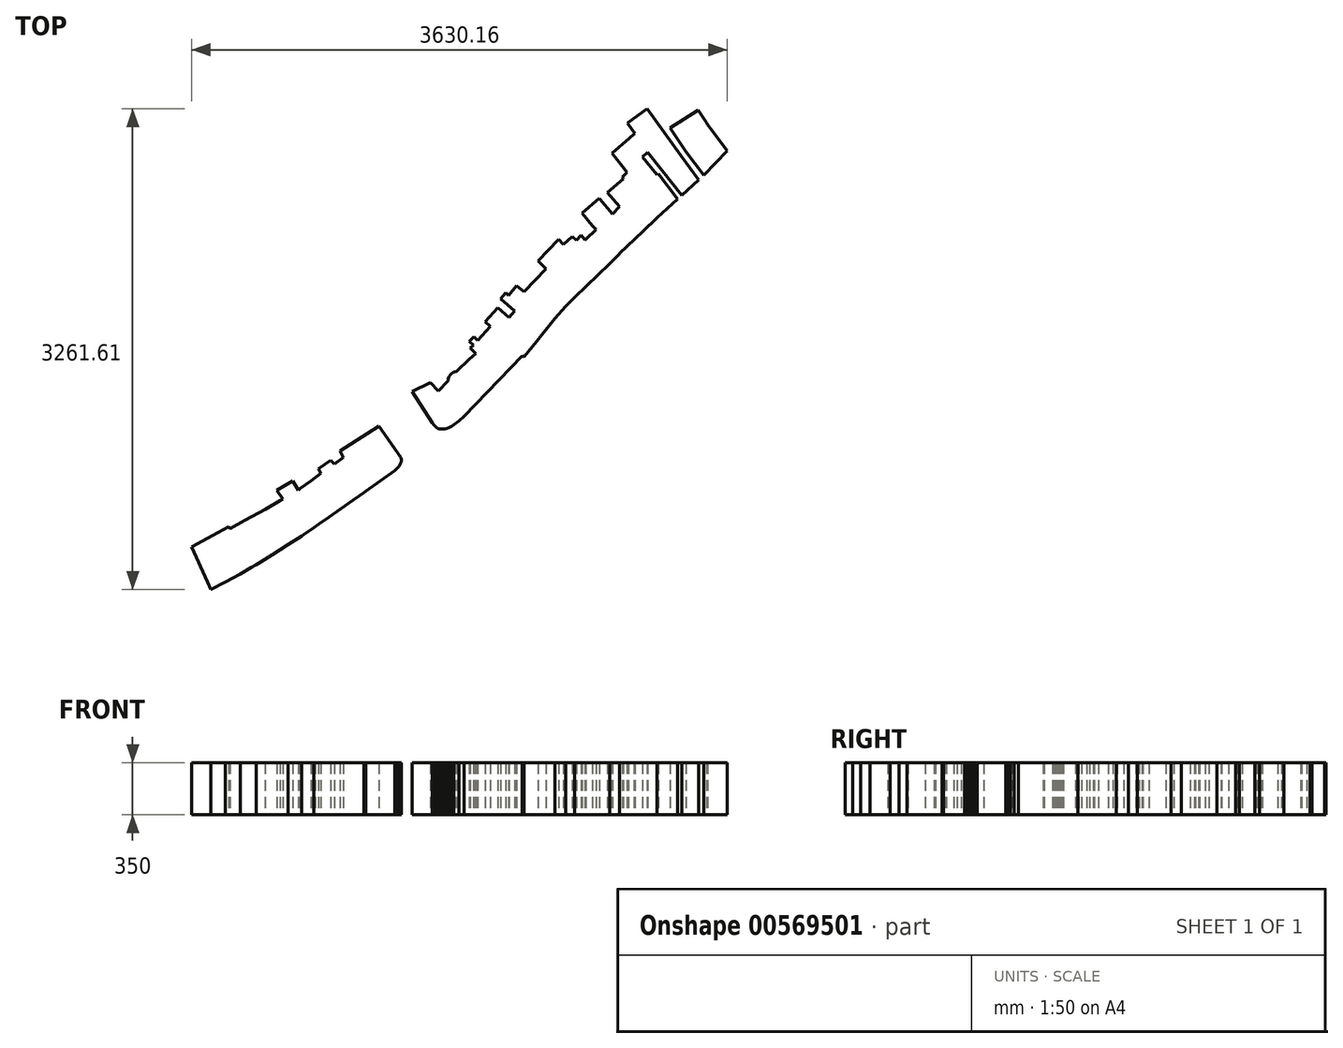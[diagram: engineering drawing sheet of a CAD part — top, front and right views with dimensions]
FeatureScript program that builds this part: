
annotation { "Feature Type Name" : "Feature", "Feature Type Description" : "" }
export const myFeature = defineFeature(function(context is Context, id is Id, definition is map)
    precondition{}
    {
        {
            var Q0;
            Q0=qCreatedBy(makeId("Top.planeOp"),FACE);
            var sketch = newSketch(context, id + "F0", { "sketchPlane" : qUnion([Q0])});
            skLineSegment(sketch, "E0", {"start": v(864.86, -2325.47) * mm, "end": v(899.9, -2380.58) * mm});
            skLineSegment(sketch, "E1", {"start": v(643.37, -1977.49) * mm, "end": v(719.57, -2092.3) * mm});
            skLineSegment(sketch, "E2", {"start": v(461.5, -1695.8) * mm, "end": v(495.8, -1752.95) * mm});
            skLineSegment(sketch, "E3", {"start": v(221.48, -1319.12) * mm, "end": v(179.57, -1255.11) * mm});
            skLineSegment(sketch, "E4", {"start": v(-61.73, -1340.7) * mm, "end": v(179.57, -1255.11) * mm});
            skLineSegment(sketch, "E5", {"start": v(784.34, 860.96) * mm, "end": v(794, 865.79) * mm});
            skLineSegment(sketch, "E6", {"start": v(-1984.51, 2355.5) * mm, "end": v(-1854.97, 2432.97) * mm});
            skLineSegment(sketch, "E7", {"start": v(-1903.23, 2229.77) * mm, "end": v(-1774.96, 2311.05) * mm});
            skLineSegment(sketch, "E8", {"start": v(265.42, -2033.62) * mm, "end": v(295.14, -2079.34) * mm});
            skLineSegment(sketch, "E9", {"start": v(295.14, -2079.34) * mm, "end": v(362.45, -2098.4) * mm});
            skLineSegment(sketch, "E10", {"start": v(362.45, -2098.4) * mm, "end": v(458.97, -2253.33) * mm});
            skLineSegment(sketch, "E11", {"start": v(458.97, -2253.33) * mm, "end": v(415.28, -2384.9) * mm});
            skLineSegment(sketch, "E12", {"start": v(1428.23, 985.42) * mm, "end": v(1558.79, 814.23) * mm});
            skLineSegment(sketch, "E13", {"start": v(1709.92, -1196.7) * mm, "end": v(1542.28, -1030.32) * mm});
            skLineSegment(sketch, "E14", {"start": v(1542.28, -1030.32) * mm, "end": v(1541.77, -1029.81) * mm});
            skLineSegment(sketch, "E15", {"start": v(2081.26, -1189.83) * mm, "end": v(2109.97, -1211.93) * mm});
            skLineSegment(sketch, "E16", {"start": v(2109.97, -1211.93) * mm, "end": v(2127.75, -1191.36) * mm});
            skLineSegment(sketch, "E17", {"start": v(913.37, -2395.82) * mm, "end": v(902.2, -2379.06) * mm});
            skLineSegment(sketch, "E18", {"start": v(902.2, -2379.06) * mm, "end": v(899.9, -2380.58) * mm});
            skLineSegment(sketch, "E19", {"start": v(899.9, -2380.58) * mm, "end": v(852.67, -2410.81) * mm});
            skLineSegment(sketch, "E20", {"start": v(852.67, -2410.81) * mm, "end": v(847.59, -2442.56) * mm});
            skLineSegment(sketch, "E21", {"start": v(847.59, -2442.56) * mm, "end": v(867.9, -2470.5) * mm});
            skLineSegment(sketch, "E22", {"start": v(867.9, -2470.5) * mm, "end": v(890.77, -2476.85) * mm});
            skLineSegment(sketch, "E23", {"start": v(890.77, -2476.85) * mm, "end": v(903.47, -2469.23) * mm});
            skLineSegment(sketch, "E24", {"start": v(-1735.6, -1544.67) * mm, "end": v(-1556.52, -1448.15) * mm});
            skLineSegment(sketch, "E25", {"start": v(-557.03, -1168.75) * mm, "end": v(-360.18, -1026.51) * mm});
            skLineSegment(sketch, "E26", {"start": v(2155.69, 896.27) * mm, "end": v(2129.02, 873.4) * mm});
            skLineSegment(sketch, "E27", {"start": v(2129.02, 873.4) * mm, "end": v(2121.4, 865.79) * mm});
            skLineSegment(sketch, "E28", {"start": v(2121.4, 865.79) * mm, "end": v(2116.32, 859.44) * mm});
            skLineSegment(sketch, "E29", {"start": v(2116.32, 859.44) * mm, "end": v(2019.8, 783.24) * mm});
            skLineSegment(sketch, "E30", {"start": v(2019.8, 783.24) * mm, "end": v(2004.56, 769.27) * mm});
            skLineSegment(sketch, "E31", {"start": v(2004.56, 769.27) * mm, "end": v(2000.75, 766.73) * mm});
            skLineSegment(sketch, "E32", {"start": v(2000.75, 766.73) * mm, "end": v(1982.97, 752.76) * mm});
            skLineSegment(sketch, "E33", {"start": v(1982.97, 752.76) * mm, "end": v(1976.62, 747.68) * mm});
            skLineSegment(sketch, "E34", {"start": v(1976.62, 747.68) * mm, "end": v(1972.8, 743.87) * mm});
            skLineSegment(sketch, "E35", {"start": v(1972.8, 743.87) * mm, "end": v(1969, 738.79) * mm});
            skLineSegment(sketch, "E36", {"start": v(1969, 738.79) * mm, "end": v(1966.46, 736.25) * mm});
            skLineSegment(sketch, "E37", {"start": v(1966.46, 736.25) * mm, "end": v(1963.92, 731.17) * mm});
            skLineSegment(sketch, "E38", {"start": v(1963.92, 731.17) * mm, "end": v(1960.1, 727.36) * mm});
            skLineSegment(sketch, "E39", {"start": v(1960.1, 727.36) * mm, "end": v(1939.79, 699.42) * mm});
            skLineSegment(sketch, "E40", {"start": v(1939.79, 699.42) * mm, "end": v(1935.98, 694.34) * mm});
            skLineSegment(sketch, "E41", {"start": v(1935.98, 694.34) * mm, "end": v(1849.62, 571.15) * mm});
            skLineSegment(sketch, "E42", {"start": v(1849.62, 571.15) * mm, "end": v(1843.27, 560.99) * mm});
            skLineSegment(sketch, "E43", {"start": v(1843.27, 560.99) * mm, "end": v(1830.57, 543.2) * mm});
            skLineSegment(sketch, "E44", {"start": v(1830.57, 543.2) * mm, "end": v(1822.95, 534.32) * mm});
            skLineSegment(sketch, "E45", {"start": v(1822.95, 534.32) * mm, "end": v(1810.25, 519.08) * mm});
            skLineSegment(sketch, "E46", {"start": v(1810.25, 519.08) * mm, "end": v(1773.42, 482.25) * mm});
            skLineSegment(sketch, "E47", {"start": v(1773.42, 482.25) * mm, "end": v(1755.64, 465.74) * mm});
            skLineSegment(sketch, "E48", {"start": v(1755.64, 465.74) * mm, "end": v(1740.4, 446.69) * mm});
            skLineSegment(sketch, "E49", {"start": v(1740.4, 446.69) * mm, "end": v(1739.13, 444.15) * mm});
            skLineSegment(sketch, "E50", {"start": v(1739.13, 444.15) * mm, "end": v(1562.6, 268.89) * mm});
            skLineSegment(sketch, "E51", {"start": v(1562.6, 268.89) * mm, "end": v(1539.74, 248.57) * mm});
            skLineSegment(sketch, "E52", {"start": v(1539.74, 248.57) * mm, "end": v(1533.39, 242.22) * mm});
            skLineSegment(sketch, "E53", {"start": v(1533.39, 242.22) * mm, "end": v(1511.8, 219.36) * mm});
            skLineSegment(sketch, "E54", {"start": v(1511.8, 219.36) * mm, "end": v(1501.64, 210.47) * mm});
            skLineSegment(sketch, "E55", {"start": v(1501.64, 210.47) * mm, "end": v(1492.75, 202.85) * mm});
            skLineSegment(sketch, "E56", {"start": v(1492.75, 202.85) * mm, "end": v(1485.13, 195.23) * mm});
            skLineSegment(sketch, "E57", {"start": v(1485.13, 195.23) * mm, "end": v(1474.97, 188.88) * mm});
            skLineSegment(sketch, "E58", {"start": v(1474.97, 188.88) * mm, "end": v(1464.8, 181.26) * mm});
            skLineSegment(sketch, "E59", {"start": v(1464.8, 181.26) * mm, "end": v(1457.19, 174.9) * mm});
            skLineSegment(sketch, "E60", {"start": v(1457.19, 174.9) * mm, "end": v(1421.63, 149.5) * mm});
            skLineSegment(sketch, "E61", {"start": v(1421.63, 149.5) * mm, "end": v(1416.55, 145.7) * mm});
            skLineSegment(sketch, "E62", {"start": v(1416.55, 145.7) * mm, "end": v(1191.76, -19.4) * mm});
            skLineSegment(sketch, "E63", {"start": v(1191.76, -19.4) * mm, "end": v(1186.68, -24.48) * mm});
            skLineSegment(sketch, "E64", {"start": v(1186.68, -24.48) * mm, "end": v(1176.52, -32.1) * mm});
            skLineSegment(sketch, "E65", {"start": v(1176.52, -32.1) * mm, "end": v(1171.44, -37.18) * mm});
            skLineSegment(sketch, "E66", {"start": v(1171.44, -37.18) * mm, "end": v(1167.63, -42.26) * mm});
            skLineSegment(sketch, "E67", {"start": v(1167.63, -42.26) * mm, "end": v(1162.55, -46.07) * mm});
            skLineSegment(sketch, "E68", {"start": v(1162.55, -46.07) * mm, "end": v(1153.66, -54.96) * mm});
            skLineSegment(sketch, "E69", {"start": v(1153.66, -54.96) * mm, "end": v(1151.12, -58.77) * mm});
            skLineSegment(sketch, "E70", {"start": v(1151.12, -58.77) * mm, "end": v(1143.5, -68.93) * mm});
            skLineSegment(sketch, "E71", {"start": v(1143.5, -68.93) * mm, "end": v(1139.69, -75.28) * mm});
            skLineSegment(sketch, "E72", {"start": v(1139.69, -75.28) * mm, "end": v(1135.88, -80.36) * mm});
            skLineSegment(sketch, "E73", {"start": v(1135.88, -80.36) * mm, "end": v(1132.07, -86.71) * mm});
            skLineSegment(sketch, "E74", {"start": v(1132.07, -86.71) * mm, "end": v(1129.53, -93.06) * mm});
            skLineSegment(sketch, "E75", {"start": v(1129.53, -93.06) * mm, "end": v(1125.72, -98.14) * mm});
            skLineSegment(sketch, "E76", {"start": v(1125.72, -98.14) * mm, "end": v(1123.18, -104.5) * mm});
            skLineSegment(sketch, "E77", {"start": v(1123.18, -104.5) * mm, "end": v(1120.64, -109.57) * mm});
            skLineSegment(sketch, "E78", {"start": v(1120.64, -109.57) * mm, "end": v(1119.37, -115.92) * mm});
            skLineSegment(sketch, "E79", {"start": v(1119.37, -115.92) * mm, "end": v(1116.83, -122.27) * mm});
            skLineSegment(sketch, "E80", {"start": v(1116.83, -122.27) * mm, "end": v(1115.56, -128.62) * mm});
            skLineSegment(sketch, "E81", {"start": v(1115.56, -128.62) * mm, "end": v(1113.02, -136.24) * mm});
            skLineSegment(sketch, "E82", {"start": v(1113.02, -136.24) * mm, "end": v(1111.75, -143.86) * mm});
            skLineSegment(sketch, "E83", {"start": v(1111.75, -143.86) * mm, "end": v(1107.94, -162.91) * mm});
            skLineSegment(sketch, "E84", {"start": v(1107.94, -162.91) * mm, "end": v(1107.94, -169.26) * mm});
            skLineSegment(sketch, "E85", {"start": v(1107.94, -169.26) * mm, "end": v(1106.67, -176.88) * mm});
            skLineSegment(sketch, "E86", {"start": v(2909.56, 1433.48) * mm, "end": v(2931.66, 1416.97) * mm});
            skLineSegment(sketch, "E87", {"start": v(-64.27, -1284.57) * mm, "end": v(307.84, -1049.37) * mm});
            skLineSegment(sketch, "E88", {"start": v(475.48, -1305.91) * mm, "end": v(394.2, -1357.98) * mm});
            skLineSegment(sketch, "E89", {"start": v(394.2, -1357.98) * mm, "end": v(565.65, -1627.22) * mm});
            skLineSegment(sketch, "E90", {"start": v(565.65, -1627.22) * mm, "end": v(545.33, -1639.92) * mm});
            skLineSegment(sketch, "E91", {"start": v(545.33, -1639.92) * mm, "end": v(359.9, -1347.82) * mm});
            skLineSegment(sketch, "E92", {"start": v(359.9, -1347.82) * mm, "end": v(461.76, -1284.32) * mm});
            skLineSegment(sketch, "E93", {"start": v(461.76, -1284.32) * mm, "end": v(481.83, -1271.62) * mm});
            skLineSegment(sketch, "E94", {"start": v(481.83, -1271.62) * mm, "end": v(460.24, -1237.33) * mm});
            skLineSegment(sketch, "E95", {"start": v(460.24, -1237.33) * mm, "end": v(483.1, -1223.36) * mm});
            skLineSegment(sketch, "E96", {"start": v(483.1, -1223.36) * mm, "end": v(517.39, -1279.24) * mm});
            skLineSegment(sketch, "E97", {"start": v(517.39, -1279.24) * mm, "end": v(475.48, -1305.91) * mm});
            skLineSegment(sketch, "E98", {"start": v(2099.3, -1166.72) * mm, "end": v(2115.55, -1146.14) * mm});
            skLineSegment(sketch, "E99", {"start": v(3049.77, 1229) * mm, "end": v(3137.4, 1157.89) * mm});
            skLineSegment(sketch, "E100", {"start": v(763.77, -2254.6) * mm, "end": v(805.68, -2227.42) * mm});
            skLineSegment(sketch, "E101", {"start": v(1184.9, 1034.45) * mm, "end": v(1113.02, 1124.87) * mm});
            skLineSegment(sketch, "E102", {"start": v(1113.02, 1124.87) * mm, "end": v(1232.14, 1228) * mm});
            skLineSegment(sketch, "E103", {"start": v(-977.15, -1461.36) * mm, "end": v(-908.82, -1415.13) * mm});
            skLineSegment(sketch, "E104", {"start": v(-908.82, -1415.13) * mm, "end": v(-873.26, -1389.73) * mm});
            skLineSegment(sketch, "E105", {"start": v(3137.4, 1157.89) * mm, "end": v(3129.78, 1154.08) * mm});
            skLineSegment(sketch, "E106", {"start": v(3129.78, 1154.08) * mm, "end": v(3123.43, 1149) * mm});
            skLineSegment(sketch, "E107", {"start": v(3123.43, 1149) * mm, "end": v(3114.54, 1140.1) * mm});
            skLineSegment(sketch, "E108", {"start": v(3114.54, 1140.1) * mm, "end": v(3106.92, 1129.95) * mm});
            skLineSegment(sketch, "E109", {"start": v(3106.92, 1129.95) * mm, "end": v(3104.38, 1122.33) * mm});
            skLineSegment(sketch, "E110", {"start": v(3104.38, 1122.33) * mm, "end": v(3103.1, 1115.98) * mm});
            skLineSegment(sketch, "E111", {"start": v(3103.1, 1115.98) * mm, "end": v(3101.84, 1108.36) * mm});
            skLineSegment(sketch, "E112", {"start": v(3101.84, 1108.36) * mm, "end": v(3101.84, 1099.47) * mm});
            skLineSegment(sketch, "E113", {"start": v(3101.84, 1099.47) * mm, "end": v(3104.38, 1091.85) * mm});
            skLineSegment(sketch, "E114", {"start": v(3104.38, 1091.85) * mm, "end": v(3106.92, 1082.96) * mm});
            skLineSegment(sketch, "E115", {"start": v(3106.92, 1082.96) * mm, "end": v(3110.73, 1075.34) * mm});
            skLineSegment(sketch, "E116", {"start": v(3110.73, 1075.34) * mm, "end": v(3117.08, 1068.99) * mm});
            skLineSegment(sketch, "E117", {"start": v(3117.08, 1068.99) * mm, "end": v(3122.16, 1062.64) * mm});
            skLineSegment(sketch, "E118", {"start": v(682.49, -1184) * mm, "end": v(1147.56, -732.89) * mm});
            skLineSegment(sketch, "E119", {"start": v(-767.85, -1738.98) * mm, "end": v(-718.32, -1695.8) * mm});
            skLineSegment(sketch, "E120", {"start": v(371.34, -1625.95) * mm, "end": v(405.37, -1603.1) * mm});
            skLineSegment(sketch, "E121", {"start": v(2115.55, -1146.14) * mm, "end": v(2065.52, -1109.06) * mm});
            skLineSegment(sketch, "E122", {"start": v(1290.82, -881.73) * mm, "end": v(1343.9, -826.87) * mm});
            skLineSegment(sketch, "E123", {"start": v(-718.32, -1695.8) * mm, "end": v(-84.6, -1298.3) * mm});
            skLineSegment(sketch, "E124", {"start": v(-1081.54, -1530.2) * mm, "end": v(-991.37, -1471.01) * mm});
            skLineSegment(sketch, "E125", {"start": v(-991.37, -1471.01) * mm, "end": v(-977.15, -1461.36) * mm});
            skLineSegment(sketch, "E126", {"start": v(-331.74, -1834.48) * mm, "end": v(-346.21, -1827.88) * mm});
            skLineSegment(sketch, "E127", {"start": v(-346.21, -1827.88) * mm, "end": v(-299.22, -1702.15) * mm});
            skLineSegment(sketch, "E128", {"start": v(-299.22, -1702.15) * mm, "end": v(-201.43, -1641.2) * mm});
            skLineSegment(sketch, "E129", {"start": v(-201.43, -1641.2) * mm, "end": v(-174.76, -1647.54) * mm});
            skLineSegment(sketch, "E130", {"start": v(417.06, 11.08) * mm, "end": v(452.62, 54.26) * mm});
            skLineSegment(sketch, "E131", {"start": v(-731.02, -895.7) * mm, "end": v(-546.87, -777.6) * mm});
            skLineSegment(sketch, "E132", {"start": v(791.7, -2295.24) * mm, "end": v(779, -2304.13) * mm});
            skLineSegment(sketch, "E133", {"start": v(779, -2304.13) * mm, "end": v(777.74, -2327) * mm});
            skLineSegment(sketch, "E134", {"start": v(777.74, -2327) * mm, "end": v(791.7, -2349.85) * mm});
            skLineSegment(sketch, "E135", {"start": v(791.7, -2349.85) * mm, "end": v(814.57, -2354.93) * mm});
            skLineSegment(sketch, "E136", {"start": v(814.57, -2354.93) * mm, "end": v(864.86, -2325.47) * mm});
            skLineSegment(sketch, "E137", {"start": v(864.86, -2325.47) * mm, "end": v(866.64, -2324.45) * mm});
            skLineSegment(sketch, "E138", {"start": v(866.64, -2324.45) * mm, "end": v(831.84, -2268.82) * mm});
            skLineSegment(sketch, "E139", {"start": v(-1523.5, -1341.47) * mm, "end": v(-1485.4, -1410.05) * mm});
            skLineSegment(sketch, "E140", {"start": v(1586.98, 839.88) * mm, "end": v(1700.52, 943.51) * mm});
            skLineSegment(sketch, "E141", {"start": v(2909.56, 1433.48) * mm, "end": v(2940.8, 1482.25) * mm});
            skLineSegment(sketch, "E142", {"start": v(1765.8, -965.04) * mm, "end": v(1872.48, -1079.85) * mm});
            skLineSegment(sketch, "E143", {"start": v(1872.48, -1079.85) * mm, "end": v(1901.69, -1053.18) * mm});
            skLineSegment(sketch, "E144", {"start": v(2727.7, -636.87) * mm, "end": v(2654.8, -584.55) * mm});
            skLineSegment(sketch, "E145", {"start": v(2654.8, -584.55) * mm, "end": v(2171.18, -1141.32) * mm});
            skLineSegment(sketch, "E146", {"start": v(-1606.05, -1835.5) * mm, "end": v(-1508.26, -1784.7) * mm});
            skLineSegment(sketch, "E147", {"start": v(-1508.26, -1784.7) * mm, "end": v(-1407.93, -1728.82) * mm});
            skLineSegment(sketch, "E148", {"start": v(-1407.93, -1728.82) * mm, "end": v(-1333, -1685.39) * mm});
            skLineSegment(sketch, "E149", {"start": v(931.4, 536.86) * mm, "end": v(1098.28, 375.06) * mm});
            skLineSegment(sketch, "E150", {"start": v(-1451.11, -1227.17) * mm, "end": v(-1124.72, -1022.7) * mm});
            skLineSegment(sketch, "E151", {"start": v(2833.87, -1911.7) * mm, "end": v(2797.04, -1879.95) * mm});
            skLineSegment(sketch, "E152", {"start": v(-746.26, -1784.7) * mm, "end": v(-685.56, -1748.12) * mm});
            skLineSegment(sketch, "E153", {"start": v(1166.36, 764.19) * mm, "end": v(1118.1, 713.39) * mm});
            skLineSegment(sketch, "E154", {"start": v(1118.1, 713.39) * mm, "end": v(1031.99, 813.97) * mm});
            skLineSegment(sketch, "E155", {"start": v(638.54, -107.03) * mm, "end": v(726.94, 3.46) * mm});
            skLineSegment(sketch, "E156", {"start": v(-2161.55, -2500.73) * mm, "end": v(-2149.61, -2631.8) * mm});
            skLineSegment(sketch, "E157", {"start": v(-696.73, -1959.96) * mm, "end": v(-723.4, -1977.23) * mm});
            skLineSegment(sketch, "E158", {"start": v(-1475.24, -1420.21) * mm, "end": v(-1376.18, -1365.6) * mm});
            skLineSegment(sketch, "E159", {"start": v(2217.92, -1609.44) * mm, "end": v(1970.27, -1397.35) * mm});
            skLineSegment(sketch, "E160", {"start": v(1970.27, -1397.35) * mm, "end": v(1965.19, -1394.81) * mm});
            skLineSegment(sketch, "E161", {"start": v(1965.19, -1394.81) * mm, "end": v(1962.65, -1392.27) * mm});
            skLineSegment(sketch, "E162", {"start": v(1962.65, -1392.27) * mm, "end": v(1957.57, -1391) * mm});
            skLineSegment(sketch, "E163", {"start": v(1957.57, -1391) * mm, "end": v(1955.03, -1389.73) * mm});
            skLineSegment(sketch, "E164", {"start": v(1955.03, -1389.73) * mm, "end": v(1951.22, -1387.2) * mm});
            skLineSegment(sketch, "E165", {"start": v(1951.22, -1387.2) * mm, "end": v(1941.06, -1384.65) * mm});
            skLineSegment(sketch, "E166", {"start": v(1941.06, -1384.65) * mm, "end": v(1937.25, -1383.38) * mm});
            skLineSegment(sketch, "E167", {"start": v(1937.25, -1383.38) * mm, "end": v(1933.44, -1383.38) * mm});
            skLineSegment(sketch, "E168", {"start": v(1933.44, -1383.38) * mm, "end": v(1930.9, -1384.65) * mm});
            skLineSegment(sketch, "E169", {"start": v(1930.9, -1384.65) * mm, "end": v(1927.09, -1384.65) * mm});
            skLineSegment(sketch, "E170", {"start": v(1927.09, -1384.65) * mm, "end": v(1906.77, -1389.73) * mm});
            skLineSegment(sketch, "E171", {"start": v(-1551.44, -1289.4) * mm, "end": v(-1451.11, -1227.17) * mm});
            skLineSegment(sketch, "E172", {"start": v(-1012.96, -1159.86) * mm, "end": v(-999, -1149.7) * mm});
            skLineSegment(sketch, "E173", {"start": v(-999, -1149.7) * mm, "end": v(-927.87, -1096.36) * mm});
            skLineSegment(sketch, "E174", {"start": v(-927.87, -1096.36) * mm, "end": v(-899.93, -1074.77) * mm});
            skLineSegment(sketch, "E175", {"start": v(-899.93, -1074.77) * mm, "end": v(-859.3, -1045.56) * mm});
            skLineSegment(sketch, "E176", {"start": v(-859.3, -1045.56) * mm, "end": v(-875.8, -1015.08) * mm});
            skLineSegment(sketch, "E177", {"start": v(-875.8, -1015.08) * mm, "end": v(-794.52, -956.66) * mm});
            skLineSegment(sketch, "E178", {"start": v(1454.9, 719.49) * mm, "end": v(1283.2, 912.78) * mm});
            skLineSegment(sketch, "E179", {"start": v(1283.2, 912.78) * mm, "end": v(1217.16, 994.06) * mm});
            skLineSegment(sketch, "E180", {"start": v(2739.89, -645.51) * mm, "end": v(2727.7, -636.87) * mm});
            skLineSegment(sketch, "E181", {"start": v(1773.16, -2046.57) * mm, "end": v(1819.64, -2015.59) * mm});
            skLineSegment(sketch, "E182", {"start": v(-1622.56, -1333.85) * mm, "end": v(-1594.62, -1379.57) * mm});
            skLineSegment(sketch, "E183", {"start": v(1630.92, -759.81) * mm, "end": v(1453.88, -572.36) * mm});
            skLineSegment(sketch, "E184", {"start": v(-2130.82, -2494.88) * mm, "end": v(-2152.66, -2403.2) * mm});
            skLineSegment(sketch, "E185", {"start": v(2230.62, -1228.19) * mm, "end": v(2739.89, -645.51) * mm});
            skLineSegment(sketch, "E186", {"start": v(-242.07, -491.84) * mm, "end": v(-118.88, -429.61) * mm});
            skLineSegment(sketch, "E187", {"start": v(-118.88, -429.61) * mm, "end": v(-63, -486.76) * mm});
            skLineSegment(sketch, "E188", {"start": v(-63, -486.76) * mm, "end": v(1.77, -419.45) * mm});
            skLineSegment(sketch, "E189", {"start": v(1.77, -419.45) * mm, "end": v(1.77, -414.37) * mm});
            skLineSegment(sketch, "E190", {"start": v(1.77, -414.37) * mm, "end": v(3.04, -405.48) * mm});
            skLineSegment(sketch, "E191", {"start": v(3.04, -405.48) * mm, "end": v(5.58, -396.6) * mm});
            skLineSegment(sketch, "E192", {"start": v(5.58, -396.6) * mm, "end": v(8.12, -388.97) * mm});
            skLineSegment(sketch, "E193", {"start": v(8.12, -388.97) * mm, "end": v(18.28, -376.27) * mm});
            skLineSegment(sketch, "E194", {"start": v(18.28, -376.27) * mm, "end": v(20.82, -375) * mm});
            skLineSegment(sketch, "E195", {"start": v(20.82, -375) * mm, "end": v(25.9, -369.92) * mm});
            skLineSegment(sketch, "E196", {"start": v(25.9, -369.92) * mm, "end": v(37.33, -361.03) * mm});
            skLineSegment(sketch, "E197", {"start": v(37.33, -361.03) * mm, "end": v(42.4, -358.5) * mm});
            skLineSegment(sketch, "E198", {"start": v(42.4, -358.5) * mm, "end": v(46.22, -357.22) * mm});
            skLineSegment(sketch, "E199", {"start": v(46.22, -357.22) * mm, "end": v(61.46, -354.68) * mm});
            skLineSegment(sketch, "E200", {"start": v(61.46, -354.68) * mm, "end": v(146.55, -272.13) * mm});
            skLineSegment(sketch, "E201", {"start": v(146.55, -272.13) * mm, "end": v(189.73, -232.76) * mm});
            skLineSegment(sketch, "E202", {"start": v(189.73, -232.76) * mm, "end": v(152.9, -197.2) * mm});
            skLineSegment(sketch, "E203", {"start": v(152.9, -197.2) * mm, "end": v(173.22, -176.88) * mm});
            skLineSegment(sketch, "E204", {"start": v(173.22, -176.88) * mm, "end": v(146.55, -152.75) * mm});
            skLineSegment(sketch, "E205", {"start": v(1699.5, 1416.72) * mm, "end": v(1755.13, 1331.88) * mm});
            skLineSegment(sketch, "E206", {"start": v(178.04, -2013.8) * mm, "end": v(415.28, -2384.9) * mm});
            skLineSegment(sketch, "E207", {"start": v(1269.23, 1259.49) * mm, "end": v(1356.86, 1129.95) * mm});
            skLineSegment(sketch, "E208", {"start": v(-1523.5, -1341.47) * mm, "end": v(-1551.44, -1289.4) * mm});
            skLineSegment(sketch, "E209", {"start": v(1509.26, -1060.04) * mm, "end": v(1481.32, -1086.2) * mm});
            skLineSegment(sketch, "E210", {"start": v(1481.32, -1086.2) * mm, "end": v(1431.79, -1035.4) * mm});
            skLineSegment(sketch, "E211", {"start": v(1431.79, -1035.4) * mm, "end": v(1459.47, -1008.48) * mm});
            skLineSegment(sketch, "E212", {"start": v(-1622.56, -1333.85) * mm, "end": v(-1551.44, -1289.4) * mm});
            skLineSegment(sketch, "E213", {"start": v(3030.72, 1244.25) * mm, "end": v(3049.77, 1229) * mm});
            skLineSegment(sketch, "E214", {"start": v(1614.67, 1135.03) * mm, "end": v(1581.65, 1108.61) * mm});
            skLineSegment(sketch, "E215", {"start": v(452.62, 54.26) * mm, "end": v(357.37, 138.08) * mm});
            skLineSegment(sketch, "E216", {"start": v(357.37, 138.08) * mm, "end": v(392.93, 177.45) * mm});
            skLineSegment(sketch, "E217", {"start": v(392.93, 177.45) * mm, "end": v(411.98, 159.67) * mm});
            skLineSegment(sketch, "E218", {"start": v(411.98, 159.67) * mm, "end": v(467.86, 225.7) * mm});
            skLineSegment(sketch, "E219", {"start": v(467.86, 225.7) * mm, "end": v(515.86, 184.56) * mm});
            skLineSegment(sketch, "E220", {"start": v(-546.87, -777.6) * mm, "end": v(-360.18, -1026.51) * mm});
            skLineSegment(sketch, "E221", {"start": v(944.87, -2443.07) * mm, "end": v(986.02, -2417.16) * mm});
            skLineSegment(sketch, "E222", {"start": v(986.02, -2417.16) * mm, "end": v(1012.69, -2459.07) * mm});
            skLineSegment(sketch, "E223", {"start": v(1012.69, -2459.07) * mm, "end": v(967.98, -2486.76) * mm});
            skLineSegment(sketch, "E224", {"start": v(903.47, -2469.23) * mm, "end": v(944.87, -2443.07) * mm});
            skLineSegment(sketch, "E225", {"start": v(-1735.6, -1544.67) * mm, "end": v(-1780.04, -1432.91) * mm});
            skLineSegment(sketch, "E226", {"start": v(-1780.04, -1432.91) * mm, "end": v(-1622.56, -1333.85) * mm});
            skLineSegment(sketch, "E227", {"start": v(615.68, -1934.05) * mm, "end": v(659.63, -1907.9) * mm});
            skLineSegment(sketch, "E228", {"start": v(659.63, -1907.9) * mm, "end": v(686.3, -1951.07) * mm});
            skLineSegment(sketch, "E229", {"start": v(686.3, -1951.07) * mm, "end": v(601.2, -2003.14) * mm});
            skLineSegment(sketch, "E230", {"start": v(601.2, -2003.14) * mm, "end": v(574.54, -1958.7) * mm});
            skLineSegment(sketch, "E231", {"start": v(1980.43, -1467.2) * mm, "end": v(1906.77, -1389.73) * mm});
            skLineSegment(sketch, "E232", {"start": v(-1124.72, -1022.7) * mm, "end": v(-786.9, -810.61) * mm});
            skLineSegment(sketch, "E233", {"start": v(-786.9, -810.61) * mm, "end": v(-731.02, -895.7) * mm});
            skLineSegment(sketch, "E234", {"start": v(301.74, -1450.94) * mm, "end": v(239.26, -1378.3) * mm});
            skLineSegment(sketch, "E235", {"start": v(239.26, -1378.3) * mm, "end": v(211.32, -1399.9) * mm});
            skLineSegment(sketch, "E236", {"start": v(211.32, -1399.9) * mm, "end": v(198.62, -1429.1) * mm});
            skLineSegment(sketch, "E237", {"start": v(198.62, -1429.1) * mm, "end": v(226.56, -1473.55) * mm});
            skLineSegment(sketch, "E238", {"start": v(226.56, -1473.55) * mm, "end": v(255.77, -1481.17) * mm});
            skLineSegment(sketch, "E239", {"start": v(255.77, -1481.17) * mm, "end": v(271, -1471.01) * mm});
            skLineSegment(sketch, "E240", {"start": v(726.94, 3.46) * mm, "end": v(799.33, 86) * mm});
            skLineSegment(sketch, "E241", {"start": v(799.33, 86) * mm, "end": v(859.02, 146.97) * mm});
            skLineSegment(sketch, "E242", {"start": v(750.3, -2140.8) * mm, "end": v(707.89, -2168.24) * mm});
            skLineSegment(sketch, "E243", {"start": v(3049.77, 1229) * mm, "end": v(3071.36, 1241.7) * mm});
            skLineSegment(sketch, "E244", {"start": v(3071.36, 1241.7) * mm, "end": v(3171.69, 1166.78) * mm});
            skLineSegment(sketch, "E245", {"start": v(3171.69, 1166.78) * mm, "end": v(3148.83, 1162.97) * mm});
            skLineSegment(sketch, "E246", {"start": v(3148.83, 1162.97) * mm, "end": v(3145.02, 1161.7) * mm});
            skLineSegment(sketch, "E247", {"start": v(3145.02, 1161.7) * mm, "end": v(3137.4, 1157.89) * mm});
            skLineSegment(sketch, "E248", {"start": v(1541.77, -1029.81) * mm, "end": v(1513.07, -1001.11) * mm});
            skLineSegment(sketch, "E249", {"start": v(-1594.62, -1379.57) * mm, "end": v(-1556.52, -1448.15) * mm});
            skLineSegment(sketch, "E250", {"start": v(-794.52, -956.66) * mm, "end": v(-767.85, -983.33) * mm});
            skLineSegment(sketch, "E251", {"start": v(-767.85, -983.33) * mm, "end": v(-708.16, -937.61) * mm});
            skLineSegment(sketch, "E252", {"start": v(2049, -1128.11) * mm, "end": v(2065.52, -1109.06) * mm});
            skLineSegment(sketch, "E253", {"start": v(2171.18, -1141.32) * mm, "end": v(2235.7, -1189.07) * mm});
            skLineSegment(sketch, "E254", {"start": v(-762.01, -1761.59) * mm, "end": v(-700.3, -1869.03) * mm});
            skLineSegment(sketch, "E255", {"start": v(-700.3, -1869.03) * mm, "end": v(-662.44, -1934.81) * mm});
            skLineSegment(sketch, "E256", {"start": v(296.4, -1510.38) * mm, "end": v(283.7, -1521.81) * mm});
            skLineSegment(sketch, "E257", {"start": v(283.7, -1521.81) * mm, "end": v(272.28, -1548.48) * mm});
            skLineSegment(sketch, "E258", {"start": v(272.28, -1548.48) * mm, "end": v(328.16, -1632.3) * mm});
            skLineSegment(sketch, "E259", {"start": v(328.16, -1632.3) * mm, "end": v(353.56, -1638.65) * mm});
            skLineSegment(sketch, "E260", {"start": v(353.56, -1638.65) * mm, "end": v(371.34, -1625.95) * mm});
            skLineSegment(sketch, "E261", {"start": v(-708.16, -937.61) * mm, "end": v(-557.03, -1168.75) * mm});
            skLineSegment(sketch, "E262", {"start": v(178.04, -2013.8) * mm, "end": v(231.64, -1981.55) * mm});
            skLineSegment(sketch, "E263", {"start": v(231.64, -1981.55) * mm, "end": v(265.42, -2033.62) * mm});
            skLineSegment(sketch, "E264", {"start": v(2863.58, 1786.03) * mm, "end": v(2771.64, 1654.46) * mm});
            skLineSegment(sketch, "E265", {"start": v(2771.64, 1654.46) * mm, "end": v(2813.8, 1624.49) * mm});
            skLineSegment(sketch, "E266", {"start": v(515.86, 184.56) * mm, "end": v(726.94, 3.46) * mm});
            skLineSegment(sketch, "E267", {"start": v(707.89, -2168.24) * mm, "end": v(696.46, -2175.86) * mm});
            skLineSegment(sketch, "E268", {"start": v(696.46, -2175.86) * mm, "end": v(693.92, -2197.45) * mm});
            skLineSegment(sketch, "E269", {"start": v(693.92, -2197.45) * mm, "end": v(726.94, -2254.6) * mm});
            skLineSegment(sketch, "E270", {"start": v(726.94, -2254.6) * mm, "end": v(751.07, -2262.22) * mm});
            skLineSegment(sketch, "E271", {"start": v(751.07, -2262.22) * mm, "end": v(763.77, -2254.6) * mm});
            skLineSegment(sketch, "E272", {"start": v(-4.58, -884.27) * mm, "end": v(18.28, -871.57) * mm});
            skLineSegment(sketch, "E273", {"start": v(18.28, -871.57) * mm, "end": v(58.92, -844.9) * mm});
            skLineSegment(sketch, "E274", {"start": v(58.92, -844.9) * mm, "end": v(102.1, -810.61) * mm});
            skLineSegment(sketch, "E275", {"start": v(102.1, -810.61) * mm, "end": v(145.28, -775.05) * mm});
            skLineSegment(sketch, "E276", {"start": v(145.28, -775.05) * mm, "end": v(170.68, -750.92) * mm});
            skLineSegment(sketch, "E277", {"start": v(170.68, -750.92) * mm, "end": v(196.08, -725.52) * mm});
            skLineSegment(sketch, "E278", {"start": v(196.08, -725.52) * mm, "end": v(220.2, -700.12) * mm});
            skLineSegment(sketch, "E279", {"start": v(220.2, -700.12) * mm, "end": v(243.07, -672.18) * mm});
            skLineSegment(sketch, "E280", {"start": v(243.07, -672.18) * mm, "end": v(323.08, -578.2) * mm});
            skLineSegment(sketch, "E281", {"start": v(410.45, -1111.85) * mm, "end": v(380.23, -1065.88) * mm});
            skLineSegment(sketch, "E282", {"start": v(380.23, -1065.88) * mm, "end": v(354.83, -1081.12) * mm});
            skLineSegment(sketch, "E283", {"start": v(354.83, -1081.12) * mm, "end": v(325.62, -1036.42) * mm});
            skLineSegment(sketch, "E284", {"start": v(-1594.62, -1379.57) * mm, "end": v(-1523.5, -1341.47) * mm});
            skLineSegment(sketch, "E285", {"start": v(-1451.11, -1227.17) * mm, "end": v(-1419.36, -1285.6) * mm});
            skLineSegment(sketch, "E286", {"start": v(-1419.36, -1285.6) * mm, "end": v(-1376.18, -1365.6) * mm});
            skLineSegment(sketch, "E287", {"start": v(-2370.6, -820.77) * mm, "end": v(-2375.67, -833.47) * mm});
            skLineSegment(sketch, "E288", {"start": v(-2375.67, -833.47) * mm, "end": v(-2380.75, -851.25) * mm});
            skLineSegment(sketch, "E289", {"start": v(-2380.75, -851.25) * mm, "end": v(-2385.83, -894.43) * mm});
            skLineSegment(sketch, "E290", {"start": v(-2385.83, -894.43) * mm, "end": v(-2387.1, -903.32) * mm});
            skLineSegment(sketch, "E291", {"start": v(-2387.1, -903.32) * mm, "end": v(-2387.1, -921.1) * mm});
            skLineSegment(sketch, "E292", {"start": v(-2387.1, -921.1) * mm, "end": v(-2383.3, -938.88) * mm});
            skLineSegment(sketch, "E293", {"start": v(-2383.3, -938.88) * mm, "end": v(-2379.48, -950.31) * mm});
            skLineSegment(sketch, "E294", {"start": v(-2379.48, -950.31) * mm, "end": v(-2373.13, -965.55) * mm});
            skLineSegment(sketch, "E295", {"start": v(-2373.13, -965.55) * mm, "end": v(-2042.93, -1683.1) * mm});
            skLineSegment(sketch, "E296", {"start": v(-2042.93, -1683.1) * mm, "end": v(-2041.66, -1732.63) * mm});
            skLineSegment(sketch, "E297", {"start": v(-2041.66, -1732.63) * mm, "end": v(-1934.98, -1973.93) * mm});
            skLineSegment(sketch, "E298", {"start": v(-1934.98, -1973.93) * mm, "end": v(-1931.17, -1982.82) * mm});
            skLineSegment(sketch, "E299", {"start": v(-1931.17, -1982.82) * mm, "end": v(-1921.01, -1998.06) * mm});
            skLineSegment(sketch, "E300", {"start": v(-1921.01, -1998.06) * mm, "end": v(-1908.31, -2010.76) * mm});
            skLineSegment(sketch, "E301", {"start": v(-1908.31, -2010.76) * mm, "end": v(-1901.96, -2015.84) * mm});
            skLineSegment(sketch, "E302", {"start": v(-1901.96, -2015.84) * mm, "end": v(-1896.88, -2019.65) * mm});
            skLineSegment(sketch, "E303", {"start": v(-1896.88, -2019.65) * mm, "end": v(-1890.53, -2023.46) * mm});
            skLineSegment(sketch, "E304", {"start": v(-1890.53, -2023.46) * mm, "end": v(-1879.1, -2027.27) * mm});
            skLineSegment(sketch, "E305", {"start": v(2931.66, 1416.97) * mm, "end": v(2917.69, 1397.92) * mm});
            skLineSegment(sketch, "E306", {"start": v(2917.69, 1397.92) * mm, "end": v(2879.59, 1401.73) * mm});
            skLineSegment(sketch, "E307", {"start": v(2879.59, 1401.73) * mm, "end": v(2877.05, 1359.82) * mm});
            skLineSegment(sketch, "E308", {"start": v(2877.05, 1359.82) * mm, "end": v(2907.53, 1334.42) * mm});
            skLineSegment(sketch, "E309", {"start": v(-2370.6, -820.77) * mm, "end": v(-2321.06, -616.3) * mm});
            skLineSegment(sketch, "E310", {"start": v(1166.36, 444.15) * mm, "end": v(1322.57, 594) * mm});
            skLineSegment(sketch, "E311", {"start": v(2813.8, 1624.49) * mm, "end": v(2790.69, 1592.23) * mm});
            skLineSegment(sketch, "E312", {"start": v(2790.69, 1592.23) * mm, "end": v(2826.25, 1566.07) * mm});
            skLineSegment(sketch, "E313", {"start": v(-546.87, -777.6) * mm, "end": v(-465.6, -725.52) * mm});
            skLineSegment(sketch, "E314", {"start": v(2039.1, -1139.8) * mm, "end": v(2089.14, -1179.67) * mm});
            skLineSegment(sketch, "E315", {"start": v(1513.07, -1001.11) * mm, "end": v(1482.84, -1032.6) * mm});
            skLineSegment(sketch, "E316", {"start": v(448.04, -1673.96) * mm, "end": v(429.76, -1643.48) * mm});
            skLineSegment(sketch, "E317", {"start": v(405.37, -1603.1) * mm, "end": v(448.8, -1573.88) * mm});
            skLineSegment(sketch, "E318", {"start": v(448.8, -1573.88) * mm, "end": v(475.48, -1613.25) * mm});
            skLineSegment(sketch, "E319", {"start": v(475.48, -1613.25) * mm, "end": v(429.76, -1643.48) * mm});
            skLineSegment(sketch, "E320", {"start": v(1166.36, 764.19) * mm, "end": v(1322.57, 594) * mm});
            skLineSegment(sketch, "E321", {"start": v(-1124.72, -1022.7) * mm, "end": v(-1094.24, -1076.04) * mm});
            skLineSegment(sketch, "E322", {"start": v(2477, -1467.2) * mm, "end": v(2413.75, -1548.23) * mm});
            skLineSegment(sketch, "E323", {"start": v(1659.12, -2106.01) * mm, "end": v(1593.08, -1999.33) * mm});
            skLineSegment(sketch, "E324", {"start": v(448.04, -1673.96) * mm, "end": v(493.26, -1645) * mm});
            skLineSegment(sketch, "E325", {"start": v(493.26, -1645) * mm, "end": v(509.77, -1669.13) * mm});
            skLineSegment(sketch, "E326", {"start": v(1024.12, -569.31) * mm, "end": v(1002.53, -584.55) * mm});
            skLineSegment(sketch, "E327", {"start": v(-29.22, -1827.88) * mm, "end": v(-129.04, -1808.83) * mm});
            skLineSegment(sketch, "E328", {"start": v(-129.04, -1808.83) * mm, "end": v(-186.2, -1712.31) * mm});
            skLineSegment(sketch, "E329", {"start": v(-186.2, -1712.31) * mm, "end": v(-174.76, -1647.54) * mm});
            skLineSegment(sketch, "E330", {"start": v(-761.5, -1759.3) * mm, "end": v(-702.07, -1721.45) * mm});
            skLineSegment(sketch, "E331", {"start": v(667.25, 341.28) * mm, "end": v(779, 229.52) * mm});
            skLineSegment(sketch, "E332", {"start": v(779, 229.52) * mm, "end": v(859.02, 146.97) * mm});
            skLineSegment(sketch, "E333", {"start": v(1099.55, -508.35) * mm, "end": v(1024.12, -428.34) * mm});
            skLineSegment(sketch, "E334", {"start": v(1024.12, -428.34) * mm, "end": v(1017.77, -424.53) * mm});
            skLineSegment(sketch, "E335", {"start": v(1017.77, -424.53) * mm, "end": v(1011.42, -419.45) * mm});
            skLineSegment(sketch, "E336", {"start": v(1011.42, -419.45) * mm, "end": v(1005.07, -415.64) * mm});
            skLineSegment(sketch, "E337", {"start": v(1005.07, -415.64) * mm, "end": v(998.72, -410.56) * mm});
            skLineSegment(sketch, "E338", {"start": v(998.72, -410.56) * mm, "end": v(991.1, -406.75) * mm});
            skLineSegment(sketch, "E339", {"start": v(991.1, -406.75) * mm, "end": v(984.75, -402.94) * mm});
            skLineSegment(sketch, "E340", {"start": v(984.75, -402.94) * mm, "end": v(977.13, -399.13) * mm});
            skLineSegment(sketch, "E341", {"start": v(977.13, -399.13) * mm, "end": v(960.62, -391.51) * mm});
            skLineSegment(sketch, "E342", {"start": v(960.62, -391.51) * mm, "end": v(954.27, -388.97) * mm});
            skLineSegment(sketch, "E343", {"start": v(954.27, -388.97) * mm, "end": v(946.65, -385.16) * mm});
            skLineSegment(sketch, "E344", {"start": v(946.65, -385.16) * mm, "end": v(939.03, -382.62) * mm});
            skLineSegment(sketch, "E345", {"start": v(939.03, -382.62) * mm, "end": v(931.4, -381.35) * mm});
            skLineSegment(sketch, "E346", {"start": v(931.4, -381.35) * mm, "end": v(923.79, -378.81) * mm});
            skLineSegment(sketch, "E347", {"start": v(923.79, -378.81) * mm, "end": v(908.55, -376.27) * mm});
            skLineSegment(sketch, "E348", {"start": v(908.55, -376.27) * mm, "end": v(902.2, -375) * mm});
            skLineSegment(sketch, "E349", {"start": v(902.2, -375) * mm, "end": v(892.04, -375) * mm});
            skLineSegment(sketch, "E350", {"start": v(489.45, -1825.34) * mm, "end": v(528.56, -1800.96) * mm});
            skLineSegment(sketch, "E351", {"start": v(2019.8, -1162.4) * mm, "end": v(2030.97, -1149.2) * mm});
            skLineSegment(sketch, "E352", {"start": v(-450.35, -1882.74) * mm, "end": v(-527.82, -1909.16) * mm});
            skLineSegment(sketch, "E353", {"start": v(-527.82, -1909.16) * mm, "end": v(-557.03, -1916.78) * mm});
            skLineSegment(sketch, "E354", {"start": v(-557.03, -1916.78) * mm, "end": v(-564.65, -1920.6) * mm});
            skLineSegment(sketch, "E355", {"start": v(-564.65, -1920.6) * mm, "end": v(-571, -1921.86) * mm});
            skLineSegment(sketch, "E356", {"start": v(-571, -1921.86) * mm, "end": v(-574.81, -1924.4) * mm});
            skLineSegment(sketch, "E357", {"start": v(-574.81, -1924.4) * mm, "end": v(-583.7, -1925.67) * mm});
            skLineSegment(sketch, "E358", {"start": v(-583.7, -1925.67) * mm, "end": v(-588.78, -1926.94) * mm});
            skLineSegment(sketch, "E359", {"start": v(-588.78, -1926.94) * mm, "end": v(-604.02, -1928.21) * mm});
            skLineSegment(sketch, "E360", {"start": v(-604.02, -1928.21) * mm, "end": v(-616.72, -1929.48) * mm});
            skLineSegment(sketch, "E361", {"start": v(-616.72, -1929.48) * mm, "end": v(-628.15, -1930.75) * mm});
            skLineSegment(sketch, "E362", {"start": v(-628.15, -1930.75) * mm, "end": v(-658.63, -1932.02) * mm});
            skLineSegment(sketch, "E363", {"start": v(-658.63, -1932.02) * mm, "end": v(-662.44, -1934.81) * mm});
            skLineSegment(sketch, "E364", {"start": v(1593.08, -1999.33) * mm, "end": v(1567.68, -2015.84) * mm});
            skLineSegment(sketch, "E365", {"start": v(1567.68, -2015.84) * mm, "end": v(1548.63, -1990.44) * mm});
            skLineSegment(sketch, "E366", {"start": v(1548.63, -1990.44) * mm, "end": v(1577.84, -1971.4) * mm});
            skLineSegment(sketch, "E367", {"start": v(928.87, -2511.14) * mm, "end": v(903.47, -2469.23) * mm});
            skLineSegment(sketch, "E368", {"start": v(967.98, -2486.76) * mm, "end": v(928.87, -2511.14) * mm});
            skLineSegment(sketch, "E369", {"start": v(-1333, -1685.39) * mm, "end": v(-1443.5, -1505.3) * mm});
            skLineSegment(sketch, "E370", {"start": v(-1443.5, -1505.3) * mm, "end": v(-1432.06, -1497.68) * mm});
            skLineSegment(sketch, "E371", {"start": v(-1432.06, -1497.68) * mm, "end": v(-1475.24, -1420.21) * mm});
            skLineSegment(sketch, "E372", {"start": v(695.44, -173.58) * mm, "end": v(660.9, -208.63) * mm});
            skLineSegment(sketch, "E373", {"start": v(660.9, -208.63) * mm, "end": v(271, -662.02) * mm});
            skLineSegment(sketch, "E374", {"start": v(271, -662.02) * mm, "end": v(203.7, -738.22) * mm});
            skLineSegment(sketch, "E375", {"start": v(203.7, -738.22) * mm, "end": v(150.36, -795.37) * mm});
            skLineSegment(sketch, "E376", {"start": v(150.36, -795.37) * mm, "end": v(124.96, -816.96) * mm});
            skLineSegment(sketch, "E377", {"start": v(124.96, -816.96) * mm, "end": v(105.9, -832.2) * mm});
            skLineSegment(sketch, "E378", {"start": v(105.9, -832.2) * mm, "end": v(75.43, -852.52) * mm});
            skLineSegment(sketch, "E379", {"start": v(75.43, -852.52) * mm, "end": v(55.1, -865.22) * mm});
            skLineSegment(sketch, "E380", {"start": v(55.1, -865.22) * mm, "end": v(1.77, -899.51) * mm});
            skLineSegment(sketch, "E381", {"start": v(1.77, -899.51) * mm, "end": v(-107.45, -968.1) * mm});
            skLineSegment(sketch, "E382", {"start": v(-107.45, -968.1) * mm, "end": v(-256.04, -1059.53) * mm});
            skLineSegment(sketch, "E383", {"start": v(-256.04, -1059.53) * mm, "end": v(-395.74, -1148.43) * mm});
            skLineSegment(sketch, "E384", {"start": v(-395.74, -1148.43) * mm, "end": v(-534.17, -1238.6) * mm});
            skLineSegment(sketch, "E385", {"start": v(-534.17, -1238.6) * mm, "end": v(-675.14, -1328.77) * mm});
            skLineSegment(sketch, "E386", {"start": v(-675.14, -1328.77) * mm, "end": v(-852.94, -1448.15) * mm});
            skLineSegment(sketch, "E387", {"start": v(-852.94, -1448.15) * mm, "end": v(-1016.77, -1558.64) * mm});
            skLineSegment(sketch, "E388", {"start": v(-1016.77, -1558.64) * mm, "end": v(-1159.01, -1648.81) * mm});
            skLineSegment(sketch, "E389", {"start": v(-1159.01, -1648.81) * mm, "end": v(-1277.12, -1730.1) * mm});
            skLineSegment(sketch, "E390", {"start": v(-1277.12, -1730.1) * mm, "end": v(-1349.51, -1779.62) * mm});
            skLineSegment(sketch, "E391", {"start": v(-1349.51, -1779.62) * mm, "end": v(-1425.71, -1821.53) * mm});
            skLineSegment(sketch, "E392", {"start": v(-1425.71, -1821.53) * mm, "end": v(-1490.48, -1859.63) * mm});
            skLineSegment(sketch, "E393", {"start": v(-1490.48, -1859.63) * mm, "end": v(-1538.74, -1885.03) * mm});
            skLineSegment(sketch, "E394", {"start": v(-1538.74, -1885.03) * mm, "end": v(-1617.48, -1923.13) * mm});
            skLineSegment(sketch, "E395", {"start": v(-1617.48, -1923.13) * mm, "end": v(-1710.2, -1967.58) * mm});
            skLineSegment(sketch, "E396", {"start": v(-1710.2, -1967.58) * mm, "end": v(-1801.63, -2009.5) * mm});
            skLineSegment(sketch, "E397", {"start": v(-1801.63, -2009.5) * mm, "end": v(-1815.6, -2017.11) * mm});
            skLineSegment(sketch, "E398", {"start": v(-1815.6, -2017.11) * mm, "end": v(-1825.76, -2020.92) * mm});
            skLineSegment(sketch, "E399", {"start": v(-1825.76, -2020.92) * mm, "end": v(-1837.2, -2023.46) * mm});
            skLineSegment(sketch, "E400", {"start": v(-1837.2, -2023.46) * mm, "end": v(-1847.35, -2026) * mm});
            skLineSegment(sketch, "E401", {"start": v(-1847.35, -2026) * mm, "end": v(-1867.67, -2028.54) * mm});
            skLineSegment(sketch, "E402", {"start": v(-1867.67, -2028.54) * mm, "end": v(-1879.1, -2027.27) * mm});
            skLineSegment(sketch, "E403", {"start": v(1082.54, 856.9) * mm, "end": v(1191.76, 950.88) * mm});
            skLineSegment(sketch, "E404", {"start": v(1191.76, 950.88) * mm, "end": v(1185.4, 963.58) * mm});
            skLineSegment(sketch, "E405", {"start": v(1185.4, 963.58) * mm, "end": v(1217.16, 994.06) * mm});
            skLineSegment(sketch, "E406", {"start": v(-618, -1277.97) * mm, "end": v(-233.18, -1032.86) * mm});
            skLineSegment(sketch, "E407", {"start": v(1454.9, 719.49) * mm, "end": v(1558.79, 814.23) * mm});
            skLineSegment(sketch, "E408", {"start": v(-1376.18, -1365.6) * mm, "end": v(-1239.02, -1290.67) * mm});
            skLineSegment(sketch, "E409", {"start": v(2153.15, -1162.4) * mm, "end": v(2230.62, -1228.44) * mm});
            skLineSegment(sketch, "E410", {"start": v(1824.47, 1533.8) * mm, "end": v(1756.9, 1493.17) * mm});
            skLineSegment(sketch, "E411", {"start": v(307.84, -1049.37) * mm, "end": v(325.62, -1036.42) * mm});
            skLineSegment(sketch, "E412", {"start": v(-1630.18, -1782.16) * mm, "end": v(-1735.6, -1544.67) * mm});
            skLineSegment(sketch, "E413", {"start": v(271, -1471.01) * mm, "end": v(301.74, -1450.94) * mm});
            skLineSegment(sketch, "E414", {"start": v(-1950.22, -1732.63) * mm, "end": v(-2013.72, -1763.11) * mm});
            skLineSegment(sketch, "E415", {"start": v(-2013.72, -1763.11) * mm, "end": v(-1921.01, -1972.66) * mm});
            skLineSegment(sketch, "E416", {"start": v(-1921.01, -1972.66) * mm, "end": v(-1606.05, -1835.5) * mm});
            skLineSegment(sketch, "E417", {"start": v(859.02, 146.97) * mm, "end": v(1098.28, 375.06) * mm});
            skLineSegment(sketch, "E418", {"start": v(1983.47, 1123.1) * mm, "end": v(1975.35, 1115.98) * mm});
            skLineSegment(sketch, "E419", {"start": v(1975.35, 1115.98) * mm, "end": v(1919.47, 1057.56) * mm});
            skLineSegment(sketch, "E420", {"start": v(1919.47, 1057.56) * mm, "end": v(1287, 420.02) * mm});
            skLineSegment(sketch, "E421", {"start": v(1287, 420.02) * mm, "end": v(1267.96, 406.05) * mm});
            skLineSegment(sketch, "E422", {"start": v(1267.96, 406.05) * mm, "end": v(1207, 345.09) * mm});
            skLineSegment(sketch, "E423", {"start": v(1207, 345.09) * mm, "end": v(895.85, 29.37) * mm});
            skLineSegment(sketch, "E424", {"start": v(331.46, -1487.27) * mm, "end": v(296.4, -1510.38) * mm});
            skLineSegment(sketch, "E425", {"start": v(-2243.6, -1578.96) * mm, "end": v(-2260.1, -1542.13) * mm});
            skLineSegment(sketch, "E426", {"start": v(750.3, -2140.8) * mm, "end": v(805.68, -2227.42) * mm});
            skLineSegment(sketch, "E427", {"start": v(1221.73, -386.68) * mm, "end": v(1314.95, -485.5) * mm});
            skLineSegment(sketch, "E428", {"start": v(1314.95, -485.5) * mm, "end": v(1357.1, -470) * mm});
            skLineSegment(sketch, "E429", {"start": v(1783.58, 1291.5) * mm, "end": v(1817.1, 1323.5) * mm});
            skLineSegment(sketch, "E430", {"start": v(1513.07, -1001.11) * mm, "end": v(1488.94, -979.52) * mm});
            skLineSegment(sketch, "E431", {"start": v(3122.16, 1062.64) * mm, "end": v(3127.24, 1060.1) * mm});
            skLineSegment(sketch, "E432", {"start": v(3127.24, 1060.1) * mm, "end": v(3145.02, 1052.48) * mm});
            skLineSegment(sketch, "E433", {"start": v(3145.02, 1052.48) * mm, "end": v(3161.53, 1052.48) * mm});
            skLineSegment(sketch, "E434", {"start": v(3161.53, 1052.48) * mm, "end": v(3169.15, 1053.75) * mm});
            skLineSegment(sketch, "E435", {"start": v(3169.15, 1053.75) * mm, "end": v(3172.96, 1055.02) * mm});
            skLineSegment(sketch, "E436", {"start": v(3172.96, 1055.02) * mm, "end": v(3179.3, 1057.56) * mm});
            skLineSegment(sketch, "E437", {"start": v(3179.3, 1057.56) * mm, "end": v(3188.73, 1061.93) * mm});
            skLineSegment(sketch, "E438", {"start": v(2940.8, 1482.25) * mm, "end": v(2965.95, 1463.96) * mm});
            skLineSegment(sketch, "E439", {"start": v(2965.95, 1463.96) * mm, "end": v(2931.66, 1416.97) * mm});
            skLineSegment(sketch, "E440", {"start": v(-1339.1, 2414.94) * mm, "end": v(-1307.6, 2565.05) * mm});
            skLineSegment(sketch, "E441", {"start": v(-1307.6, 2565.05) * mm, "end": v(-1305.06, 2572.67) * mm});
            skLineSegment(sketch, "E442", {"start": v(-1305.06, 2572.67) * mm, "end": v(-1302.52, 2576.48) * mm});
            skLineSegment(sketch, "E443", {"start": v(-1302.52, 2576.48) * mm, "end": v(-1301.25, 2581.56) * mm});
            skLineSegment(sketch, "E444", {"start": v(-1301.25, 2581.56) * mm, "end": v(-1298.71, 2582.83) * mm});
            skLineSegment(sketch, "E445", {"start": v(-1298.71, 2582.83) * mm, "end": v(-1297.44, 2586.64) * mm});
            skLineSegment(sketch, "E446", {"start": v(-1297.44, 2586.64) * mm, "end": v(-1294.9, 2591.72) * mm});
            skLineSegment(sketch, "E447", {"start": v(-1294.9, 2591.72) * mm, "end": v(-1292.36, 2595.53) * mm});
            skLineSegment(sketch, "E448", {"start": v(-1292.36, 2595.53) * mm, "end": v(-1289.82, 2596.8) * mm});
            skLineSegment(sketch, "E449", {"start": v(-1289.82, 2596.8) * mm, "end": v(-1287.28, 2601.88) * mm});
            skLineSegment(sketch, "E450", {"start": v(-1287.28, 2601.88) * mm, "end": v(-1283.47, 2605.69) * mm});
            skLineSegment(sketch, "E451", {"start": v(-1283.47, 2605.69) * mm, "end": v(-1280.93, 2606.96) * mm});
            skLineSegment(sketch, "E452", {"start": v(-1280.93, 2606.96) * mm, "end": v(-1277.12, 2612.04) * mm});
            skLineSegment(sketch, "E453", {"start": v(-1277.12, 2612.04) * mm, "end": v(-1274.58, 2613.3) * mm});
            skLineSegment(sketch, "E454", {"start": v(-1274.58, 2613.3) * mm, "end": v(-1268.23, 2619.66) * mm});
            skLineSegment(sketch, "E455", {"start": v(-1268.23, 2619.66) * mm, "end": v(-1264.42, 2622.2) * mm});
            skLineSegment(sketch, "E456", {"start": v(-1264.42, 2622.2) * mm, "end": v(-1256.8, 2626) * mm});
            skLineSegment(sketch, "E457", {"start": v(-1256.8, 2626) * mm, "end": v(-1253, 2627.28) * mm});
            skLineSegment(sketch, "E458", {"start": v(-1253, 2627.28) * mm, "end": v(-1250.45, 2629.82) * mm});
            skLineSegment(sketch, "E459", {"start": v(-1250.45, 2629.82) * mm, "end": v(-1246.64, 2629.82) * mm});
            skLineSegment(sketch, "E460", {"start": v(-1246.64, 2629.82) * mm, "end": v(-1241.56, 2632.36) * mm});
            skLineSegment(sketch, "E461", {"start": v(-1241.56, 2632.36) * mm, "end": v(-1237.75, 2633.63) * mm});
            skLineSegment(sketch, "E462", {"start": v(-1237.75, 2633.63) * mm, "end": v(-1233.94, 2633.63) * mm});
            skLineSegment(sketch, "E463", {"start": v(-1233.94, 2633.63) * mm, "end": v(-1230.13, 2636.17) * mm});
            skLineSegment(sketch, "E464", {"start": v(-1230.13, 2636.17) * mm, "end": v(-1226.32, 2637.44) * mm});
            skLineSegment(sketch, "E465", {"start": v(-1226.32, 2637.44) * mm, "end": v(-1216.16, 2637.44) * mm});
            skLineSegment(sketch, "E466", {"start": v(-1216.16, 2637.44) * mm, "end": v(-1212.35, 2639.98) * mm});
            skLineSegment(sketch, "E467", {"start": v(-1212.35, 2639.98) * mm, "end": v(-1187.2, 2639.98) * mm});
            skLineSegment(sketch, "E468", {"start": v(-1556.52, -1448.15) * mm, "end": v(-1485.4, -1410.05) * mm});
            skLineSegment(sketch, "E469", {"start": v(-1235.72, 2391.82) * mm, "end": v(-1100.6, 2473.6) * mm});
            skLineSegment(sketch, "E470", {"start": v(2076.95, -1152.24) * mm, "end": v(2049, -1128.11) * mm});
            skLineSegment(sketch, "E471", {"start": v(1063.49, -531.21) * mm, "end": v(1120.13, -590.14) * mm});
            skLineSegment(sketch, "E472", {"start": v(2235.7, -1189.07) * mm, "end": v(2230.62, -1228.19) * mm});
            skLineSegment(sketch, "E473", {"start": v(-2152.66, -2403.2) * mm, "end": v(-2112.78, -2398.11) * mm});
            skLineSegment(sketch, "E474", {"start": v(-2112.78, -2398.11) * mm, "end": v(-2034.04, -2390.5) * mm});
            skLineSegment(sketch, "E475", {"start": v(-2034.04, -2390.5) * mm, "end": v(-2008.64, -2403.2) * mm});
            skLineSegment(sketch, "E476", {"start": v(-2008.64, -2403.2) * mm, "end": v(-1967.75, -2573.12) * mm});
            skLineSegment(sketch, "E477", {"start": v(-29.22, -1827.88) * mm, "end": v(-28.97, -1826.86) * mm});
            skLineSegment(sketch, "E478", {"start": v(-28.97, -1826.86) * mm, "end": v(-3.31, -1722.47) * mm});
            skLineSegment(sketch, "E479", {"start": v(-3.31, -1722.47) * mm, "end": v(-57.92, -1631.03) * mm});
            skLineSegment(sketch, "E480", {"start": v(-57.92, -1631.03) * mm, "end": v(-163.33, -1610.71) * mm});
            skLineSegment(sketch, "E481", {"start": v(-163.33, -1610.71) * mm, "end": v(-174.76, -1647.54) * mm});
            skLineSegment(sketch, "E482", {"start": v(-2170.19, -2404.46) * mm, "end": v(-2152.66, -2403.2) * mm});
            skLineSegment(sketch, "E483", {"start": v(-331.74, -1834.48) * mm, "end": v(-333.51, -1843.12) * mm});
            skLineSegment(sketch, "E484", {"start": v(-333.51, -1843.12) * mm, "end": v(-450.35, -1882.74) * mm});
            skLineSegment(sketch, "E485", {"start": v(-29.22, -1827.88) * mm, "end": v(-1.03, -1807.3) * mm});
            skLineSegment(sketch, "E486", {"start": v(-1.03, -1807.3) * mm, "end": v(-0.75, -1806.3) * mm});
            skLineSegment(sketch, "E487", {"start": v(-0.75, -1806.3) * mm, "end": v(9.39, -1768.2) * mm});
            skLineSegment(sketch, "E488", {"start": v(9.39, -1768.2) * mm, "end": v(43.68, -1774.54) * mm});
            skLineSegment(sketch, "E489", {"start": v(43.68, -1774.54) * mm, "end": v(37.33, -1793.6) * mm});
            skLineSegment(sketch, "E490", {"start": v(37.33, -1793.6) * mm, "end": v(178.04, -2013.8) * mm});
            skLineSegment(sketch, "E491", {"start": v(-1270.52, 2399.7) * mm, "end": v(-1235.21, 2546) * mm});
            skLineSegment(sketch, "E492", {"start": v(-1235.21, 2546) * mm, "end": v(-1232.67, 2551.08) * mm});
            skLineSegment(sketch, "E493", {"start": v(-1232.67, 2551.08) * mm, "end": v(-1231.4, 2554.89) * mm});
            skLineSegment(sketch, "E494", {"start": v(-1231.4, 2554.89) * mm, "end": v(-1228.86, 2558.7) * mm});
            skLineSegment(sketch, "E495", {"start": v(-1228.86, 2558.7) * mm, "end": v(-1226.32, 2561.24) * mm});
            skLineSegment(sketch, "E496", {"start": v(-1226.32, 2561.24) * mm, "end": v(-1225.05, 2565.05) * mm});
            skLineSegment(sketch, "E497", {"start": v(-1225.05, 2565.05) * mm, "end": v(-1222.51, 2566.32) * mm});
            skLineSegment(sketch, "E498", {"start": v(-1222.51, 2566.32) * mm, "end": v(-1218.7, 2568.86) * mm});
            skLineSegment(sketch, "E499", {"start": v(-1218.7, 2568.86) * mm, "end": v(-1216.16, 2571.4) * mm});
            skLineSegment(sketch, "E500", {"start": v(-1216.16, 2571.4) * mm, "end": v(-1212.35, 2572.67) * mm});
            skLineSegment(sketch, "E501", {"start": v(-1212.35, 2572.67) * mm, "end": v(-1207.27, 2575.2) * mm});
            skLineSegment(sketch, "E502", {"start": v(-1207.27, 2575.2) * mm, "end": v(-1199.9, 2575.2) * mm});
            skLineSegment(sketch, "E503", {"start": v(-1842.27, 2134.52) * mm, "end": v(-1714, 2217.07) * mm});
            skLineSegment(sketch, "E504", {"start": v(-1316.5, 2409.86) * mm, "end": v(-1286.01, 2552.35) * mm});
            skLineSegment(sketch, "E505", {"start": v(-1286.01, 2552.35) * mm, "end": v(-1284.74, 2556.16) * mm});
            skLineSegment(sketch, "E506", {"start": v(-1284.74, 2556.16) * mm, "end": v(-1282.2, 2558.7) * mm});
            skLineSegment(sketch, "E507", {"start": v(-1282.2, 2558.7) * mm, "end": v(-1282.2, 2562.5) * mm});
            skLineSegment(sketch, "E508", {"start": v(-1282.2, 2562.5) * mm, "end": v(-1279.66, 2566.32) * mm});
            skLineSegment(sketch, "E509", {"start": v(-1279.66, 2566.32) * mm, "end": v(-1277.12, 2571.4) * mm});
            skLineSegment(sketch, "E510", {"start": v(-1277.12, 2571.4) * mm, "end": v(-1273.31, 2576.48) * mm});
            skLineSegment(sketch, "E511", {"start": v(-1273.31, 2576.48) * mm, "end": v(-1270.77, 2581.56) * mm});
            skLineSegment(sketch, "E512", {"start": v(-1270.77, 2581.56) * mm, "end": v(-1268.23, 2582.83) * mm});
            skLineSegment(sketch, "E513", {"start": v(-1268.23, 2582.83) * mm, "end": v(-1266.96, 2586.64) * mm});
            skLineSegment(sketch, "E514", {"start": v(-1266.96, 2586.64) * mm, "end": v(-1263.15, 2589.18) * mm});
            skLineSegment(sketch, "E515", {"start": v(-1263.15, 2589.18) * mm, "end": v(-1256.8, 2595.53) * mm});
            skLineSegment(sketch, "E516", {"start": v(-1256.8, 2595.53) * mm, "end": v(-1253, 2596.8) * mm});
            skLineSegment(sketch, "E517", {"start": v(-1253, 2596.8) * mm, "end": v(-1244.1, 2605.69) * mm});
            skLineSegment(sketch, "E518", {"start": v(-1244.1, 2605.69) * mm, "end": v(-1240.3, 2606.96) * mm});
            skLineSegment(sketch, "E519", {"start": v(-1240.3, 2606.96) * mm, "end": v(-1236.48, 2609.5) * mm});
            skLineSegment(sketch, "E520", {"start": v(-1236.48, 2609.5) * mm, "end": v(-1230.13, 2612.04) * mm});
            skLineSegment(sketch, "E521", {"start": v(-1230.13, 2612.04) * mm, "end": v(-1226.32, 2613.3) * mm});
            skLineSegment(sketch, "E522", {"start": v(-1226.32, 2613.3) * mm, "end": v(-1221.24, 2615.85) * mm});
            skLineSegment(sketch, "E523", {"start": v(-1221.24, 2615.85) * mm, "end": v(-1217.43, 2615.85) * mm});
            skLineSegment(sketch, "E524", {"start": v(-1217.43, 2615.85) * mm, "end": v(-1213.62, 2617.12) * mm});
            skLineSegment(sketch, "E525", {"start": v(-1213.62, 2617.12) * mm, "end": v(-1202.2, 2617.12) * mm});
            skLineSegment(sketch, "E526", {"start": v(-1202.2, 2617.12) * mm, "end": v(-1198.38, 2619.66) * mm});
            skLineSegment(sketch, "E527", {"start": v(-1198.38, 2619.66) * mm, "end": v(-1191.02, 2619.66) * mm});
            skLineSegment(sketch, "E528", {"start": v(2797.04, -1879.95) * mm, "end": v(2658.6, -1763.11) * mm});
            skLineSegment(sketch, "E529", {"start": v(149.09, 2253.9) * mm, "end": v(132.58, 2173.38) * mm});
            skLineSegment(sketch, "E530", {"start": v(-2439.17, -2440.02) * mm, "end": v(-2170.19, -2404.46) * mm});
            skLineSegment(sketch, "E531", {"start": v(1024.12, -569.31) * mm, "end": v(1039.6, -554.32) * mm});
            skLineSegment(sketch, "E532", {"start": v(1039.6, -554.32) * mm, "end": v(1063.49, -531.21) * mm});
            skLineSegment(sketch, "E533", {"start": v(1061.2, -643.22) * mm, "end": v(1147.56, -732.89) * mm});
            skLineSegment(sketch, "E534", {"start": v(-2170.19, -2404.46) * mm, "end": v(-2161.55, -2500.73) * mm});
            skLineSegment(sketch, "E535", {"start": v(-1779.03, -2280.76) * mm, "end": v(-1781.57, -2286.1) * mm});
            skLineSegment(sketch, "E536", {"start": v(504.69, -249.27) * mm, "end": v(518.66, -256.9) * mm});
            skLineSegment(sketch, "E537", {"start": v(518.66, -256.9) * mm, "end": v(602.48, -152.24) * mm});
            skLineSegment(sketch, "E538", {"start": v(823.46, -629) * mm, "end": v(756.15, -561.7) * mm});
            skLineSegment(sketch, "E539", {"start": v(-1773.7, -2450.18) * mm, "end": v(-1777.5, -2424.78) * mm});
            skLineSegment(sketch, "E540", {"start": v(-1777.5, -2424.78) * mm, "end": v(-1778.77, -2410.81) * mm});
            skLineSegment(sketch, "E541", {"start": v(-1778.77, -2410.81) * mm, "end": v(-1778.77, -2399.38) * mm});
            skLineSegment(sketch, "E542", {"start": v(-1778.77, -2399.38) * mm, "end": v(-1776.23, -2380.33) * mm});
            skLineSegment(sketch, "E543", {"start": v(-1776.23, -2380.33) * mm, "end": v(-1766.07, -2365.1) * mm});
            skLineSegment(sketch, "E544", {"start": v(-1766.07, -2365.1) * mm, "end": v(-1753.37, -2352.4) * mm});
            skLineSegment(sketch, "E545", {"start": v(-1753.37, -2352.4) * mm, "end": v(-1739.4, -2342.23) * mm});
            skLineSegment(sketch, "E546", {"start": v(-1739.4, -2342.23) * mm, "end": v(-1731.78, -2335.88) * mm});
            skLineSegment(sketch, "E547", {"start": v(-1731.78, -2335.88) * mm, "end": v(-991.88, -1867.5) * mm});
            skLineSegment(sketch, "E548", {"start": v(-1932.44, -2323.69) * mm, "end": v(-1933.46, -2322.67) * mm});
            skLineSegment(sketch, "E549", {"start": v(-1933.46, -2322.67) * mm, "end": v(-1935.75, -2320.64) * mm});
            skLineSegment(sketch, "E550", {"start": v(-1935.75, -2320.64) * mm, "end": v(-1938.03, -2318.86) * mm});
            skLineSegment(sketch, "E551", {"start": v(-1938.03, -2318.86) * mm, "end": v(-1940.32, -2317.34) * mm});
            skLineSegment(sketch, "E552", {"start": v(-1940.32, -2317.34) * mm, "end": v(-1942.6, -2315.56) * mm});
            skLineSegment(sketch, "E553", {"start": v(-1942.6, -2315.56) * mm, "end": v(-1945.14, -2314.3) * mm});
            skLineSegment(sketch, "E554", {"start": v(-1945.14, -2314.3) * mm, "end": v(-1949.2, -2312) * mm});
            skLineSegment(sketch, "E555", {"start": v(-1949.2, -2312) * mm, "end": v(-1951.75, -2310.99) * mm});
            skLineSegment(sketch, "E556", {"start": v(-1951.75, -2310.99) * mm, "end": v(-1954.29, -2309.72) * mm});
            skLineSegment(sketch, "E557", {"start": v(-1954.29, -2309.72) * mm, "end": v(-1957.08, -2308.96) * mm});
            skLineSegment(sketch, "E558", {"start": v(-1957.08, -2308.96) * mm, "end": v(-1959.88, -2307.94) * mm});
            skLineSegment(sketch, "E559", {"start": v(-1959.88, -2307.94) * mm, "end": v(-1962.67, -2307.18) * mm});
            skLineSegment(sketch, "E560", {"start": v(-1962.67, -2307.18) * mm, "end": v(-1965.46, -2306.67) * mm});
            skLineSegment(sketch, "E561", {"start": v(-1965.46, -2306.67) * mm, "end": v(-1968.26, -2306.16) * mm});
            skLineSegment(sketch, "E562", {"start": v(-1968.26, -2306.16) * mm, "end": v(-1971.05, -2305.65) * mm});
            skLineSegment(sketch, "E563", {"start": v(-1971.05, -2305.65) * mm, "end": v(-1973.85, -2305.4) * mm});
            skLineSegment(sketch, "E564", {"start": v(-1973.85, -2305.4) * mm, "end": v(-1976.9, -2305.4) * mm});
            skLineSegment(sketch, "E565", {"start": v(-1976.9, -2305.4) * mm, "end": v(-1979.69, -2305.15) * mm});
            skLineSegment(sketch, "E566", {"start": v(-1979.69, -2305.15) * mm, "end": v(-1982.48, -2305.4) * mm});
            skLineSegment(sketch, "E567", {"start": v(-1982.48, -2305.4) * mm, "end": v(-1985.53, -2305.4) * mm});
            skLineSegment(sketch, "E568", {"start": v(-1985.53, -2305.4) * mm, "end": v(-1988.32, -2305.9) * mm});
            skLineSegment(sketch, "E569", {"start": v(-1988.32, -2305.9) * mm, "end": v(-1991.12, -2306.16) * mm});
            skLineSegment(sketch, "E570", {"start": v(-1991.12, -2306.16) * mm, "end": v(-1993.91, -2306.92) * mm});
            skLineSegment(sketch, "E571", {"start": v(-1993.91, -2306.92) * mm, "end": v(-1999.5, -2307.69) * mm});
            skLineSegment(sketch, "E572", {"start": v(1869.94, 1561.24) * mm, "end": v(1824.47, 1533.8) * mm});
            skLineSegment(sketch, "E573", {"start": v(-527.82, -1909.16) * mm, "end": v(-553.22, -1838.04) * mm});
            skLineSegment(sketch, "E574", {"start": v(808.22, -613.76) * mm, "end": v(888.23, -533.75) * mm});
            skLineSegment(sketch, "E575", {"start": v(888.23, -533.75) * mm, "end": v(889.5, -531.21) * mm});
            skLineSegment(sketch, "E576", {"start": v(889.5, -531.21) * mm, "end": v(893.3, -528.67) * mm});
            skLineSegment(sketch, "E577", {"start": v(893.3, -528.67) * mm, "end": v(898.39, -523.6) * mm});
            skLineSegment(sketch, "E578", {"start": v(898.39, -523.6) * mm, "end": v(900.93, -522.32) * mm});
            skLineSegment(sketch, "E579", {"start": v(900.93, -522.32) * mm, "end": v(903.47, -519.78) * mm});
            skLineSegment(sketch, "E580", {"start": v(903.47, -519.78) * mm, "end": v(906, -518.51) * mm});
            skLineSegment(sketch, "E581", {"start": v(906, -518.51) * mm, "end": v(908.55, -515.97) * mm});
            skLineSegment(sketch, "E582", {"start": v(908.55, -515.97) * mm, "end": v(913.63, -513.43) * mm});
            skLineSegment(sketch, "E583", {"start": v(913.63, -513.43) * mm, "end": v(917.44, -512.16) * mm});
            skLineSegment(sketch, "E584", {"start": v(917.44, -512.16) * mm, "end": v(919.98, -510.9) * mm});
            skLineSegment(sketch, "E585", {"start": v(919.98, -510.9) * mm, "end": v(939.03, -507.08) * mm});
            skLineSegment(sketch, "E586", {"start": v(939.03, -507.08) * mm, "end": v(960.62, -507.08) * mm});
            skLineSegment(sketch, "E587", {"start": v(960.62, -507.08) * mm, "end": v(963.16, -508.35) * mm});
            skLineSegment(sketch, "E588", {"start": v(963.16, -508.35) * mm, "end": v(966.97, -508.35) * mm});
            skLineSegment(sketch, "E589", {"start": v(966.97, -508.35) * mm, "end": v(974.59, -510.9) * mm});
            skLineSegment(sketch, "E590", {"start": v(974.59, -510.9) * mm, "end": v(979.67, -512.16) * mm});
            skLineSegment(sketch, "E591", {"start": v(979.67, -512.16) * mm, "end": v(987.29, -514.7) * mm});
            skLineSegment(sketch, "E592", {"start": v(987.29, -514.7) * mm, "end": v(989.83, -515.97) * mm});
            skLineSegment(sketch, "E593", {"start": v(989.83, -515.97) * mm, "end": v(993.64, -518.51) * mm});
            skLineSegment(sketch, "E594", {"start": v(993.64, -518.51) * mm, "end": v(997.45, -519.78) * mm});
            skLineSegment(sketch, "E595", {"start": v(997.45, -519.78) * mm, "end": v(1001.26, -522.32) * mm});
            skLineSegment(sketch, "E596", {"start": v(1001.26, -522.32) * mm, "end": v(1003.8, -523.6) * mm});
            skLineSegment(sketch, "E597", {"start": v(1003.8, -523.6) * mm, "end": v(1007.6, -526.13) * mm});
            skLineSegment(sketch, "E598", {"start": v(1007.6, -526.13) * mm, "end": v(1010.15, -528.67) * mm});
            skLineSegment(sketch, "E599", {"start": v(1010.15, -528.67) * mm, "end": v(1039.6, -554.32) * mm});
            skLineSegment(sketch, "E600", {"start": v(773.42, -578.96) * mm, "end": v(847.59, -500.73) * mm});
            skLineSegment(sketch, "E601", {"start": v(847.59, -500.73) * mm, "end": v(853.94, -494.38) * mm});
            skLineSegment(sketch, "E602", {"start": v(853.94, -494.38) * mm, "end": v(861.56, -488.03) * mm});
            skLineSegment(sketch, "E603", {"start": v(861.56, -488.03) * mm, "end": v(869.18, -482.95) * mm});
            skLineSegment(sketch, "E604", {"start": v(869.18, -482.95) * mm, "end": v(876.8, -479.14) * mm});
            skLineSegment(sketch, "E605", {"start": v(876.8, -479.14) * mm, "end": v(884.42, -472.8) * mm});
            skLineSegment(sketch, "E606", {"start": v(884.42, -472.8) * mm, "end": v(890.77, -470.25) * mm});
            skLineSegment(sketch, "E607", {"start": v(890.77, -470.25) * mm, "end": v(894.58, -467.71) * mm});
            skLineSegment(sketch, "E608", {"start": v(894.58, -467.71) * mm, "end": v(906, -463.9) * mm});
            skLineSegment(sketch, "E609", {"start": v(906, -463.9) * mm, "end": v(908.55, -462.63) * mm});
            skLineSegment(sketch, "E610", {"start": v(908.55, -462.63) * mm, "end": v(912.36, -462.63) * mm});
            skLineSegment(sketch, "E611", {"start": v(912.36, -462.63) * mm, "end": v(917.44, -461.36) * mm});
            skLineSegment(sketch, "E612", {"start": v(917.44, -461.36) * mm, "end": v(919.98, -460.1) * mm});
            skLineSegment(sketch, "E613", {"start": v(919.98, -460.1) * mm, "end": v(926.33, -458.82) * mm});
            skLineSegment(sketch, "E614", {"start": v(926.33, -458.82) * mm, "end": v(940.3, -458.82) * mm});
            skLineSegment(sketch, "E615", {"start": v(940.3, -458.82) * mm, "end": v(946.65, -460.1) * mm});
            skLineSegment(sketch, "E616", {"start": v(946.65, -460.1) * mm, "end": v(951.73, -461.36) * mm});
            skLineSegment(sketch, "E617", {"start": v(951.73, -461.36) * mm, "end": v(963.16, -462.63) * mm});
            skLineSegment(sketch, "E618", {"start": v(963.16, -462.63) * mm, "end": v(973.32, -465.17) * mm});
            skLineSegment(sketch, "E619", {"start": v(973.32, -465.17) * mm, "end": v(984.75, -468.98) * mm});
            skLineSegment(sketch, "E620", {"start": v(984.75, -468.98) * mm, "end": v(998.72, -470.25) * mm});
            skLineSegment(sketch, "E621", {"start": v(1765.29, 2284.63) * mm, "end": v(1788.66, 2247.55) * mm});
            skLineSegment(sketch, "E622", {"start": v(3059.93, -2358.74) * mm, "end": v(3155.94, -2445.35) * mm});
            skLineSegment(sketch, "E623", {"start": v(2797.04, -1879.95) * mm, "end": v(2780.53, -1924.4) * mm});
            skLineSegment(sketch, "E624", {"start": v(2780.53, -1924.4) * mm, "end": v(3155.68, -2247.49) * mm});
            skLineSegment(sketch, "E625", {"start": v(3033.26, -2334.61) * mm, "end": v(3059.93, -2358.74) * mm});
            skLineSegment(sketch, "E626", {"start": v(3155.68, -2247.49) * mm, "end": v(3059.93, -2358.74) * mm});
            skLineSegment(sketch, "E627", {"start": v(1709.92, -1196.7) * mm, "end": v(1715, -1187.8) * mm});
            skLineSegment(sketch, "E628", {"start": v(1715, -1187.8) * mm, "end": v(1716.27, -1185.26) * mm});
            skLineSegment(sketch, "E629", {"start": v(1716.27, -1185.26) * mm, "end": v(1716.27, -1181.45) * mm});
            skLineSegment(sketch, "E630", {"start": v(1716.27, -1181.45) * mm, "end": v(1717.54, -1176.37) * mm});
            skLineSegment(sketch, "E631", {"start": v(1717.54, -1176.37) * mm, "end": v(1717.54, -1159.86) * mm});
            skLineSegment(sketch, "E632", {"start": v(1717.54, -1159.86) * mm, "end": v(1716.27, -1157.32) * mm});
            skLineSegment(sketch, "E633", {"start": v(1716.27, -1157.32) * mm, "end": v(1713.73, -1154.78) * mm});
            skLineSegment(sketch, "E634", {"start": v(1713.73, -1154.78) * mm, "end": v(1712.46, -1152.24) * mm});
            skLineSegment(sketch, "E635", {"start": v(1712.46, -1152.24) * mm, "end": v(1708.65, -1143.35) * mm});
            skLineSegment(sketch, "E636", {"start": v(1708.65, -1143.35) * mm, "end": v(1704.84, -1139.54) * mm});
            skLineSegment(sketch, "E637", {"start": v(1704.84, -1139.54) * mm, "end": v(1646.92, -1082.64) * mm});
            skLineSegment(sketch, "E638", {"start": v(1732.78, -867.76) * mm, "end": v(1709.92, -904.6) * mm});
            skLineSegment(sketch, "E639", {"start": v(1709.92, -904.6) * mm, "end": v(1763.5, -962.5) * mm});
            skLineSegment(sketch, "E640", {"start": v(1763.5, -962.5) * mm, "end": v(1765.8, -965.04) * mm});
            skLineSegment(sketch, "E641", {"start": v(1646.92, -1082.64) * mm, "end": v(1765.8, -965.04) * mm});
            skLineSegment(sketch, "E642", {"start": v(1106.67, -176.88) * mm, "end": v(1106.67, -197.2) * mm});
            skLineSegment(sketch, "E643", {"start": v(1106.67, -197.2) * mm, "end": v(1107.94, -206.1) * mm});
            skLineSegment(sketch, "E644", {"start": v(1107.94, -206.1) * mm, "end": v(1109.2, -212.44) * mm});
            skLineSegment(sketch, "E645", {"start": v(1109.2, -212.44) * mm, "end": v(1109.2, -217.52) * mm});
            skLineSegment(sketch, "E646", {"start": v(1109.2, -217.52) * mm, "end": v(1110.48, -225.14) * mm});
            skLineSegment(sketch, "E647", {"start": v(1110.48, -225.14) * mm, "end": v(1113.02, -231.5) * mm});
            skLineSegment(sketch, "E648", {"start": v(1113.02, -231.5) * mm, "end": v(1115.56, -244.2) * mm});
            skLineSegment(sketch, "E649", {"start": v(1115.56, -244.2) * mm, "end": v(1118.1, -250.54) * mm});
            skLineSegment(sketch, "E650", {"start": v(1118.1, -250.54) * mm, "end": v(1119.37, -256.9) * mm});
            skLineSegment(sketch, "E651", {"start": v(1119.37, -256.9) * mm, "end": v(1121.9, -263.24) * mm});
            skLineSegment(sketch, "E652", {"start": v(1121.9, -263.24) * mm, "end": v(1125.72, -270.86) * mm});
            skLineSegment(sketch, "E653", {"start": v(1125.72, -270.86) * mm, "end": v(1129.53, -277.21) * mm});
            skLineSegment(sketch, "E654", {"start": v(1129.53, -277.21) * mm, "end": v(1132.07, -283.56) * mm});
            skLineSegment(sketch, "E655", {"start": v(1132.07, -283.56) * mm, "end": v(1139.69, -296.26) * mm});
            skLineSegment(sketch, "E656", {"start": v(1139.69, -296.26) * mm, "end": v(1143.5, -301.34) * mm});
            skLineSegment(sketch, "E657", {"start": v(1143.5, -301.34) * mm, "end": v(1147.3, -307.7) * mm});
            skLineSegment(sketch, "E658", {"start": v(1147.3, -307.7) * mm, "end": v(1152.39, -312.77) * mm});
            skLineSegment(sketch, "E659", {"start": v(1152.39, -312.77) * mm, "end": v(1156.2, -319.12) * mm});
            skLineSegment(sketch, "E660", {"start": v(1156.2, -319.12) * mm, "end": v(1161.28, -322.93) * mm});
            skLineSegment(sketch, "E661", {"start": v(1161.28, -322.93) * mm, "end": v(1166.36, -328.01) * mm});
            skLineSegment(sketch, "E662", {"start": v(1166.36, -328.01) * mm, "end": v(1219.44, -384.14) * mm});
            skLineSegment(sketch, "E663", {"start": v(1219.44, -384.14) * mm, "end": v(1221.73, -386.68) * mm});
            skLineSegment(sketch, "E664", {"start": v(1646.92, -1082.64) * mm, "end": v(1568.95, -1006.2) * mm});
            skLineSegment(sketch, "E665", {"start": v(1568.95, -1006.2) * mm, "end": v(1099.55, -508.35) * mm});
            skLineSegment(sketch, "E666", {"start": v(1099.55, -508.35) * mm, "end": v(1221.73, -386.68) * mm});
            skLineSegment(sketch, "E667", {"start": v(1067.3, -2640.43) * mm, "end": v(1029.2, -2666.08) * mm});
            skLineSegment(sketch, "E668", {"start": v(325.62, -1036.42) * mm, "end": v(544.06, -795.37) * mm});
            skLineSegment(sketch, "E669", {"start": v(544.06, -795.37) * mm, "end": v(692.65, -627.73) * mm});
            skLineSegment(sketch, "E670", {"start": v(692.65, -627.73) * mm, "end": v(756.15, -561.7) * mm});
            skLineSegment(sketch, "E671", {"start": v(1232.14, 1228) * mm, "end": v(1264.15, 1255.68) * mm});
            skLineSegment(sketch, "E672", {"start": v(1264.15, 1255.68) * mm, "end": v(1269.23, 1259.49) * mm});
            skLineSegment(sketch, "E673", {"start": v(-1117.61, -1222.6) * mm, "end": v(-977.15, -1461.36) * mm});
            skLineSegment(sketch, "E674", {"start": v(1120.13, -590.14) * mm, "end": v(1343.9, -826.87) * mm});
            skLineSegment(sketch, "E675", {"start": v(2572.25, -1357.98) * mm, "end": v(2477, -1467.2) * mm});
            skLineSegment(sketch, "E676", {"start": v(2171.18, -1141.32) * mm, "end": v(2146.54, -1169.77) * mm});
            skLineSegment(sketch, "E677", {"start": v(1453.88, -572.36) * mm, "end": v(1357.1, -470) * mm});
            skLineSegment(sketch, "E678", {"start": v(2019.8, -1162.4) * mm, "end": v(1995.67, -1192.88) * mm});
            skLineSegment(sketch, "E679", {"start": v(1995.67, -1192.88) * mm, "end": v(1990.59, -1199.23) * mm});
            skLineSegment(sketch, "E680", {"start": v(1990.59, -1199.23) * mm, "end": v(1985.5, -1206.85) * mm});
            skLineSegment(sketch, "E681", {"start": v(1985.5, -1206.85) * mm, "end": v(1982.97, -1213.2) * mm});
            skLineSegment(sketch, "E682", {"start": v(1982.97, -1213.2) * mm, "end": v(1982.97, -1222.1) * mm});
            skLineSegment(sketch, "E683", {"start": v(1982.97, -1222.1) * mm, "end": v(1985.5, -1227.17) * mm});
            skLineSegment(sketch, "E684", {"start": v(1985.5, -1227.17) * mm, "end": v(1988.05, -1229.71) * mm});
            skLineSegment(sketch, "E685", {"start": v(1988.05, -1229.71) * mm, "end": v(1999.48, -1244.95) * mm});
            skLineSegment(sketch, "E686", {"start": v(1999.48, -1244.95) * mm, "end": v(2012.18, -1256.38) * mm});
            skLineSegment(sketch, "E687", {"start": v(2012.18, -1256.38) * mm, "end": v(2140.45, -1370.68) * mm});
            skLineSegment(sketch, "E688", {"start": v(2140.45, -1370.68) * mm, "end": v(2600.19, -1763.11) * mm});
            skLineSegment(sketch, "E689", {"start": v(2600.19, -1763.11) * mm, "end": v(2658.6, -1763.11) * mm});
            skLineSegment(sketch, "E690", {"start": v(1147.56, -732.89) * mm, "end": v(1290.82, -881.73) * mm});
            skLineSegment(sketch, "E691", {"start": v(1217.16, 994.06) * mm, "end": v(1184.9, 1034.45) * mm});
            skLineSegment(sketch, "E692", {"start": v(1755.13, 1331.88) * mm, "end": v(1789.67, 1360.58) * mm});
            skLineSegment(sketch, "E693", {"start": v(1356.86, 1129.95) * mm, "end": v(1320.03, 1098.2) * mm});
            skLineSegment(sketch, "E694", {"start": v(1320.03, 1098.2) * mm, "end": v(1420.36, 978.82) * mm});
            skLineSegment(sketch, "E695", {"start": v(1420.36, 978.82) * mm, "end": v(1428.23, 985.42) * mm});
            skLineSegment(sketch, "E696", {"start": v(287.52, -49.88) * mm, "end": v(254.5, -19.4) * mm});
            skLineSegment(sketch, "E697", {"start": v(254.5, -19.4) * mm, "end": v(339.59, 78.39) * mm});
            skLineSegment(sketch, "E698", {"start": v(339.59, 78.39) * mm, "end": v(417.06, 11.08) * mm});
            skLineSegment(sketch, "E699", {"start": v(1029.2, -2666.08) * mm, "end": v(1001.26, -2624.17) * mm});
            skLineSegment(sketch, "E700", {"start": v(1755.13, 1331.88) * mm, "end": v(1763.26, 1319.18) * mm});
            skLineSegment(sketch, "E701", {"start": v(1763.26, 1319.18) * mm, "end": v(1783.58, 1291.5) * mm});
            skLineSegment(sketch, "E702", {"start": v(-883.68, -1798.16) * mm, "end": v(-877.33, -1794.35) * mm});
            skLineSegment(sketch, "E703", {"start": v(-877.33, -1794.35) * mm, "end": v(-795.8, -1741.52) * mm});
            skLineSegment(sketch, "E704", {"start": v(-795.8, -1741.52) * mm, "end": v(-767.85, -1738.98) * mm});
            skLineSegment(sketch, "E705", {"start": v(1356.86, 1129.95) * mm, "end": v(1454.14, 1007.27) * mm});
            skLineSegment(sketch, "E706", {"start": v(-718.32, -1695.8) * mm, "end": v(-702.07, -1721.45) * mm});
            skLineSegment(sketch, "E707", {"start": v(-702.07, -1721.45) * mm, "end": v(-700.54, -1723.74) * mm});
            skLineSegment(sketch, "E708", {"start": v(-700.54, -1723.74) * mm, "end": v(-685.56, -1748.12) * mm});
            skLineSegment(sketch, "E709", {"start": v(-685.56, -1748.12) * mm, "end": v(-637.04, -1826.61) * mm});
            skLineSegment(sketch, "E710", {"start": v(-637.04, -1826.61) * mm, "end": v(-634, -1827.63) * mm});
            skLineSegment(sketch, "E711", {"start": v(-634, -1827.63) * mm, "end": v(-576.08, -1847.44) * mm});
            skLineSegment(sketch, "E712", {"start": v(-576.08, -1847.44) * mm, "end": v(-573.54, -1848.2) * mm});
            skLineSegment(sketch, "E713", {"start": v(-573.54, -1848.2) * mm, "end": v(-553.22, -1838.04) * mm});
            skLineSegment(sketch, "E714", {"start": v(-553.22, -1838.04) * mm, "end": v(-474.48, -1811.37) * mm});
            skLineSegment(sketch, "E715", {"start": v(554.98, -1840.07) * mm, "end": v(514.85, -1864.71) * mm});
            skLineSegment(sketch, "E716", {"start": v(750.3, -2140.8) * mm, "end": v(790.44, -2114.9) * mm});
            skLineSegment(sketch, "E717", {"start": v(790.44, -2114.9) * mm, "end": v(758.69, -2066.64) * mm});
            skLineSegment(sketch, "E718", {"start": v(758.69, -2066.64) * mm, "end": v(719.57, -2092.3) * mm});
            skLineSegment(sketch, "E719", {"start": v(719.57, -2092.3) * mm, "end": v(677.4, -2119.98) * mm});
            skLineSegment(sketch, "E720", {"start": v(677.4, -2119.98) * mm, "end": v(707.89, -2168.24) * mm});
            skLineSegment(sketch, "E721", {"start": v(1901.69, -1053.18) * mm, "end": v(1732.78, -867.76) * mm});
            skLineSegment(sketch, "E722", {"start": v(2879.59, -744.57) * mm, "end": v(2813.55, -820.77) * mm});
            skLineSegment(sketch, "E723", {"start": v(2813.55, -820.77) * mm, "end": v(2884.67, -881.73) * mm});
            skLineSegment(sketch, "E724", {"start": v(2884.67, -881.73) * mm, "end": v(2793.23, -988.41) * mm});
            skLineSegment(sketch, "E725", {"start": v(2793.23, -988.41) * mm, "end": v(2731, -933.8) * mm});
            skLineSegment(sketch, "E726", {"start": v(2731, -933.8) * mm, "end": v(2510.02, -1186.53) * mm});
            skLineSegment(sketch, "E727", {"start": v(2510.02, -1186.53) * mm, "end": v(2579.87, -1247.5) * mm});
            skLineSegment(sketch, "E728", {"start": v(2579.87, -1247.5) * mm, "end": v(2521.45, -1314.8) * mm});
            skLineSegment(sketch, "E729", {"start": v(2521.45, -1314.8) * mm, "end": v(2572.25, -1357.98) * mm});
            skLineSegment(sketch, "E730", {"start": v(2863.58, 1786.03) * mm, "end": v(2885.94, 1772.57) * mm});
            skLineSegment(sketch, "E731", {"start": v(1031.99, 813.97) * mm, "end": v(1027.93, 818.8) * mm});
            skLineSegment(sketch, "E732", {"start": v(1027.93, 818.8) * mm, "end": v(912.36, 717.2) * mm});
            skLineSegment(sketch, "E733", {"start": v(912.36, 717.2) * mm, "end": v(979.67, 633.38) * mm});
            skLineSegment(sketch, "E734", {"start": v(979.67, 633.38) * mm, "end": v(1006.59, 606.46) * mm});
            skLineSegment(sketch, "E735", {"start": v(1869.94, 1561.24) * mm, "end": v(1881.37, 1541.43) * mm});
            skLineSegment(sketch, "E736", {"start": v(1509, 1296.32) * mm, "end": v(1400.8, 1461.42) * mm});
            skLineSegment(sketch, "E737", {"start": v(1400.8, 1461.42) * mm, "end": v(1352.54, 1426.11) * mm});
            skLineSegment(sketch, "E738", {"start": v(769.1, 700.94) * mm, "end": v(674.1, 658.02) * mm});
            skLineSegment(sketch, "E739", {"start": v(674.1, 658.02) * mm, "end": v(459.47, 508.92) * mm});
            skLineSegment(sketch, "E740", {"start": v(1581.65, 1108.61) * mm, "end": v(1700.52, 943.51) * mm});
            skLineSegment(sketch, "E741", {"start": v(1614.67, 1135.03) * mm, "end": v(1509, 1296.32) * mm});
            skLineSegment(sketch, "E742", {"start": v(1352.54, 1426.11) * mm, "end": v(1581.65, 1108.61) * mm});
            skLineSegment(sketch, "E743", {"start": v(146.55, -152.75) * mm, "end": v(126.23, -140.05) * mm});
            skLineSegment(sketch, "E744", {"start": v(126.23, -140.05) * mm, "end": v(144, -67.66) * mm});
            skLineSegment(sketch, "E745", {"start": v(1735.32, 975.52) * mm, "end": v(1614.67, 1135.03) * mm});
            skLineSegment(sketch, "E746", {"start": v(1706.87, 1486.06) * mm, "end": v(1707.38, 1486.82) * mm});
            skLineSegment(sketch, "E747", {"start": v(1707.38, 1486.82) * mm, "end": v(1745.48, 1508.4) * mm});
            skLineSegment(sketch, "E748", {"start": v(1745.48, 1508.4) * mm, "end": v(1858.5, 1580.8) * mm});
            skLineSegment(sketch, "E749", {"start": v(1858.5, 1580.8) * mm, "end": v(1869.94, 1561.24) * mm});
            skLineSegment(sketch, "E750", {"start": v(1789.67, 1360.58) * mm, "end": v(1817.1, 1323.5) * mm});
            skLineSegment(sketch, "E751", {"start": v(667.25, 341.28) * mm, "end": v(611.37, 394.62) * mm});
            skLineSegment(sketch, "E752", {"start": v(611.37, 394.62) * mm, "end": v(751.07, 539.4) * mm});
            skLineSegment(sketch, "E753", {"start": v(751.07, 539.4) * mm, "end": v(784.09, 505.1) * mm});
            skLineSegment(sketch, "E754", {"start": v(784.09, 505.1) * mm, "end": v(843.78, 560.99) * mm});
            skLineSegment(sketch, "E755", {"start": v(843.78, 560.99) * mm, "end": v(871.72, 533.05) * mm});
            skLineSegment(sketch, "E756", {"start": v(871.72, 533.05) * mm, "end": v(906, 568.6) * mm});
            skLineSegment(sketch, "E757", {"start": v(906, 568.6) * mm, "end": v(931.4, 536.86) * mm});
            skLineSegment(sketch, "E758", {"start": v(1031.99, 813.97) * mm, "end": v(1082.54, 856.9) * mm});
            skLineSegment(sketch, "E759", {"start": v(172.45, 2355.5) * mm, "end": v(149.09, 2253.9) * mm});
            skLineSegment(sketch, "E760", {"start": v(1990.59, 2165) * mm, "end": v(2205.22, 2233.58) * mm});
            skLineSegment(sketch, "E761", {"start": v(1788.66, 2247.55) * mm, "end": v(1895.34, 2078.64) * mm});
            skLineSegment(sketch, "E762", {"start": v(1895.34, 2078.64) * mm, "end": v(1918.2, 2139.6) * mm});
            skLineSegment(sketch, "E763", {"start": v(1918.2, 2139.6) * mm, "end": v(1990.59, 2165) * mm});
            skLineSegment(sketch, "E764", {"start": v(2008.37, 2107.85) * mm, "end": v(2223, 2178.97) * mm});
            skLineSegment(sketch, "E765", {"start": v(1928.36, 1174.4) * mm, "end": v(2383.02, 1550.32) * mm});
            skLineSegment(sketch, "E766", {"start": v(2383.02, 1550.32) * mm, "end": v(2404.6, 1602.39) * mm});
            skLineSegment(sketch, "E767", {"start": v(2404.6, 1602.39) * mm, "end": v(2301.74, 1928.78) * mm});
            skLineSegment(sketch, "E768", {"start": v(2301.74, 1928.78) * mm, "end": v(2223, 2178.97) * mm});
            skLineSegment(sketch, "E769", {"start": v(149.09, 2253.9) * mm, "end": v(98.29, 2266.6) * mm});
            skLineSegment(sketch, "E770", {"start": v(98.29, 2266.6) * mm, "end": v(74.16, 2159.92) * mm});
            skLineSegment(sketch, "E771", {"start": v(74.16, 2159.92) * mm, "end": v(127.5, 2148.49) * mm});
            skLineSegment(sketch, "E772", {"start": v(132.58, 2173.38) * mm, "end": v(127.5, 2148.49) * mm});
            skLineSegment(sketch, "E773", {"start": v(127.5, 2148.49) * mm, "end": v(187.19, 2135.79) * mm});
            skLineSegment(sketch, "E774", {"start": v(187.19, 2135.79) * mm, "end": v(149.09, 1928.78) * mm});
            skLineSegment(sketch, "E775", {"start": v(149.09, 1928.78) * mm, "end": v(130.04, 1833.53) * mm});
            skLineSegment(sketch, "E776", {"start": v(130.04, 1833.53) * mm, "end": v(196.08, 1819.56) * mm});
            skLineSegment(sketch, "E777", {"start": v(1509, 1296.32) * mm, "end": v(1699.5, 1416.72) * mm});
            skLineSegment(sketch, "E778", {"start": v(931.4, 536.86) * mm, "end": v(936.49, 541.94) * mm});
            skLineSegment(sketch, "E779", {"start": v(936.49, 541.94) * mm, "end": v(1006.59, 606.46) * mm});
            skLineSegment(sketch, "E780", {"start": v(1225.03, 1333.15) * mm, "end": v(1218.93, 1328.58) * mm});
            skLineSegment(sketch, "E781", {"start": v(1218.93, 1328.58) * mm, "end": v(1269.23, 1259.49) * mm});
            skLineSegment(sketch, "E782", {"start": v(1817.1, 1323.5) * mm, "end": v(1928.36, 1174.4) * mm});
            skLineSegment(sketch, "E783", {"start": v(1881.37, 1541.43) * mm, "end": v(1902.96, 1504.6) * mm});
            skLineSegment(sketch, "E784", {"start": v(1902.96, 1504.6) * mm, "end": v(1765.8, 1392.84) * mm});
            skLineSegment(sketch, "E785", {"start": v(1765.8, 1392.84) * mm, "end": v(1789.67, 1360.58) * mm});
            skLineSegment(sketch, "E786", {"start": v(1232.14, 1228) * mm, "end": v(1213.35, 1245.52) * mm});
            skLineSegment(sketch, "E787", {"start": v(1213.35, 1245.52) * mm, "end": v(1078.73, 1132.49) * mm});
            skLineSegment(sketch, "E788", {"start": v(1078.73, 1132.49) * mm, "end": v(1168.9, 1023.27) * mm});
            skLineSegment(sketch, "E789", {"start": v(1168.9, 1023.27) * mm, "end": v(1184.9, 1034.45) * mm});
            skLineSegment(sketch, "E790", {"start": v(1765.29, 2284.63) * mm, "end": v(1697.22, 2243.74) * mm});
            skLineSegment(sketch, "E791", {"start": v(1697.22, 2243.74) * mm, "end": v(1815.33, 2046.89) * mm});
            skLineSegment(sketch, "E792", {"start": v(718.55, 874.43) * mm, "end": v(707.89, 822.36) * mm});
            skLineSegment(sketch, "E793", {"start": v(784.34, 860.96) * mm, "end": v(797.8, 858.17) * mm});
            skLineSegment(sketch, "E794", {"start": v(797.8, 858.17) * mm, "end": v(915.15, 834.04) * mm});
            skLineSegment(sketch, "E795", {"start": v(915.15, 834.04) * mm, "end": v(935.72, 933.6) * mm});
            skLineSegment(sketch, "E796", {"start": v(310.88, 1843.44) * mm, "end": v(293.1, 1757.58) * mm});
            skLineSegment(sketch, "E797", {"start": v(293.1, 1757.58) * mm, "end": v(185.92, 1778.92) * mm});
            skLineSegment(sketch, "E798", {"start": v(185.92, 1778.92) * mm, "end": v(196.08, 1819.56) * mm});
            skLineSegment(sketch, "E799", {"start": v(196.08, 1819.56) * mm, "end": v(248.65, 1856.14) * mm});
            skLineSegment(sketch, "E800", {"start": v(248.65, 1856.14) * mm, "end": v(310.88, 1843.44) * mm});
            skLineSegment(sketch, "E801", {"start": v(1073.4, 1449.48) * mm, "end": v(1111.24, 1489.1) * mm});
            skLineSegment(sketch, "E802", {"start": v(1111.24, 1489.1) * mm, "end": v(1153.15, 1431.7) * mm});
            skLineSegment(sketch, "E803", {"start": v(1020.05, 1341.79) * mm, "end": v(1079.74, 1329.34) * mm});
            skLineSegment(sketch, "E804", {"start": v(1079.74, 1329.34) * mm, "end": v(1052.06, 1194.97) * mm});
            skLineSegment(sketch, "E805", {"start": v(903.47, 2355.5) * mm, "end": v(919.98, 2435) * mm});
            skLineSegment(sketch, "E806", {"start": v(919.98, 2435) * mm, "end": v(1013.2, 2415.95) * mm});
            skLineSegment(sketch, "E807", {"start": v(826.25, 2371.5) * mm, "end": v(903.47, 2355.5) * mm});
            skLineSegment(sketch, "E808", {"start": v(903.47, 2355.5) * mm, "end": v(996.94, 2336.2) * mm});
            skLineSegment(sketch, "E809", {"start": v(996.94, 2336.2) * mm, "end": v(1013.2, 2415.95) * mm});
            skLineSegment(sketch, "E810", {"start": v(565.14, 2425.1) * mm, "end": v(826.25, 2371.5) * mm});
            skLineSegment(sketch, "E811", {"start": v(406.13, 2307.5) * mm, "end": v(406.64, 2310.03) * mm});
            skLineSegment(sketch, "E812", {"start": v(406.64, 2310.03) * mm, "end": v(435.85, 2451.77) * mm});
            skLineSegment(sketch, "E813", {"start": v(435.85, 2451.77) * mm, "end": v(565.14, 2425.1) * mm});
            skLineSegment(sketch, "E814", {"start": v(565.14, 2425.1) * mm, "end": v(586.22, 2527.2) * mm});
            skLineSegment(sketch, "E815", {"start": v(586.22, 2527.2) * mm, "end": v(847.33, 2473.36) * mm});
            skLineSegment(sketch, "E816", {"start": v(847.33, 2473.36) * mm, "end": v(826.25, 2371.5) * mm});
            skLineSegment(sketch, "E817", {"start": v(310.88, 1843.44) * mm, "end": v(328.4, 1928.78) * mm});
            skLineSegment(sketch, "E818", {"start": v(328.4, 1928.78) * mm, "end": v(368.54, 2124.87) * mm});
            skLineSegment(sketch, "E819", {"start": v(368.54, 2124.87) * mm, "end": v(132.58, 2173.38) * mm});
            skLineSegment(sketch, "E820", {"start": v(368.54, 2124.87) * mm, "end": v(406.13, 2307.5) * mm});
            skLineSegment(sketch, "E821", {"start": v(406.13, 2307.5) * mm, "end": v(172.45, 2355.5) * mm});
            skLineSegment(sketch, "E822", {"start": v(935.72, 933.6) * mm, "end": v(1020.05, 1341.79) * mm});
            skLineSegment(sketch, "E823", {"start": v(1020.05, 1341.79) * mm, "end": v(1043.67, 1456.09) * mm});
            skLineSegment(sketch, "E824", {"start": v(1043.67, 1456.09) * mm, "end": v(1073.4, 1449.48) * mm});
            skLineSegment(sketch, "E825", {"start": v(1153.15, 1431.7) * mm, "end": v(1225.03, 1333.15) * mm});
            skLineSegment(sketch, "E826", {"start": v(1073.4, 1449.48) * mm, "end": v(1153.15, 1431.7) * mm});
            skLineSegment(sketch, "E827", {"start": v(1352.54, 1426.11) * mm, "end": v(1225.03, 1333.15) * mm});
            skLineSegment(sketch, "E828", {"start": v(772.4, 854.87) * mm, "end": v(835.14, 730.66) * mm});
            skLineSegment(sketch, "E829", {"start": v(750.81, 844.2) * mm, "end": v(813.04, 720.76) * mm});
            skLineSegment(sketch, "E830", {"start": v(729.48, 833.28) * mm, "end": v(791.2, 710.85) * mm});
            skLineSegment(sketch, "E831", {"start": v(772.4, 854.87) * mm, "end": v(784.34, 860.96) * mm});
            skLineSegment(sketch, "E832", {"start": v(718.55, 874.43) * mm, "end": v(784.34, 860.96) * mm});
            skLineSegment(sketch, "E833", {"start": v(835.14, 730.66) * mm, "end": v(769.1, 700.94) * mm});
            skLineSegment(sketch, "E834", {"start": v(707.89, 822.36) * mm, "end": v(769.1, 700.94) * mm});
            skLineSegment(sketch, "E835", {"start": v(718.55, 874.43) * mm, "end": v(738.87, 974) * mm});
            skLineSegment(sketch, "E836", {"start": v(738.87, 974) * mm, "end": v(935.72, 933.6) * mm});
            skLineSegment(sketch, "E837", {"start": v(707.89, 822.36) * mm, "end": v(772.4, 854.87) * mm});
            skLineSegment(sketch, "E838", {"start": v(935.72, 933.6) * mm, "end": v(985.5, 923.45) * mm});
            skLineSegment(sketch, "E839", {"start": v(985.5, 923.45) * mm, "end": v(952.74, 821.09) * mm});
            skLineSegment(sketch, "E840", {"start": v(952.74, 821.09) * mm, "end": v(896.6, 758.6) * mm});
            skLineSegment(sketch, "E841", {"start": v(896.6, 758.6) * mm, "end": v(835.14, 730.66) * mm});
            skLineSegment(sketch, "E842", {"start": v(2140.45, 2443.13) * mm, "end": v(2065.52, 2419) * mm});
            skLineSegment(sketch, "E843", {"start": v(2065.52, 2419) * mm, "end": v(1906.77, 2369.47) * mm});
            skLineSegment(sketch, "E844", {"start": v(1906.77, 2369.47) * mm, "end": v(1765.29, 2284.63) * mm});
            skLineSegment(sketch, "E845", {"start": v(2205.22, 2233.58) * mm, "end": v(2140.45, 2443.13) * mm});
            skLineSegment(sketch, "E846", {"start": v(-2469.65, -648.05) * mm, "end": v(-2453.14, -640.94) * mm});
            skLineSegment(sketch, "E847", {"start": v(-2453.14, -640.94) * mm, "end": v(-2336.3, -584.55) * mm});
            skLineSegment(sketch, "E848", {"start": v(-2336.3, -584.55) * mm, "end": v(-2321.06, -616.3) * mm});
            skLineSegment(sketch, "E849", {"start": v(-3188.73, 148.45) * mm, "end": v(-3068.33, 199.04) * mm});
            skLineSegment(sketch, "E850", {"start": v(-2589.03, 1570.64) * mm, "end": v(-2690.63, 1594.77) * mm});
            skLineSegment(sketch, "E851", {"start": v(-2628.4, -1852.01) * mm, "end": v(-2577.86, -2102.45) * mm});
            skLineSegment(sketch, "E852", {"start": v(-2690.63, 1584.6) * mm, "end": v(-2818.9, 1005.49) * mm});
            skLineSegment(sketch, "E853", {"start": v(-2818.9, 1005.49) * mm, "end": v(-2995.43, 897.54) * mm});
            skLineSegment(sketch, "E854", {"start": v(-3188.73, 1075.76) * mm, "end": v(-2995.43, 897.54) * mm});
            skLineSegment(sketch, "E855", {"start": v(-3188.73, 923.86) * mm, "end": v(-3095, 837.34) * mm});
            skLineSegment(sketch, "E856", {"start": v(-2864.88, -2124.3) * mm, "end": v(-2577.86, -2102.45) * mm});
            skLineSegment(sketch, "E857", {"start": v(-3188.73, -2208.83) * mm, "end": v(-3188.47, -2208.88) * mm});
            skLineSegment(sketch, "E858", {"start": v(-3188.47, -2208.88) * mm, "end": v(-3170.7, -2210.15) * mm});
            skLineSegment(sketch, "E859", {"start": v(-3170.7, -2210.15) * mm, "end": v(-3151.64, -2210.15) * mm});
            skLineSegment(sketch, "E860", {"start": v(-3151.64, -2210.15) * mm, "end": v(-3099.57, -2207.61) * mm});
            skLineSegment(sketch, "E861", {"start": v(-3099.57, -2207.61) * mm, "end": v(-2609.35, -2175.86) * mm});
            skLineSegment(sketch, "E862", {"start": v(-2609.35, -2175.86) * mm, "end": v(-2453.14, -2156.81) * mm});
            skLineSegment(sketch, "E863", {"start": v(-2453.14, -2156.81) * mm, "end": v(-2107.7, -2113.63) * mm});
            skLineSegment(sketch, "E864", {"start": v(-2107.7, -2113.63) * mm, "end": v(-2084.84, -2111.1) * mm});
            skLineSegment(sketch, "E865", {"start": v(-2084.84, -2111.1) * mm, "end": v(-2064.52, -2107.28) * mm});
            skLineSegment(sketch, "E866", {"start": v(-2064.52, -2107.28) * mm, "end": v(-2055.63, -2103.47) * mm});
            skLineSegment(sketch, "E867", {"start": v(-2055.63, -2103.47) * mm, "end": v(-2042.93, -2092.04) * mm});
            skLineSegment(sketch, "E868", {"start": v(-3108.46, 737.52) * mm, "end": v(-2775.72, 23.78) * mm});
            skLineSegment(sketch, "E869", {"start": v(-2775.72, 23.78) * mm, "end": v(-2741.43, 39.02) * mm});
            skLineSegment(sketch, "E870", {"start": v(-2741.43, 39.02) * mm, "end": v(-2690.63, -71.47) * mm});
            skLineSegment(sketch, "E871", {"start": v(-2690.63, -71.47) * mm, "end": v(-2726.2, -89.25) * mm});
            skLineSegment(sketch, "E872", {"start": v(-3188.73, -2099.12) * mm, "end": v(-3126.24, -2144.11) * mm});
            skLineSegment(sketch, "E873", {"start": v(-3126.24, -2144.11) * mm, "end": v(-2864.88, -2124.3) * mm});
            skLineSegment(sketch, "E874", {"start": v(-2690.63, 1584.6) * mm, "end": v(-2690.63, 1594.77) * mm});
            skLineSegment(sketch, "E875", {"start": v(-2577.86, -2102.45) * mm, "end": v(-2453.14, -2084.93) * mm});
            skLineSegment(sketch, "E876", {"start": v(-2453.14, -2084.93) * mm, "end": v(-2106.43, -2034.9) * mm});
            skLineSegment(sketch, "E877", {"start": v(-2106.43, -2034.9) * mm, "end": v(-2096.27, -2033.62) * mm});
            skLineSegment(sketch, "E878", {"start": v(-2096.27, -2033.62) * mm, "end": v(-2083.57, -2029.81) * mm});
            skLineSegment(sketch, "E879", {"start": v(-2083.57, -2029.81) * mm, "end": v(-2075.95, -2024.73) * mm});
            skLineSegment(sketch, "E880", {"start": v(-2075.95, -2024.73) * mm, "end": v(-2070.87, -2020.92) * mm});
            skLineSegment(sketch, "E881", {"start": v(-2070.87, -2020.92) * mm, "end": v(-2064.52, -2014.57) * mm});
            skLineSegment(sketch, "E882", {"start": v(-2064.52, -2014.57) * mm, "end": v(-2059.44, -2008.22) * mm});
            skLineSegment(sketch, "E883", {"start": v(-2059.44, -2008.22) * mm, "end": v(-2056.9, -2005.68) * mm});
            skLineSegment(sketch, "E884", {"start": v(-2056.9, -2005.68) * mm, "end": v(-2054.36, -2001.87) * mm});
            skLineSegment(sketch, "E885", {"start": v(-2054.36, -2001.87) * mm, "end": v(-2053.1, -1996.8) * mm});
            skLineSegment(sketch, "E886", {"start": v(-2053.1, -1996.8) * mm, "end": v(-2051.82, -1992.98) * mm});
            skLineSegment(sketch, "E887", {"start": v(-2051.82, -1992.98) * mm, "end": v(-2050.55, -1987.9) * mm});
            skLineSegment(sketch, "E888", {"start": v(-2050.55, -1987.9) * mm, "end": v(-2051.82, -1982.82) * mm});
            skLineSegment(sketch, "E889", {"start": v(-2051.82, -1982.82) * mm, "end": v(-2053.1, -1979.01) * mm});
            skLineSegment(sketch, "E890", {"start": v(-2053.1, -1979.01) * mm, "end": v(-2243.6, -1578.96) * mm});
            skLineSegment(sketch, "E891", {"start": v(-1999.5, -2307.69) * mm, "end": v(-2042.17, -2314.8) * mm});
            skLineSegment(sketch, "E892", {"start": v(-2042.17, -2314.8) * mm, "end": v(-2159.77, -2332.58) * mm});
            skLineSegment(sketch, "E893", {"start": v(-2159.77, -2332.58) * mm, "end": v(-2245.37, -2340.2) * mm});
            skLineSegment(sketch, "E894", {"start": v(-2245.37, -2340.2) * mm, "end": v(-2453.14, -2352.14) * mm});
            skLineSegment(sketch, "E895", {"start": v(-2453.14, -2352.14) * mm, "end": v(-3188.73, -2383.5) * mm});
            skLineSegment(sketch, "E896", {"start": v(-2775.72, 23.78) * mm, "end": v(-2726.2, -89.25) * mm});
            skLineSegment(sketch, "E897", {"start": v(-2726.2, -89.25) * mm, "end": v(-2469.65, -648.05) * mm});
            skLineSegment(sketch, "E898", {"start": v(-2469.65, -648.05) * mm, "end": v(-2453.14, -678.53) * mm});
            skLineSegment(sketch, "E899", {"start": v(-2453.14, -678.53) * mm, "end": v(-2443.24, -673.7) * mm});
            skLineSegment(sketch, "E900", {"start": v(-2443.24, -673.7) * mm, "end": v(-2453.14, -695.8) * mm});
            skLineSegment(sketch, "E901", {"start": v(-2453.14, -695.8) * mm, "end": v(-2454.41, -701.4) * mm});
            skLineSegment(sketch, "E902", {"start": v(-2454.41, -701.4) * mm, "end": v(-2459.5, -711.55) * mm});
            skLineSegment(sketch, "E903", {"start": v(-2459.5, -711.55) * mm, "end": v(-2470.92, -712.82) * mm});
            skLineSegment(sketch, "E904", {"start": v(-2470.92, -712.82) * mm, "end": v(-2488.7, -707.74) * mm});
            skLineSegment(sketch, "E905", {"start": v(-2488.7, -707.74) * mm, "end": v(-2497.6, -696.31) * mm});
            skLineSegment(sketch, "E906", {"start": v(-2497.6, -696.31) * mm, "end": v(-2647.45, -376.27) * mm});
            skLineSegment(sketch, "E907", {"start": v(-2647.45, -376.27) * mm, "end": v(-2977.65, 340) * mm});
            skLineSegment(sketch, "E908", {"start": v(-2977.65, 340) * mm, "end": v(-3160.53, 743.87) * mm});
            skLineSegment(sketch, "E909", {"start": v(-3160.53, 743.87) * mm, "end": v(-3182.12, 794.67) * mm});
            skLineSegment(sketch, "E910", {"start": v(-3182.12, 794.67) * mm, "end": v(-3188.73, 808.98) * mm});
            skLineSegment(sketch, "E911", {"start": v(-3188.73, -1877.23) * mm, "end": v(-3007.12, -1870.04) * mm});
            skLineSegment(sketch, "E912", {"start": v(-2628.4, -1852.01) * mm, "end": v(-2453.14, -1824.58) * mm});
            skLineSegment(sketch, "E913", {"start": v(-2453.14, -1824.58) * mm, "end": v(-2397.26, -1817.72) * mm});
            skLineSegment(sketch, "E914", {"start": v(-2397.26, -1817.72) * mm, "end": v(-2453.14, -1681.83) * mm});
            skLineSegment(sketch, "E915", {"start": v(-2453.14, -1681.83) * mm, "end": v(-2243.6, -1578.96) * mm});
            skLineSegment(sketch, "E916", {"start": v(-2864.88, -2124.3) * mm, "end": v(-2911.61, -1866.23) * mm});
            skLineSegment(sketch, "E917", {"start": v(-3168.92, -2581) * mm, "end": v(-3175.27, -2502.25) * mm});
            skLineSegment(sketch, "E918", {"start": v(-3095, 837.34) * mm, "end": v(-3039.88, 785.78) * mm});
            skLineSegment(sketch, "E919", {"start": v(-3039.88, 785.78) * mm, "end": v(-3108.46, 737.52) * mm});
            skLineSegment(sketch, "E920", {"start": v(-2779.53, -2464.15) * mm, "end": v(-2453.14, -2430.37) * mm});
            skLineSegment(sketch, "E921", {"start": v(-2453.14, -2430.37) * mm, "end": v(-2440.44, -2429.86) * mm});
            skLineSegment(sketch, "E922", {"start": v(-2440.44, -2429.86) * mm, "end": v(-2439.17, -2440.02) * mm});
            skLineSegment(sketch, "E923", {"start": v(-2311.67, -1427.07) * mm, "end": v(-2302.01, -1420.21) * mm});
            skLineSegment(sketch, "E924", {"start": v(-2302.01, -1420.21) * mm, "end": v(-2299.47, -1417.67) * mm});
            skLineSegment(sketch, "E925", {"start": v(-2299.47, -1417.67) * mm, "end": v(-2295.66, -1415.13) * mm});
            skLineSegment(sketch, "E926", {"start": v(-2295.66, -1415.13) * mm, "end": v(-2293.12, -1412.6) * mm});
            skLineSegment(sketch, "E927", {"start": v(-2293.12, -1412.6) * mm, "end": v(-2291.85, -1410.05) * mm});
            skLineSegment(sketch, "E928", {"start": v(-2291.85, -1410.05) * mm, "end": v(-2290.58, -1406.24) * mm});
            skLineSegment(sketch, "E929", {"start": v(-2290.58, -1406.24) * mm, "end": v(-2290.58, -1402.43) * mm});
            skLineSegment(sketch, "E930", {"start": v(-2290.58, -1402.43) * mm, "end": v(-2291.85, -1398.62) * mm});
            skLineSegment(sketch, "E931", {"start": v(-2291.85, -1398.62) * mm, "end": v(-2453.14, -1049.37) * mm});
            skLineSegment(sketch, "E932", {"start": v(-2453.14, -1049.37) * mm, "end": v(-2966.22, 54.26) * mm});
            skLineSegment(sketch, "E933", {"start": v(-2966.22, 54.26) * mm, "end": v(-3099.57, 340) * mm});
            skLineSegment(sketch, "E934", {"start": v(-3099.57, 340) * mm, "end": v(-3188.73, 541.12) * mm});
            skLineSegment(sketch, "E935", {"start": v(-2779.53, -2464.15) * mm, "end": v(-2770.9, -2553.05) * mm});
            skLineSegment(sketch, "E936", {"start": v(-3188.73, 455.94) * mm, "end": v(-3068.33, 199.04) * mm});
            skLineSegment(sketch, "E937", {"start": v(-2210.32, 2043.33) * mm, "end": v(-2380, 1928.78) * mm});
            skLineSegment(sketch, "E938", {"start": v(-2380, 1928.78) * mm, "end": v(-2453.14, 1881.28) * mm});
            skLineSegment(sketch, "E939", {"start": v(-2453.14, 1881.28) * mm, "end": v(-2580.14, 1797.97) * mm});
            skLineSegment(sketch, "E940", {"start": v(-2580.14, 1797.97) * mm, "end": v(-2605.54, 1778.92) * mm});
            skLineSegment(sketch, "E941", {"start": v(-2605.54, 1778.92) * mm, "end": v(-2615.7, 1770.03) * mm});
            skLineSegment(sketch, "E942", {"start": v(-2615.7, 1770.03) * mm, "end": v(-2624.6, 1759.87) * mm});
            skLineSegment(sketch, "E943", {"start": v(-2624.6, 1759.87) * mm, "end": v(-2634.75, 1744.63) * mm});
            skLineSegment(sketch, "E944", {"start": v(-2634.75, 1744.63) * mm, "end": v(-2655.07, 1703.99) * mm});
            skLineSegment(sketch, "E945", {"start": v(-2655.07, 1703.99) * mm, "end": v(-2672.85, 1658.27) * mm});
            skLineSegment(sketch, "E946", {"start": v(-2672.85, 1658.27) * mm, "end": v(-2686.82, 1616.36) * mm});
            skLineSegment(sketch, "E947", {"start": v(-3188.73, -1386.24) * mm, "end": v(-3156.72, -1376.01) * mm});
            skLineSegment(sketch, "E948", {"start": v(-3156.72, -1376.01) * mm, "end": v(-3151.64, -1394.81) * mm});
            skLineSegment(sketch, "E949", {"start": v(-2995.43, 897.54) * mm, "end": v(-3095, 837.34) * mm});
            skLineSegment(sketch, "E950", {"start": v(-3095, 837.34) * mm, "end": v(-3140.21, 809.9) * mm});
            skLineSegment(sketch, "E951", {"start": v(-3140.21, 809.9) * mm, "end": v(-3108.46, 737.52) * mm});
            skLineSegment(sketch, "E952", {"start": v(-3068.33, 199.04) * mm, "end": v(-2773.18, -432.15) * mm});
            skLineSegment(sketch, "E953", {"start": v(-2773.18, -432.15) * mm, "end": v(-2453.14, -1112.1) * mm});
            skLineSegment(sketch, "E954", {"start": v(-2453.14, -1112.1) * mm, "end": v(-2311.67, -1427.07) * mm});
            skLineSegment(sketch, "E955", {"start": v(-2832.11, 1961.8) * mm, "end": v(-2834.4, 1966.12) * mm});
            skLineSegment(sketch, "E956", {"start": v(-2834.4, 1966.12) * mm, "end": v(-2938.54, 2169.06) * mm});
            skLineSegment(sketch, "E957", {"start": v(-2938.54, 2169.06) * mm, "end": v(-2953.52, 2161.19) * mm});
            skLineSegment(sketch, "E958", {"start": v(-2953.52, 2161.19) * mm, "end": v(-2981.46, 2146.46) * mm});
            skLineSegment(sketch, "E959", {"start": v(-2981.46, 2146.46) * mm, "end": v(-3188.73, 2437.03) * mm});
            skLineSegment(sketch, "E960", {"start": v(-2341.38, 2237.39) * mm, "end": v(-2345.2, 2225.96) * mm});
            skLineSegment(sketch, "E961", {"start": v(-2345.2, 2225.96) * mm, "end": v(-2347.73, 2220.88) * mm});
            skLineSegment(sketch, "E962", {"start": v(-2347.73, 2220.88) * mm, "end": v(-2349, 2217.07) * mm});
            skLineSegment(sketch, "E963", {"start": v(-2349, 2217.07) * mm, "end": v(-2352.81, 2210.72) * mm});
            skLineSegment(sketch, "E964", {"start": v(-2352.81, 2210.72) * mm, "end": v(-2356.62, 2205.64) * mm});
            skLineSegment(sketch, "E965", {"start": v(-2356.62, 2205.64) * mm, "end": v(-2359.16, 2203.1) * mm});
            skLineSegment(sketch, "E966", {"start": v(-2359.16, 2203.1) * mm, "end": v(-2360.43, 2199.29) * mm});
            skLineSegment(sketch, "E967", {"start": v(-2360.43, 2199.29) * mm, "end": v(-2364.24, 2196.75) * mm});
            skLineSegment(sketch, "E968", {"start": v(-2364.24, 2196.75) * mm, "end": v(-2369.32, 2192.94) * mm});
            skLineSegment(sketch, "E969", {"start": v(-2369.32, 2192.94) * mm, "end": v(-2370.6, 2190.4) * mm});
            skLineSegment(sketch, "E970", {"start": v(-2370.6, 2190.4) * mm, "end": v(-2404.88, 2156.1) * mm});
            skLineSegment(sketch, "E971", {"start": v(-2404.88, 2156.1) * mm, "end": v(-2453.14, 2119.28) * mm});
            skLineSegment(sketch, "E972", {"start": v(-2453.14, 2119.28) * mm, "end": v(-2817.63, 1928.78) * mm});
            skLineSegment(sketch, "E973", {"start": v(-2817.63, 1928.78) * mm, "end": v(-3116.34, 1772.57) * mm});
            skLineSegment(sketch, "E974", {"start": v(-3116.34, 1772.57) * mm, "end": v(-3188.73, 1735.66) * mm});
            skLineSegment(sketch, "E975", {"start": v(-2832.11, 1961.8) * mm, "end": v(-2795.8, 1980.6) * mm});
            skLineSegment(sketch, "E976", {"start": v(-2795.8, 1980.6) * mm, "end": v(-2677.68, 2041.56) * mm});
            skLineSegment(sketch, "E977", {"start": v(-2609.86, 2475.39) * mm, "end": v(-2864.62, 2326.29) * mm});
            skLineSegment(sketch, "E978", {"start": v(-3188.73, 2497.94) * mm, "end": v(-3165.61, 2512.98) * mm});
            skLineSegment(sketch, "E979", {"start": v(-3165.61, 2512.98) * mm, "end": v(-3139.2, 2530.25) * mm});
            skLineSegment(sketch, "E980", {"start": v(-3139.2, 2530.25) * mm, "end": v(-2972.57, 2280.57) * mm});
            skLineSegment(sketch, "E981", {"start": v(-2972.57, 2280.57) * mm, "end": v(-3021.09, 2260.25) * mm});
            skLineSegment(sketch, "E982", {"start": v(-3021.09, 2260.25) * mm, "end": v(-3178.31, 2477.42) * mm});
            skLineSegment(sketch, "E983", {"start": v(-3178.31, 2477.42) * mm, "end": v(-3188.73, 2491.76) * mm});
            skLineSegment(sketch, "E984", {"start": v(-2864.62, 2326.29) * mm, "end": v(-2805.95, 2239.17) * mm});
            skLineSegment(sketch, "E985", {"start": v(-2805.95, 2239.17) * mm, "end": v(-2677.68, 2041.56) * mm});
            skLineSegment(sketch, "E986", {"start": v(-2911.61, -1866.23) * mm, "end": v(-2652.53, -1855.82) * mm});
            skLineSegment(sketch, "E987", {"start": v(-2652.53, -1855.82) * mm, "end": v(-2628.4, -1852.01) * mm});
            skLineSegment(sketch, "E988", {"start": v(-3007.12, -1870.04) * mm, "end": v(-2911.61, -1866.23) * mm});
            skLineSegment(sketch, "E989", {"start": v(-2690.63, 1594.77) * mm, "end": v(-2689.36, 1604.93) * mm});
            skLineSegment(sketch, "E990", {"start": v(-2689.36, 1604.93) * mm, "end": v(-2686.82, 1616.36) * mm});
            skLineSegment(sketch, "E991", {"start": v(-2589.03, 1570.64) * mm, "end": v(-2609.35, 1477.93) * mm});
            skLineSegment(sketch, "E992", {"start": v(-2609.35, 1477.93) * mm, "end": v(-2618.24, 1480.47) * mm});
            skLineSegment(sketch, "E993", {"start": v(-2618.24, 1480.47) * mm, "end": v(-2627.13, 1484.28) * mm});
            skLineSegment(sketch, "E994", {"start": v(-2627.13, 1484.28) * mm, "end": v(-2643.64, 1493.17) * mm});
            skLineSegment(sketch, "E995", {"start": v(-2643.64, 1493.17) * mm, "end": v(-2651.26, 1499.52) * mm});
            skLineSegment(sketch, "E996", {"start": v(-2651.26, 1499.52) * mm, "end": v(-2658.88, 1507.14) * mm});
            skLineSegment(sketch, "E997", {"start": v(-2658.88, 1507.14) * mm, "end": v(-2665.23, 1514.76) * mm});
            skLineSegment(sketch, "E998", {"start": v(-2665.23, 1514.76) * mm, "end": v(-2676.66, 1531.27) * mm});
            skLineSegment(sketch, "E999", {"start": v(-2676.66, 1531.27) * mm, "end": v(-2681.74, 1540.16) * mm});
            skLineSegment(sketch, "E1000", {"start": v(-2681.74, 1540.16) * mm, "end": v(-2684.28, 1550.32) * mm});
            skLineSegment(sketch, "E1001", {"start": v(-2684.28, 1550.32) * mm, "end": v(-2688.1, 1560.48) * mm});
            skLineSegment(sketch, "E1002", {"start": v(-2688.1, 1560.48) * mm, "end": v(-2689.36, 1570.64) * mm});
            skLineSegment(sketch, "E1003", {"start": v(-2689.36, 1570.64) * mm, "end": v(-2690.63, 1584.6) * mm});
            skLineSegment(sketch, "E1004", {"start": v(-2677.68, 2041.56) * mm, "end": v(-2453.14, 2149.76) * mm});
            skLineSegment(sketch, "E1005", {"start": v(-2453.14, 2149.76) * mm, "end": v(-2444.25, 2158.65) * mm});
            skLineSegment(sketch, "E1006", {"start": v(-2444.25, 2158.65) * mm, "end": v(-2439.17, 2215.8) * mm});
            skLineSegment(sketch, "E1007", {"start": v(-2439.17, 2215.8) * mm, "end": v(-2453.14, 2238.66) * mm});
            skLineSegment(sketch, "E1008", {"start": v(-2453.14, 2238.66) * mm, "end": v(-2609.86, 2475.39) * mm});
            skLineSegment(sketch, "E1009", {"start": v(-3188.73, 1777.72) * mm, "end": v(-2896.12, 1928.78) * mm});
            skLineSegment(sketch, "E1010", {"start": v(-2896.12, 1928.78) * mm, "end": v(-2832.11, 1961.8) * mm});
            skLineSegment(sketch, "E1011", {"start": v(-2953.52, 2161.19) * mm, "end": v(-3021.09, 2260.25) * mm});
            skLineSegment(sketch, "E1012", {"start": v(-2864.62, 2326.29) * mm, "end": v(-2972.57, 2280.57) * mm});
            skLineSegment(sketch, "E1013", {"start": v(-1316.5, 2409.86) * mm, "end": v(-1270.52, 2399.7) * mm});
            skLineSegment(sketch, "E1014", {"start": v(-1191.02, 2619.66) * mm, "end": v(-1187.2, 2639.98) * mm});
            skLineSegment(sketch, "E1015", {"start": v(-1270.52, 2399.7) * mm, "end": v(-1235.72, 2391.82) * mm});
            skLineSegment(sketch, "E1016", {"start": v(-1984.51, 2355.5) * mm, "end": v(-1903.23, 2229.77) * mm});
            skLineSegment(sketch, "E1017", {"start": v(-2021.34, 2412.65) * mm, "end": v(-1984.51, 2355.5) * mm});
            skLineSegment(sketch, "E1018", {"start": v(-1903.23, 2229.77) * mm, "end": v(-1842.27, 2134.52) * mm});
            skLineSegment(sketch, "E1019", {"start": v(-1292.11, 2404.52) * mm, "end": v(-1260.61, 2546) * mm});
            skLineSegment(sketch, "E1020", {"start": v(-1260.61, 2546) * mm, "end": v(-1259.34, 2551.08) * mm});
            skLineSegment(sketch, "E1021", {"start": v(-1259.34, 2551.08) * mm, "end": v(-1256.8, 2554.89) * mm});
            skLineSegment(sketch, "E1022", {"start": v(-1256.8, 2554.89) * mm, "end": v(-1255.53, 2558.7) * mm});
            skLineSegment(sketch, "E1023", {"start": v(-1255.53, 2558.7) * mm, "end": v(-1254.26, 2561.24) * mm});
            skLineSegment(sketch, "E1024", {"start": v(-1254.26, 2561.24) * mm, "end": v(-1251.72, 2562.5) * mm});
            skLineSegment(sketch, "E1025", {"start": v(-1251.72, 2562.5) * mm, "end": v(-1250.45, 2566.32) * mm});
            skLineSegment(sketch, "E1026", {"start": v(-1250.45, 2566.32) * mm, "end": v(-1249.18, 2568.86) * mm});
            skLineSegment(sketch, "E1027", {"start": v(-1249.18, 2568.86) * mm, "end": v(-1236.48, 2581.56) * mm});
            skLineSegment(sketch, "E1028", {"start": v(-1236.48, 2581.56) * mm, "end": v(-1233.94, 2582.83) * mm});
            skLineSegment(sketch, "E1029", {"start": v(-1233.94, 2582.83) * mm, "end": v(-1231.4, 2585.37) * mm});
            skLineSegment(sketch, "E1030", {"start": v(-1231.4, 2585.37) * mm, "end": v(-1228.86, 2586.64) * mm});
            skLineSegment(sketch, "E1031", {"start": v(-1228.86, 2586.64) * mm, "end": v(-1222.51, 2589.18) * mm});
            skLineSegment(sketch, "E1032", {"start": v(-1222.51, 2589.18) * mm, "end": v(-1221.24, 2591.72) * mm});
            skLineSegment(sketch, "E1033", {"start": v(-1221.24, 2591.72) * mm, "end": v(-1216.16, 2591.72) * mm});
            skLineSegment(sketch, "E1034", {"start": v(-1216.16, 2591.72) * mm, "end": v(-1213.62, 2592.99) * mm});
            skLineSegment(sketch, "E1035", {"start": v(-1213.62, 2592.99) * mm, "end": v(-1207.27, 2595.53) * mm});
            skLineSegment(sketch, "E1036", {"start": v(-1207.27, 2595.53) * mm, "end": v(-1200.92, 2595.53) * mm});
            skLineSegment(sketch, "E1037", {"start": v(-1200.92, 2595.53) * mm, "end": v(-1195.6, 2597.3) * mm});
            skLineSegment(sketch, "E1038", {"start": v(-1714, 2217.07) * mm, "end": v(-1774.96, 2311.05) * mm});
            skLineSegment(sketch, "E1039", {"start": v(-1363.48, 2420.27) * mm, "end": v(-1331.73, 2571.4) * mm});
            skLineSegment(sketch, "E1040", {"start": v(-1331.73, 2571.4) * mm, "end": v(-1330.46, 2575.2) * mm});
            skLineSegment(sketch, "E1041", {"start": v(-1330.46, 2575.2) * mm, "end": v(-1327.92, 2579.02) * mm});
            skLineSegment(sketch, "E1042", {"start": v(-1327.92, 2579.02) * mm, "end": v(-1326.65, 2585.37) * mm});
            skLineSegment(sketch, "E1043", {"start": v(-1326.65, 2585.37) * mm, "end": v(-1324.11, 2589.18) * mm});
            skLineSegment(sketch, "E1044", {"start": v(-1324.11, 2589.18) * mm, "end": v(-1322.84, 2592.99) * mm});
            skLineSegment(sketch, "E1045", {"start": v(-1322.84, 2592.99) * mm, "end": v(-1320.3, 2596.8) * mm});
            skLineSegment(sketch, "E1046", {"start": v(-1320.3, 2596.8) * mm, "end": v(-1317.76, 2601.88) * mm});
            skLineSegment(sketch, "E1047", {"start": v(-1317.76, 2601.88) * mm, "end": v(-1312.68, 2609.5) * mm});
            skLineSegment(sketch, "E1048", {"start": v(-1312.68, 2609.5) * mm, "end": v(-1292.36, 2629.82) * mm});
            skLineSegment(sketch, "E1049", {"start": v(-1292.36, 2629.82) * mm, "end": v(-1288.55, 2632.36) * mm});
            skLineSegment(sketch, "E1050", {"start": v(-1288.55, 2632.36) * mm, "end": v(-1286.01, 2633.63) * mm});
            skLineSegment(sketch, "E1051", {"start": v(-1286.01, 2633.63) * mm, "end": v(-1282.2, 2637.44) * mm});
            skLineSegment(sketch, "E1052", {"start": v(-1282.2, 2637.44) * mm, "end": v(-1274.58, 2642.52) * mm});
            skLineSegment(sketch, "E1053", {"start": v(-1274.58, 2642.52) * mm, "end": v(-1269.5, 2643.79) * mm});
            skLineSegment(sketch, "E1054", {"start": v(-1269.5, 2643.79) * mm, "end": v(-1265.7, 2646.33) * mm});
            skLineSegment(sketch, "E1055", {"start": v(-1265.7, 2646.33) * mm, "end": v(-1261.88, 2647.6) * mm});
            skLineSegment(sketch, "E1056", {"start": v(-1261.88, 2647.6) * mm, "end": v(-1251.72, 2652.68) * mm});
            skLineSegment(sketch, "E1057", {"start": v(-1251.72, 2652.68) * mm, "end": v(-1246.64, 2653.95) * mm});
            skLineSegment(sketch, "E1058", {"start": v(-1246.64, 2653.95) * mm, "end": v(-1242.83, 2653.95) * mm});
            skLineSegment(sketch, "E1059", {"start": v(-1242.83, 2653.95) * mm, "end": v(-1237.75, 2656.49) * mm});
            skLineSegment(sketch, "E1060", {"start": v(-1237.75, 2656.49) * mm, "end": v(-1233.94, 2656.49) * mm});
            skLineSegment(sketch, "E1061", {"start": v(-1233.94, 2656.49) * mm, "end": v(-1230.13, 2657.76) * mm});
            skLineSegment(sketch, "E1062", {"start": v(-1230.13, 2657.76) * mm, "end": v(-1223.78, 2660.3) * mm});
            skLineSegment(sketch, "E1063", {"start": v(-1223.78, 2660.3) * mm, "end": v(-1216.16, 2660.3) * mm});
            skLineSegment(sketch, "E1064", {"start": v(-1216.16, 2660.3) * mm, "end": v(-1211.08, 2662.84) * mm});
            skLineSegment(sketch, "E1065", {"start": v(-1211.08, 2662.84) * mm, "end": v(-1182.64, 2662.84) * mm});
            skLineSegment(sketch, "E1066", {"start": v(1760.72, 2233.58) * mm, "end": v(1788.66, 2247.55) * mm});
            skLineSegment(sketch, "E1067", {"start": v(-1903.23, 2229.77) * mm, "end": v(-2024.4, 2157.38) * mm});
            skLineSegment(sketch, "E1068", {"start": v(-2024.4, 2157.38) * mm, "end": v(-2175.01, 2067.2) * mm});
            skLineSegment(sketch, "E1069", {"start": v(-2175.01, 2067.2) * mm, "end": v(-2210.32, 2043.33) * mm});
            skLineSegment(sketch, "E1070", {"start": v(2191.25, 2420.52) * mm, "end": v(2280.15, 2148.49) * mm});
            skLineSegment(sketch, "E1071", {"start": v(2280.15, 2148.49) * mm, "end": v(2355.08, 1928.78) * mm});
            skLineSegment(sketch, "E1072", {"start": v(2355.08, 1928.78) * mm, "end": v(2461.76, 1611.28) * mm});
            skLineSegment(sketch, "E1073", {"start": v(2461.76, 1611.28) * mm, "end": v(2470.65, 1571.9) * mm});
            skLineSegment(sketch, "E1074", {"start": v(2470.65, 1571.9) * mm, "end": v(2470.65, 1552.86) * mm});
            skLineSegment(sketch, "E1075", {"start": v(2470.65, 1552.86) * mm, "end": v(2468.1, 1543.97) * mm});
            skLineSegment(sketch, "E1076", {"start": v(2468.1, 1543.97) * mm, "end": v(2466.84, 1536.35) * mm});
            skLineSegment(sketch, "E1077", {"start": v(2466.84, 1536.35) * mm, "end": v(2464.3, 1530) * mm});
            skLineSegment(sketch, "E1078", {"start": v(2464.3, 1530) * mm, "end": v(2459.22, 1519.84) * mm});
            skLineSegment(sketch, "E1079", {"start": v(-1896.88, 2493.93) * mm, "end": v(-2021.34, 2412.65) * mm});
            skLineSegment(sketch, "E1080", {"start": v(-1774.96, 2311.05) * mm, "end": v(-1854.97, 2432.97) * mm});
            skLineSegment(sketch, "E1081", {"start": v(2223, 2178.97) * mm, "end": v(2205.22, 2233.58) * mm});
            skLineSegment(sketch, "E1082", {"start": v(379.18, 326.65) * mm, "end": v(337.38, 335.77) * mm});
            skLineSegment(sketch, "E1083", {"start": v(2696.83, 2143.84) * mm, "end": v(2729.85, 2190.22) * mm});
            skLineSegment(sketch, "E1084", {"start": v(581.3, 902.65) * mm, "end": v(718.55, 874.43) * mm});
            skLineSegment(sketch, "E1085", {"start": v(892.04, -375) * mm, "end": v(886.96, -376.27) * mm});
            skLineSegment(sketch, "E1086", {"start": v(886.96, -376.27) * mm, "end": v(881.88, -376.27) * mm});
            skLineSegment(sketch, "E1087", {"start": v(881.88, -376.27) * mm, "end": v(875.53, -377.54) * mm});
            skLineSegment(sketch, "E1088", {"start": v(875.53, -377.54) * mm, "end": v(870.45, -378.81) * mm});
            skLineSegment(sketch, "E1089", {"start": v(870.45, -378.81) * mm, "end": v(865.37, -378.81) * mm});
            skLineSegment(sketch, "E1090", {"start": v(865.37, -378.81) * mm, "end": v(859.02, -380.08) * mm});
            skLineSegment(sketch, "E1091", {"start": v(859.02, -380.08) * mm, "end": v(853.94, -382.62) * mm});
            skLineSegment(sketch, "E1092", {"start": v(853.94, -382.62) * mm, "end": v(850.13, -383.9) * mm});
            skLineSegment(sketch, "E1093", {"start": v(850.13, -383.9) * mm, "end": v(845.05, -385.16) * mm});
            skLineSegment(sketch, "E1094", {"start": v(845.05, -385.16) * mm, "end": v(829.8, -392.78) * mm});
            skLineSegment(sketch, "E1095", {"start": v(829.8, -392.78) * mm, "end": v(824.73, -394.05) * mm});
            skLineSegment(sketch, "E1096", {"start": v(824.73, -394.05) * mm, "end": v(817.1, -397.86) * mm});
            skLineSegment(sketch, "E1097", {"start": v(817.1, -397.86) * mm, "end": v(812.03, -401.67) * mm});
            skLineSegment(sketch, "E1098", {"start": v(812.03, -401.67) * mm, "end": v(805.68, -405.48) * mm});
            skLineSegment(sketch, "E1099", {"start": v(805.68, -405.48) * mm, "end": v(801.87, -409.3) * mm});
            skLineSegment(sketch, "E1100", {"start": v(801.87, -409.3) * mm, "end": v(796.79, -413.1) * mm});
            skLineSegment(sketch, "E1101", {"start": v(796.79, -413.1) * mm, "end": v(790.44, -416.91) * mm});
            skLineSegment(sketch, "E1102", {"start": v(790.44, -416.91) * mm, "end": v(785.36, -420.72) * mm});
            skLineSegment(sketch, "E1103", {"start": v(785.36, -420.72) * mm, "end": v(781.55, -424.53) * mm});
            skLineSegment(sketch, "E1104", {"start": v(781.55, -424.53) * mm, "end": v(771.39, -432.15) * mm});
            skLineSegment(sketch, "E1105", {"start": v(771.39, -432.15) * mm, "end": v(767.58, -437.23) * mm});
            skLineSegment(sketch, "E1106", {"start": v(767.58, -437.23) * mm, "end": v(762.5, -442.31) * mm});
            skLineSegment(sketch, "E1107", {"start": v(762.5, -442.31) * mm, "end": v(751.07, -457.55) * mm});
            skLineSegment(sketch, "E1108", {"start": v(751.07, -457.55) * mm, "end": v(688.43, -528.95) * mm});
            skLineSegment(sketch, "E1109", {"start": v(688.43, -528.95) * mm, "end": v(568.9, -650.54) * mm});
            skLineSegment(sketch, "E1110", {"start": v(568.9, -650.54) * mm, "end": v(444.49, -781.88) * mm});
            skLineSegment(sketch, "E1111", {"start": v(444.49, -781.88) * mm, "end": v(304.6, -917.98) * mm});
            skLineSegment(sketch, "E1112", {"start": v(304.6, -917.98) * mm, "end": v(234.05, -977.74) * mm});
            skLineSegment(sketch, "E1113", {"start": v(234.05, -977.74) * mm, "end": v(135.14, -1045.59) * mm});
            skLineSegment(sketch, "E1114", {"start": v(135.14, -1045.59) * mm, "end": v(-119.7, -1200.17) * mm});
            skLineSegment(sketch, "E1115", {"start": v(-119.7, -1200.17) * mm, "end": v(-356.78, -1350.56) * mm});
            skLineSegment(sketch, "E1116", {"start": v(-356.78, -1350.56) * mm, "end": v(-495.36, -1434.54) * mm});
            skLineSegment(sketch, "E1117", {"start": v(-495.36, -1434.54) * mm, "end": v(-542.84, -1463.16) * mm});
            skLineSegment(sketch, "E1118", {"start": v(-542.84, -1463.16) * mm, "end": v(-600.09, -1510.05) * mm});
            skLineSegment(sketch, "E1119", {"start": v(-600.09, -1510.05) * mm, "end": v(-711.67, -1599.05) * mm});
            skLineSegment(sketch, "E1120", {"start": v(-711.67, -1599.05) * mm, "end": v(-837.02, -1701.57) * mm});
            skLineSegment(sketch, "E1121", {"start": v(-837.02, -1701.57) * mm, "end": v(-1278.4, -1979.01) * mm});
            skLineSegment(sketch, "E1122", {"start": v(-1278.4, -1979.01) * mm, "end": v(-1398.54, -2054.7) * mm});
            skLineSegment(sketch, "E1123", {"start": v(-1398.54, -2054.7) * mm, "end": v(-1554.5, -2140.3) * mm});
            skLineSegment(sketch, "E1124", {"start": v(-1554.5, -2140.3) * mm, "end": v(-1711.97, -2214.98) * mm});
            skLineSegment(sketch, "E1125", {"start": v(-1711.97, -2214.98) * mm, "end": v(-1717.3, -2217.77) * mm});
            skLineSegment(sketch, "E1126", {"start": v(-1717.3, -2217.77) * mm, "end": v(-1722.39, -2220.56) * mm});
            skLineSegment(sketch, "E1127", {"start": v(-1722.39, -2220.56) * mm, "end": v(-1727.47, -2223.87) * mm});
            skLineSegment(sketch, "E1128", {"start": v(-1727.47, -2223.87) * mm, "end": v(-1732.55, -2227.17) * mm});
            skLineSegment(sketch, "E1129", {"start": v(-1732.55, -2227.17) * mm, "end": v(-1737.37, -2230.47) * mm});
            skLineSegment(sketch, "E1130", {"start": v(-1737.37, -2230.47) * mm, "end": v(-1741.94, -2234.28) * mm});
            skLineSegment(sketch, "E1131", {"start": v(-1741.94, -2234.28) * mm, "end": v(-1746.52, -2238.34) * mm});
            skLineSegment(sketch, "E1132", {"start": v(-1746.52, -2238.34) * mm, "end": v(-1750.83, -2242.4) * mm});
            skLineSegment(sketch, "E1133", {"start": v(-1750.83, -2242.4) * mm, "end": v(-1754.9, -2246.47) * mm});
            skLineSegment(sketch, "E1134", {"start": v(-1754.9, -2246.47) * mm, "end": v(-1758.96, -2251.04) * mm});
            skLineSegment(sketch, "E1135", {"start": v(-1758.96, -2251.04) * mm, "end": v(-1762.77, -2255.62) * mm});
            skLineSegment(sketch, "E1136", {"start": v(-1762.77, -2255.62) * mm, "end": v(-1766.58, -2260.44) * mm});
            skLineSegment(sketch, "E1137", {"start": v(-1766.58, -2260.44) * mm, "end": v(-1769.88, -2265.27) * mm});
            skLineSegment(sketch, "E1138", {"start": v(-1769.88, -2265.27) * mm, "end": v(-1773.19, -2270.35) * mm});
            skLineSegment(sketch, "E1139", {"start": v(-1773.19, -2270.35) * mm, "end": v(-1776.23, -2275.43) * mm});
            skLineSegment(sketch, "E1140", {"start": v(-1776.23, -2275.43) * mm, "end": v(-1779.03, -2280.76) * mm});
            skLineSegment(sketch, "E1141", {"start": v(3122.16, 1062.64) * mm, "end": v(3112, 1058.83) * mm});
            skLineSegment(sketch, "E1142", {"start": v(3112, 1058.83) * mm, "end": v(3104.38, 1056.29) * mm});
            skLineSegment(sketch, "E1143", {"start": v(3104.38, 1056.29) * mm, "end": v(3098.03, 1055.02) * mm});
            skLineSegment(sketch, "E1144", {"start": v(3098.03, 1055.02) * mm, "end": v(3080.25, 1052.48) * mm});
            skLineSegment(sketch, "E1145", {"start": v(3080.25, 1052.48) * mm, "end": v(3062.47, 1053.75) * mm});
            skLineSegment(sketch, "E1146", {"start": v(3062.47, 1053.75) * mm, "end": v(3049.77, 1055.02) * mm});
            skLineSegment(sketch, "E1147", {"start": v(3049.77, 1055.02) * mm, "end": v(3024.37, 1063.9) * mm});
            skLineSegment(sketch, "E1148", {"start": v(3024.37, 1063.9) * mm, "end": v(3002.78, 1077.88) * mm});
            skLineSegment(sketch, "E1149", {"start": v(3002.78, 1077.88) * mm, "end": v(2978.65, 1095.66) * mm});
            skLineSegment(sketch, "E1150", {"start": v(2978.65, 1095.66) * mm, "end": v(2941.82, 1133.76) * mm});
            skLineSegment(sketch, "E1151", {"start": v(2941.82, 1133.76) * mm, "end": v(2913.88, 1166.78) * mm});
            skLineSegment(sketch, "E1152", {"start": v(2913.88, 1166.78) * mm, "end": v(2880.86, 1218.85) * mm});
            skLineSegment(sketch, "E1153", {"start": v(2880.86, 1218.85) * mm, "end": v(2866.89, 1245.52) * mm});
            skLineSegment(sketch, "E1154", {"start": v(2866.89, 1245.52) * mm, "end": v(2841.49, 1305.2) * mm});
            skLineSegment(sketch, "E1155", {"start": v(2841.49, 1305.2) * mm, "end": v(2630.67, 1928.78) * mm});
            skLineSegment(sketch, "E1156", {"start": v(2630.67, 1928.78) * mm, "end": v(2613.75, 1979.53) * mm});
            skLineSegment(sketch, "E1157", {"start": v(-565.92, -1884.37) * mm, "end": v(-540.04, -1874.92) * mm});
            skLineSegment(sketch, "E1158", {"start": v(2825.36, -2475.4) * mm, "end": v(3033.26, -2334.61) * mm});
            skLineSegment(sketch, "E1159", {"start": v(815.58, 642.78) * mm, "end": v(673.85, 574.2) * mm});
            skLineSegment(sketch, "E1160", {"start": v(673.85, 574.2) * mm, "end": v(454.9, 422.05) * mm});
            skLineSegment(sketch, "E1161", {"start": v(454.9, 422.05) * mm, "end": v(415.79, 478.44) * mm});
            skLineSegment(sketch, "E1162", {"start": v(415.79, 478.44) * mm, "end": v(372.96, 448.65) * mm});
            skLineSegment(sketch, "E1163", {"start": v(-508.5, -1462.04) * mm, "end": v(-122.77, -1219.98) * mm});
            skLineSegment(sketch, "E1164", {"start": v(1321.85, -1571.31) * mm, "end": v(1385.74, -1531.41) * mm});
            skLineSegment(sketch, "E1165", {"start": v(1385.74, -1531.41) * mm, "end": v(1317.13, -1421.58) * mm});
            skLineSegment(sketch, "E1166", {"start": v(1317.13, -1421.58) * mm, "end": v(1253.25, -1461.49) * mm});
            skLineSegment(sketch, "E1167", {"start": v(2799.96, 2140.34) * mm, "end": v(2729.85, 2190.22) * mm});
            skLineSegment(sketch, "E1168", {"start": v(337.38, 335.77) * mm, "end": v(310.17, 207.22) * mm});
            skLineSegment(sketch, "E1169", {"start": v(2780.07, 2501.45) * mm, "end": v(2876.3, 2438.23) * mm});
            skLineSegment(sketch, "E1170", {"start": v(2876.3, 2438.23) * mm, "end": v(2814.05, 2343.49) * mm});
            skLineSegment(sketch, "E1171", {"start": v(2814.05, 2343.49) * mm, "end": v(2717.84, 2406.7) * mm});
            skLineSegment(sketch, "E1172", {"start": v(2717.84, 2406.7) * mm, "end": v(2780.07, 2501.45) * mm});
            skLineSegment(sketch, "E1173", {"start": v(1391.5, -1238.52) * mm, "end": v(1302.12, -1319.27) * mm});
            skLineSegment(sketch, "E1174", {"start": v(1302.12, -1319.27) * mm, "end": v(1364.5, -1388.3) * mm});
            skLineSegment(sketch, "E1175", {"start": v(1364.5, -1388.3) * mm, "end": v(1453.88, -1307.56) * mm});
            skLineSegment(sketch, "E1176", {"start": v(1453.88, -1307.56) * mm, "end": v(1391.5, -1238.52) * mm});
            skLineSegment(sketch, "E1177", {"start": v(-732.04, -1740.53) * mm, "end": v(-716.01, -1766.46) * mm});
            skLineSegment(sketch, "E1178", {"start": v(2510.07, 1098.3) * mm, "end": v(2438.9, 1122.33) * mm});
            skLineSegment(sketch, "E1179", {"start": v(2438.9, 1122.33) * mm, "end": v(2478.62, 1155.45) * mm});
            skLineSegment(sketch, "E1180", {"start": v(-482.08, -1854.35) * mm, "end": v(-462.45, -1847) * mm});
            skLineSegment(sketch, "E1181", {"start": v(2708, 1935.4) * mm, "end": v(2703.06, 1928.78) * mm});
            skLineSegment(sketch, "E1182", {"start": v(2703.06, 1928.78) * mm, "end": v(2690.36, 1914.8) * mm});
            skLineSegment(sketch, "E1183", {"start": v(2690.36, 1914.8) * mm, "end": v(2713.22, 1895.76) * mm});
            skLineSegment(sketch, "E1184", {"start": v(2713.22, 1895.76) * mm, "end": v(2699.25, 1870.36) * mm});
            skLineSegment(sketch, "E1185", {"start": v(2699.25, 1870.36) * mm, "end": v(2706.87, 1805.59) * mm});
            skLineSegment(sketch, "E1186", {"start": v(2706.87, 1805.59) * mm, "end": v(2774.18, 1759.87) * mm});
            skLineSegment(sketch, "E1187", {"start": v(2774.18, 1759.87) * mm, "end": v(2831.33, 1771.3) * mm});
            skLineSegment(sketch, "E1188", {"start": v(2831.33, 1771.3) * mm, "end": v(2847.84, 1795.43) * mm});
            skLineSegment(sketch, "E1189", {"start": v(2847.84, 1795.43) * mm, "end": v(2863.58, 1786.03) * mm});
            skLineSegment(sketch, "E1190", {"start": v(415.28, -2384.9) * mm, "end": v(431.03, -2409.54) * mm});
            skLineSegment(sketch, "E1191", {"start": v(310.17, 207.22) * mm, "end": v(306.57, 190.15) * mm});
            skLineSegment(sketch, "E1192", {"start": v(306.57, 190.15) * mm, "end": v(241.8, 205.39) * mm});
            skLineSegment(sketch, "E1193", {"start": v(241.8, 205.39) * mm, "end": v(225.29, 125.38) * mm});
            skLineSegment(sketch, "E1194", {"start": v(225.29, 125.38) * mm, "end": v(207.99, 42.83) * mm});
            skLineSegment(sketch, "E1195", {"start": v(207.99, 42.83) * mm, "end": v(159.88, 11.77) * mm});
            skLineSegment(sketch, "E1196", {"start": v(159.88, 11.77) * mm, "end": v(144, -67.66) * mm});
            skLineSegment(sketch, "E1197", {"start": v(2760.18, -2519.52) * mm, "end": v(2745.52, -2499.66) * mm});
            skLineSegment(sketch, "E1198", {"start": v(372.96, 448.65) * mm, "end": v(398.49, 419.87) * mm});
            skLineSegment(sketch, "E1199", {"start": v(398.49, 419.87) * mm, "end": v(379.18, 326.65) * mm});
            skLineSegment(sketch, "E1200", {"start": v(1494.02, -1846.93) * mm, "end": v(1321.85, -1571.31) * mm});
            skLineSegment(sketch, "E1201", {"start": v(2745.52, -2499.66) * mm, "end": v(2729.06, -2477.36) * mm});
            skLineSegment(sketch, "E1202", {"start": v(2729.06, -2477.36) * mm, "end": v(2770.14, -2448.05) * mm});
            skLineSegment(sketch, "E1203", {"start": v(2770.14, -2448.05) * mm, "end": v(2785.7, -2470.7) * mm});
            skLineSegment(sketch, "E1204", {"start": v(2785.7, -2470.7) * mm, "end": v(2745.52, -2499.66) * mm});
            skLineSegment(sketch, "E1205", {"start": v(408.93, -2535.02) * mm, "end": v(484.37, -2492.1) * mm});
            skLineSegment(sketch, "E1206", {"start": v(2700.85, -2480.28) * mm, "end": v(2612.3, -2492.37) * mm});
            skLineSegment(sketch, "E1207", {"start": v(2612.3, -2492.37) * mm, "end": v(2430.49, -2618.25) * mm});
            skLineSegment(sketch, "E1208", {"start": v(2430.49, -2618.25) * mm, "end": v(2276.2, -2396.97) * mm});
            skLineSegment(sketch, "E1209", {"start": v(2276.2, -2396.97) * mm, "end": v(2459.55, -2272.81) * mm});
            skLineSegment(sketch, "E1210", {"start": v(2459.55, -2272.81) * mm, "end": v(2407.4, -2195.8) * mm});
            skLineSegment(sketch, "E1211", {"start": v(2407.4, -2195.8) * mm, "end": v(2671.3, -2017.11) * mm});
            skLineSegment(sketch, "E1212", {"start": v(-326.12, -456.92) * mm, "end": v(-286.52, -429.61) * mm});
            skLineSegment(sketch, "E1213", {"start": v(-286.52, -429.61) * mm, "end": v(-245.88, -486.76) * mm});
            skLineSegment(sketch, "E1214", {"start": v(-245.88, -486.76) * mm, "end": v(-242.07, -491.84) * mm});
            skLineSegment(sketch, "E1215", {"start": v(-465.6, -725.52) * mm, "end": v(-504.96, -667.1) * mm});
            skLineSegment(sketch, "E1216", {"start": v(-504.96, -667.1) * mm, "end": v(-544.33, -607.41) * mm});
            skLineSegment(sketch, "E1217", {"start": v(-544.33, -607.41) * mm, "end": v(-501.4, -577.82) * mm});
            skLineSegment(sketch, "E1218", {"start": v(2700.85, -2480.28) * mm, "end": v(2694.44, -2470.86) * mm});
            skLineSegment(sketch, "E1219", {"start": v(2694.44, -2470.86) * mm, "end": v(2781.44, -2410.94) * mm});
            skLineSegment(sketch, "E1220", {"start": v(2781.44, -2410.94) * mm, "end": v(2825.36, -2475.4) * mm});
            skLineSegment(sketch, "E1221", {"start": v(756.15, -561.7) * mm, "end": v(834.89, -481.68) * mm});
            skLineSegment(sketch, "E1222", {"start": v(834.89, -481.68) * mm, "end": v(842.5, -476.6) * mm});
            skLineSegment(sketch, "E1223", {"start": v(842.5, -476.6) * mm, "end": v(847.59, -472.8) * mm});
            skLineSegment(sketch, "E1224", {"start": v(847.59, -472.8) * mm, "end": v(851.4, -470.25) * mm});
            skLineSegment(sketch, "E1225", {"start": v(851.4, -470.25) * mm, "end": v(853.94, -467.71) * mm});
            skLineSegment(sketch, "E1226", {"start": v(853.94, -467.71) * mm, "end": v(861.56, -462.63) * mm});
            skLineSegment(sketch, "E1227", {"start": v(861.56, -462.63) * mm, "end": v(866.64, -460.1) * mm});
            skLineSegment(sketch, "E1228", {"start": v(866.64, -460.1) * mm, "end": v(871.72, -458.82) * mm});
            skLineSegment(sketch, "E1229", {"start": v(-474.48, -1811.37) * mm, "end": v(-462.45, -1847) * mm});
            skLineSegment(sketch, "E1230", {"start": v(2613.75, 1979.53) * mm, "end": v(2720.2, 2127.2) * mm});
            skLineSegment(sketch, "E1231", {"start": v(2760.18, -2519.52) * mm, "end": v(2825.36, -2475.4) * mm});
            skLineSegment(sketch, "E1232", {"start": v(1285, 461.24) * mm, "end": v(1273.87, 472.4) * mm});
            skLineSegment(sketch, "E1233", {"start": v(1273.87, 472.4) * mm, "end": v(1217.49, 416.13) * mm});
            skLineSegment(sketch, "E1234", {"start": v(1217.49, 416.13) * mm, "end": v(1229.2, 404.4) * mm});
            skLineSegment(sketch, "E1235", {"start": v(2760.18, -2519.52) * mm, "end": v(2737.68, -2534.81) * mm});
            skLineSegment(sketch, "E1236", {"start": v(2737.68, -2534.81) * mm, "end": v(2700.85, -2480.28) * mm});
            skLineSegment(sketch, "E1237", {"start": v(1321.85, -1571.31) * mm, "end": v(1253.25, -1461.49) * mm});
            skLineSegment(sketch, "E1238", {"start": v(2879.59, -744.57) * mm, "end": v(3005.32, -833.47) * mm});
            skLineSegment(sketch, "E1239", {"start": v(3005.32, -833.47) * mm, "end": v(2964.68, -882.5) * mm});
            skLineSegment(sketch, "E1240", {"start": v(2964.68, -882.5) * mm, "end": v(2657.59, -1253.84) * mm});
            skLineSegment(sketch, "E1241", {"start": v(2657.59, -1253.84) * mm, "end": v(2572.25, -1357.98) * mm});
            skLineSegment(sketch, "E1242", {"start": v(2577, 1075.72) * mm, "end": v(2510.07, 1098.3) * mm});
            skLineSegment(sketch, "E1243", {"start": v(-501.4, -577.82) * mm, "end": v(-326.12, -456.92) * mm});
            skLineSegment(sketch, "E1244", {"start": v(2623.96, 1104.35) * mm, "end": v(2638.29, 1055.02) * mm});
            skLineSegment(sketch, "E1245", {"start": v(2638.29, 1055.02) * mm, "end": v(2577, 1075.72) * mm});
            skLineSegment(sketch, "E1246", {"start": v(913.3, -537.71) * mm, "end": v(923.79, -532.48) * mm});
            skLineSegment(sketch, "E1247", {"start": v(923.79, -532.48) * mm, "end": v(927.6, -531.21) * mm});
            skLineSegment(sketch, "E1248", {"start": v(927.6, -531.21) * mm, "end": v(932.68, -529.94) * mm});
            skLineSegment(sketch, "E1249", {"start": v(932.68, -529.94) * mm, "end": v(939.03, -529.94) * mm});
            skLineSegment(sketch, "E1250", {"start": v(939.03, -529.94) * mm, "end": v(941.57, -528.67) * mm});
            skLineSegment(sketch, "E1251", {"start": v(941.57, -528.67) * mm, "end": v(964.43, -528.67) * mm});
            skLineSegment(sketch, "E1252", {"start": v(964.43, -528.67) * mm, "end": v(968.24, -529.94) * mm});
            skLineSegment(sketch, "E1253", {"start": v(968.24, -529.94) * mm, "end": v(972.05, -529.94) * mm});
            skLineSegment(sketch, "E1254", {"start": v(972.05, -529.94) * mm, "end": v(974.59, -531.21) * mm});
            skLineSegment(sketch, "E1255", {"start": v(974.59, -531.21) * mm, "end": v(980.94, -532.48) * mm});
            skLineSegment(sketch, "E1256", {"start": v(980.94, -532.48) * mm, "end": v(988.56, -536.3) * mm});
            skLineSegment(sketch, "E1257", {"start": v(988.56, -536.3) * mm, "end": v(991.1, -538.83) * mm});
            skLineSegment(sketch, "E1258", {"start": v(991.1, -538.83) * mm, "end": v(996.18, -541.37) * mm});
            skLineSegment(sketch, "E1259", {"start": v(996.18, -541.37) * mm, "end": v(1024.12, -569.31) * mm});
            skLineSegment(sketch, "E1260", {"start": v(431.03, -2409.54) * mm, "end": v(484.37, -2492.1) * mm});
            skLineSegment(sketch, "E1261", {"start": v(1229.2, 404.4) * mm, "end": v(1240.04, 393.58) * mm});
            skLineSegment(sketch, "E1262", {"start": v(1240.04, 393.58) * mm, "end": v(1240.55, 393.1) * mm});
            skLineSegment(sketch, "E1263", {"start": v(1240.55, 393.1) * mm, "end": v(1296.94, 449.36) * mm});
            skLineSegment(sketch, "E1264", {"start": v(1296.94, 449.36) * mm, "end": v(1296.43, 449.84) * mm});
            skLineSegment(sketch, "E1265", {"start": v(1296.43, 449.84) * mm, "end": v(1285, 461.24) * mm});
            skLineSegment(sketch, "E1266", {"start": v(2521.2, 1190.9) * mm, "end": v(2583.68, 1242.98) * mm});
            skLineSegment(sketch, "E1267", {"start": v(2583.68, 1242.98) * mm, "end": v(2602.83, 1177.07) * mm});
            skLineSegment(sketch, "E1268", {"start": v(-3188.73, -2503.09) * mm, "end": v(-3175.27, -2502.25) * mm});
            skLineSegment(sketch, "E1269", {"start": v(372.96, 448.65) * mm, "end": v(357.37, 437.8) * mm});
            skLineSegment(sketch, "E1270", {"start": v(357.37, 437.8) * mm, "end": v(343.4, 364.14) * mm});
            skLineSegment(sketch, "E1271", {"start": v(343.4, 364.14) * mm, "end": v(337.38, 335.77) * mm});
            skLineSegment(sketch, "E1272", {"start": v(913.3, -537.71) * mm, "end": v(871.72, -458.82) * mm});
            skLineSegment(sketch, "E1273", {"start": v(2720.2, 2127.2) * mm, "end": v(2766.94, 2093.96) * mm});
            skLineSegment(sketch, "E1274", {"start": v(2766.94, 2093.96) * mm, "end": v(2799.96, 2140.34) * mm});
            skLineSegment(sketch, "E1275", {"start": v(1724.04, -1674.29) * mm, "end": v(1709.43, -1651.58) * mm});
            skLineSegment(sketch, "E1276", {"start": v(1709.43, -1651.58) * mm, "end": v(1780.04, -1605.68) * mm});
            skLineSegment(sketch, "E1277", {"start": v(2729.85, 2190.22) * mm, "end": v(2694.55, 2216.33) * mm});
            skLineSegment(sketch, "E1278", {"start": v(2694.55, 2216.33) * mm, "end": v(2581.85, 2075.21) * mm});
            skLineSegment(sketch, "E1279", {"start": v(379.18, 326.65) * mm, "end": v(353.66, 197.62) * mm});
            skLineSegment(sketch, "E1280", {"start": v(353.66, 197.62) * mm, "end": v(310.17, 207.22) * mm});
            skLineSegment(sketch, "E1281", {"start": v(-2686.82, 1616.36) * mm, "end": v(-2890.02, 1654.46) * mm});
            skLineSegment(sketch, "E1282", {"start": v(-2890.02, 1654.46) * mm, "end": v(-2910.34, 1658.27) * mm});
            skLineSegment(sketch, "E1283", {"start": v(-2910.34, 1658.27) * mm, "end": v(-2997.97, 1613.82) * mm});
            skLineSegment(sketch, "E1284", {"start": v(-2997.97, 1613.82) * mm, "end": v(-3184.66, 1517.3) * mm});
            skLineSegment(sketch, "E1285", {"start": v(-3184.66, 1517.3) * mm, "end": v(-3188.73, 1515.19) * mm});
            skLineSegment(sketch, "E1286", {"start": v(-2589.03, 1570.64) * mm, "end": v(-2549.66, 1754.79) * mm});
            skLineSegment(sketch, "E1287", {"start": v(-2549.66, 1754.79) * mm, "end": v(-2453.14, 1817.02) * mm});
            skLineSegment(sketch, "E1288", {"start": v(-2453.14, 1817.02) * mm, "end": v(-2286.77, 1928.78) * mm});
            skLineSegment(sketch, "E1289", {"start": v(-2286.77, 1928.78) * mm, "end": v(-2258.83, 1951.64) * mm});
            skLineSegment(sketch, "E1290", {"start": v(-2258.83, 1951.64) * mm, "end": v(-2255.02, 1955.45) * mm});
            skLineSegment(sketch, "E1291", {"start": v(-2255.02, 1955.45) * mm, "end": v(-2247.4, 1959.26) * mm});
            skLineSegment(sketch, "E1292", {"start": v(-2247.4, 1959.26) * mm, "end": v(-2242.32, 1959.26) * mm});
            skLineSegment(sketch, "E1293", {"start": v(-2242.32, 1959.26) * mm, "end": v(-2239.78, 1961.8) * mm});
            skLineSegment(sketch, "E1294", {"start": v(-2239.78, 1961.8) * mm, "end": v(-2225.81, 1961.8) * mm});
            skLineSegment(sketch, "E1295", {"start": v(-2225.81, 1961.8) * mm, "end": v(-2223.27, 1959.26) * mm});
            skLineSegment(sketch, "E1296", {"start": v(-2223.27, 1959.26) * mm, "end": v(-2219.46, 1959.26) * mm});
            skLineSegment(sketch, "E1297", {"start": v(-2219.46, 1959.26) * mm, "end": v(-2216.92, 1956.72) * mm});
            skLineSegment(sketch, "E1298", {"start": v(-2216.92, 1956.72) * mm, "end": v(-2214.38, 1955.45) * mm});
            skLineSegment(sketch, "E1299", {"start": v(-2214.38, 1955.45) * mm, "end": v(-2210.57, 1952.9) * mm});
            skLineSegment(sketch, "E1300", {"start": v(-2210.57, 1952.9) * mm, "end": v(-2206.76, 1951.64) * mm});
            skLineSegment(sketch, "E1301", {"start": v(-2206.76, 1951.64) * mm, "end": v(-2183.9, 1928.78) * mm});
            skLineSegment(sketch, "E1302", {"start": v(-2183.9, 1928.78) * mm, "end": v(-2168.66, 1906.94) * mm});
            skLineSegment(sketch, "E1303", {"start": v(-2168.66, 1906.94) * mm, "end": v(-2135.64, 1928.78) * mm});
            skLineSegment(sketch, "E1304", {"start": v(-2135.64, 1928.78) * mm, "end": v(-2082.3, 1963.07) * mm});
            skLineSegment(sketch, "E1305", {"start": v(-2082.3, 1963.07) * mm, "end": v(-1929.9, 2074.83) * mm});
            skLineSegment(sketch, "E1306", {"start": v(-1929.9, 2074.83) * mm, "end": v(-1842.27, 2134.52) * mm});
            skLineSegment(sketch, "E1307", {"start": v(-3175.27, -2502.25) * mm, "end": v(-3139.2, -2498.7) * mm});
            skLineSegment(sketch, "E1308", {"start": v(-3139.2, -2498.7) * mm, "end": v(-2779.53, -2464.15) * mm});
            skLineSegment(sketch, "E1309", {"start": v(-3007.12, -1870.04) * mm, "end": v(-3051.31, -1724.73) * mm});
            skLineSegment(sketch, "E1310", {"start": v(-3051.31, -1724.73) * mm, "end": v(-2961.22, -1697.32) * mm});
            skLineSegment(sketch, "E1311", {"start": v(-2961.22, -1697.32) * mm, "end": v(-2976.2, -1648.02) * mm});
            skLineSegment(sketch, "E1312", {"start": v(-2976.2, -1648.02) * mm, "end": v(-3066.3, -1675.43) * mm});
            skLineSegment(sketch, "E1313", {"start": v(-3066.3, -1675.43) * mm, "end": v(-3151.64, -1394.81) * mm});
            skLineSegment(sketch, "E1314", {"start": v(-3151.64, -1394.81) * mm, "end": v(-2902.3, -1313.8) * mm});
            skLineSegment(sketch, "E1315", {"start": v(-2902.3, -1313.8) * mm, "end": v(-2840.37, -1293.7) * mm});
            skLineSegment(sketch, "E1316", {"start": v(-2840.37, -1293.7) * mm, "end": v(-2875.34, -1198.21) * mm});
            skLineSegment(sketch, "E1317", {"start": v(-2875.34, -1198.21) * mm, "end": v(-2834.14, -1178.91) * mm});
            skLineSegment(sketch, "E1318", {"start": v(-2834.14, -1178.91) * mm, "end": v(-2582.68, -1714.85) * mm});
            skLineSegment(sketch, "E1319", {"start": v(-2582.68, -1714.85) * mm, "end": v(-2651.26, -1722.47) * mm});
            skLineSegment(sketch, "E1320", {"start": v(-2651.26, -1722.47) * mm, "end": v(-2628.4, -1852.01) * mm});
            skLineSegment(sketch, "E1321", {"start": v(-2770.9, -2553.05) * mm, "end": v(-3133.86, -2578.45) * mm});
            skLineSegment(sketch, "E1322", {"start": v(-3133.86, -2578.45) * mm, "end": v(-3168.92, -2581) * mm});
            skLineSegment(sketch, "E1323", {"start": v(1253.25, -1461.49) * mm, "end": v(1191.76, -1363.06) * mm});
            skLineSegment(sketch, "E1324", {"start": v(1191.76, -1363.06) * mm, "end": v(1481.32, -1086.2) * mm});
            skLineSegment(sketch, "E1325", {"start": v(408.93, -2535.02) * mm, "end": v(361.18, -2457.8) * mm});
            skLineSegment(sketch, "E1326", {"start": v(823.46, -629) * mm, "end": v(902.2, -547.72) * mm});
            skLineSegment(sketch, "E1327", {"start": v(902.2, -547.72) * mm, "end": v(911.09, -538.83) * mm});
            skLineSegment(sketch, "E1328", {"start": v(911.09, -538.83) * mm, "end": v(913.3, -537.71) * mm});
            skLineSegment(sketch, "E1329", {"start": v(2008.37, 2107.85) * mm, "end": v(2012.58, 2095.2) * mm});
            skLineSegment(sketch, "E1330", {"start": v(2012.58, 2095.2) * mm, "end": v(1969.55, 2081.56) * mm});
            skLineSegment(sketch, "E1331", {"start": v(1969.55, 2081.56) * mm, "end": v(1981.29, 2044.5) * mm});
            skLineSegment(sketch, "E1332", {"start": v(1981.29, 2044.5) * mm, "end": v(1892.8, 2016.4) * mm});
            skLineSegment(sketch, "E1333", {"start": v(431.03, -2409.54) * mm, "end": v(361.18, -2457.8) * mm});
            skLineSegment(sketch, "E1334", {"start": v(2720.2, 2127.2) * mm, "end": v(2753.22, 2173.61) * mm});
            skLineSegment(sketch, "E1335", {"start": v(407.73, -2425.62) * mm, "end": v(462.32, -2504.64) * mm});
            skLineSegment(sketch, "E1336", {"start": v(384.47, -2441.72) * mm, "end": v(437.63, -2518.68) * mm});
            skLineSegment(sketch, "E1337", {"start": v(2602.83, 1177.07) * mm, "end": v(2623.96, 1104.35) * mm});
            skLineSegment(sketch, "E1338", {"start": v(473.04, -771.62) * mm, "end": v(318.99, -919.3) * mm});
            skLineSegment(sketch, "E1339", {"start": v(318.99, -919.3) * mm, "end": v(293.59, -944.7) * mm});
            skLineSegment(sketch, "E1340", {"start": v(293.59, -944.7) * mm, "end": v(252.95, -982.8) * mm});
            skLineSegment(sketch, "E1341", {"start": v(252.95, -982.8) * mm, "end": v(178.02, -1037.4) * mm});
            skLineSegment(sketch, "E1342", {"start": v(144, -67.66) * mm, "end": v(53.84, -49.88) * mm});
            skLineSegment(sketch, "E1343", {"start": v(53.84, -49.88) * mm, "end": v(110.99, 226.98) * mm});
            skLineSegment(sketch, "E1344", {"start": v(110.99, 226.98) * mm, "end": v(4.3, 248.57) * mm});
            skLineSegment(sketch, "E1345", {"start": v(4.3, 248.57) * mm, "end": v(156.45, 990) * mm});
            skLineSegment(sketch, "E1346", {"start": v(156.45, 990) * mm, "end": v(581.3, 902.65) * mm});
            skLineSegment(sketch, "E1347", {"start": v(2743.57, 2110.6) * mm, "end": v(2776.59, 2156.97) * mm});
            skLineSegment(sketch, "E1348", {"start": v(2766.94, 2093.96) * mm, "end": v(2673.16, 1960.96) * mm});
            skLineSegment(sketch, "E1349", {"start": v(2673.16, 1960.96) * mm, "end": v(2708, 1935.4) * mm});
            skLineSegment(sketch, "E1350", {"start": v(2478.62, 1155.45) * mm, "end": v(2521.2, 1190.9) * mm});
            skLineSegment(sketch, "E1351", {"start": v(2613.75, 1979.53) * mm, "end": v(2581.85, 2075.21) * mm});
            skLineSegment(sketch, "E1352", {"start": v(2696.83, 2143.84) * mm, "end": v(2720.2, 2127.2) * mm});
            skLineSegment(sketch, "E1353", {"start": v(581.3, 902.65) * mm, "end": v(572.48, 845.67) * mm});
            skLineSegment(sketch, "E1354", {"start": v(572.48, 845.67) * mm, "end": v(443.2, 870.2) * mm});
            skLineSegment(sketch, "E1355", {"start": v(-658.74, -1699.05) * mm, "end": v(-589.93, -1808.86) * mm});
            skLineSegment(sketch, "E1356", {"start": v(-589.93, -1808.86) * mm, "end": v(-519.3, -1764.6) * mm});
            skLineSegment(sketch, "E1357", {"start": v(-519.3, -1764.6) * mm, "end": v(-588.07, -1654.78) * mm});
            skLineSegment(sketch, "E1358", {"start": v(-588.07, -1654.78) * mm, "end": v(-658.74, -1699.05) * mm});
            skLineSegment(sketch, "E1359", {"start": v(1061.2, -643.22) * mm, "end": v(1120.13, -590.14) * mm});
            skLineSegment(sketch, "E1360", {"start": v(-462.45, -1847) * mm, "end": v(-450.35, -1882.74) * mm});
            skLineSegment(sketch, "E1361", {"start": v(871.72, -458.82) * mm, "end": v(875.53, -456.28) * mm});
            skLineSegment(sketch, "E1362", {"start": v(875.53, -456.28) * mm, "end": v(880.6, -453.74) * mm});
            skLineSegment(sketch, "E1363", {"start": v(880.6, -453.74) * mm, "end": v(885.69, -452.47) * mm});
            skLineSegment(sketch, "E1364", {"start": v(885.69, -452.47) * mm, "end": v(893.3, -449.93) * mm});
            skLineSegment(sketch, "E1365", {"start": v(893.3, -449.93) * mm, "end": v(898.39, -449.93) * mm});
            skLineSegment(sketch, "E1366", {"start": v(898.39, -449.93) * mm, "end": v(902.2, -448.66) * mm});
            skLineSegment(sketch, "E1367", {"start": v(902.2, -448.66) * mm, "end": v(907.28, -448.66) * mm});
            skLineSegment(sketch, "E1368", {"start": v(907.28, -448.66) * mm, "end": v(909.82, -447.4) * mm});
            skLineSegment(sketch, "E1369", {"start": v(909.82, -447.4) * mm, "end": v(928.87, -447.4) * mm});
            skLineSegment(sketch, "E1370", {"start": v(928.87, -447.4) * mm, "end": v(935.22, -448.66) * mm});
            skLineSegment(sketch, "E1371", {"start": v(935.22, -448.66) * mm, "end": v(940.3, -448.66) * mm});
            skLineSegment(sketch, "E1372", {"start": v(940.3, -448.66) * mm, "end": v(945.38, -449.93) * mm});
            skLineSegment(sketch, "E1373", {"start": v(945.38, -449.93) * mm, "end": v(950.46, -449.93) * mm});
            skLineSegment(sketch, "E1374", {"start": v(950.46, -449.93) * mm, "end": v(960.62, -452.47) * mm});
            skLineSegment(sketch, "E1375", {"start": v(960.62, -452.47) * mm, "end": v(964.43, -453.74) * mm});
            skLineSegment(sketch, "E1376", {"start": v(964.43, -453.74) * mm, "end": v(966.97, -455.01) * mm});
            skLineSegment(sketch, "E1377", {"start": v(966.97, -455.01) * mm, "end": v(970.78, -456.28) * mm});
            skLineSegment(sketch, "E1378", {"start": v(970.78, -456.28) * mm, "end": v(975.86, -458.82) * mm});
            skLineSegment(sketch, "E1379", {"start": v(975.86, -458.82) * mm, "end": v(980.94, -460.1) * mm});
            skLineSegment(sketch, "E1380", {"start": v(980.94, -460.1) * mm, "end": v(984.75, -462.63) * mm});
            skLineSegment(sketch, "E1381", {"start": v(984.75, -462.63) * mm, "end": v(989.83, -465.17) * mm});
            skLineSegment(sketch, "E1382", {"start": v(989.83, -465.17) * mm, "end": v(993.64, -467.71) * mm});
            skLineSegment(sketch, "E1383", {"start": v(993.64, -467.71) * mm, "end": v(998.72, -470.25) * mm});
            skLineSegment(sketch, "E1384", {"start": v(998.72, -470.25) * mm, "end": v(1008.88, -477.87) * mm});
            skLineSegment(sketch, "E1385", {"start": v(1008.88, -477.87) * mm, "end": v(1012.69, -479.14) * mm});
            skLineSegment(sketch, "E1386", {"start": v(1012.69, -479.14) * mm, "end": v(1017.77, -482.95) * mm});
            skLineSegment(sketch, "E1387", {"start": v(1017.77, -482.95) * mm, "end": v(1021.58, -488.03) * mm});
            skLineSegment(sketch, "E1388", {"start": v(1021.58, -488.03) * mm, "end": v(1026.66, -491.84) * mm});
            skLineSegment(sketch, "E1389", {"start": v(1026.66, -491.84) * mm, "end": v(1063.49, -531.21) * mm});
            skLineSegment(sketch, "E1390", {"start": v(1724.04, -1674.29) * mm, "end": v(1754.37, -1655.16) * mm});
            skLineSegment(sketch, "E1391", {"start": v(1754.37, -1655.16) * mm, "end": v(1847.08, -1596.74) * mm});
            skLineSegment(sketch, "E1392", {"start": v(1847.08, -1596.74) * mm, "end": v(1828.03, -1566.26) * mm});
            skLineSegment(sketch, "E1393", {"start": v(1828.03, -1566.26) * mm, "end": v(1980.43, -1467.2) * mm});
            skLineSegment(sketch, "E1394", {"start": v(1819.64, -2015.59) * mm, "end": v(1676.9, -1854.55) * mm});
            skLineSegment(sketch, "E1395", {"start": v(1676.9, -1854.55) * mm, "end": v(1633.72, -1785.97) * mm});
            skLineSegment(sketch, "E1396", {"start": v(1633.72, -1785.97) * mm, "end": v(1647.69, -1722.47) * mm});
            skLineSegment(sketch, "E1397", {"start": v(1647.69, -1722.47) * mm, "end": v(1724.04, -1674.29) * mm});
            skLineSegment(sketch, "E1398", {"start": v(-501.4, -577.82) * mm, "end": v(-452.9, -649.32) * mm});
            skLineSegment(sketch, "E1399", {"start": v(-452.9, -649.32) * mm, "end": v(-426.22, -688.7) * mm});
            skLineSegment(sketch, "E1400", {"start": v(-426.22, -688.7) * mm, "end": v(-300.5, -874.11) * mm});
            skLineSegment(sketch, "E1401", {"start": v(-300.5, -874.11) * mm, "end": v(-115.07, -748.38) * mm});
            skLineSegment(sketch, "E1402", {"start": v(-115.07, -748.38) * mm, "end": v(-245.88, -565.5) * mm});
            skLineSegment(sketch, "E1403", {"start": v(-245.88, -565.5) * mm, "end": v(-267.47, -536.3) * mm});
            skLineSegment(sketch, "E1404", {"start": v(-267.47, -536.3) * mm, "end": v(-326.12, -456.92) * mm});
            skLineSegment(sketch, "E1405", {"start": v(514.85, -1864.71) * mm, "end": v(500.88, -1874.87) * mm});
            skLineSegment(sketch, "E1406", {"start": v(500.88, -1874.87) * mm, "end": v(502.15, -1900.27) * mm});
            skLineSegment(sketch, "E1407", {"start": v(502.15, -1900.27) * mm, "end": v(538.98, -1957.42) * mm});
            skLineSegment(sketch, "E1408", {"start": v(538.98, -1957.42) * mm, "end": v(564.38, -1966.31) * mm});
            skLineSegment(sketch, "E1409", {"start": v(564.38, -1966.31) * mm, "end": v(574.54, -1958.7) * mm});
            skLineSegment(sketch, "E1410", {"start": v(514.85, -1864.71) * mm, "end": v(489.45, -1825.34) * mm});
            skLineSegment(sketch, "E1411", {"start": v(2065.52, -1109.06) * mm, "end": v(1946.14, -1016.35) * mm});
            skLineSegment(sketch, "E1412", {"start": v(1946.14, -1016.35) * mm, "end": v(1901.69, -1053.18) * mm});
            skLineSegment(sketch, "E1413", {"start": v(554.98, -1840.07) * mm, "end": v(615.68, -1934.05) * mm});
            skLineSegment(sketch, "E1414", {"start": v(2217.92, -1609.44) * mm, "end": v(2671.3, -2017.11) * mm});
            skLineSegment(sketch, "E1415", {"start": v(-2101.86, -2616.04) * mm, "end": v(-1967.75, -2573.12) * mm});
            skLineSegment(sketch, "E1416", {"start": v(1453.88, -572.36) * mm, "end": v(1433.06, -612.5) * mm});
            skLineSegment(sketch, "E1417", {"start": v(1433.06, -612.5) * mm, "end": v(1593.08, -777.6) * mm});
            skLineSegment(sketch, "E1418", {"start": v(1593.08, -777.6) * mm, "end": v(1630.92, -759.81) * mm});
            skLineSegment(sketch, "E1419", {"start": v(-84.6, -1298.3) * mm, "end": v(-57.92, -1337.66) * mm});
            skLineSegment(sketch, "E1420", {"start": v(-57.92, -1337.66) * mm, "end": v(-84.6, -1359.25) * mm});
            skLineSegment(sketch, "E1421", {"start": v(-84.6, -1359.25) * mm, "end": v(-69.1, -1384.14) * mm});
            skLineSegment(sketch, "E1422", {"start": v(1459.47, -1008.48) * mm, "end": v(1482.84, -1032.6) * mm});
            skLineSegment(sketch, "E1423", {"start": v(1894.57, 1139.35) * mm, "end": v(1928.36, 1174.4) * mm});
            skLineSegment(sketch, "E1424", {"start": v(2671.3, -2017.11) * mm, "end": v(3033.26, -2334.61) * mm});
            skLineSegment(sketch, "E1425", {"start": v(1819.64, -2015.59) * mm, "end": v(1845.8, -2045.05) * mm});
            skLineSegment(sketch, "E1426", {"start": v(1845.8, -2045.05) * mm, "end": v(1806.44, -2083.15) * mm});
            skLineSegment(sketch, "E1427", {"start": v(1773.16, -2046.57) * mm, "end": v(1806.44, -2083.15) * mm});
            skLineSegment(sketch, "E1428", {"start": v(913.37, -2395.82) * mm, "end": v(956.8, -2366.36) * mm});
            skLineSegment(sketch, "E1429", {"start": v(956.8, -2366.36) * mm, "end": v(942.84, -2344.77) * mm});
            skLineSegment(sketch, "E1430", {"start": v(2146.54, -1169.77) * mm, "end": v(2127.75, -1191.36) * mm});
            skLineSegment(sketch, "E1431", {"start": v(638.54, -107.03) * mm, "end": v(452.62, 54.26) * mm});
            skLineSegment(sketch, "E1432", {"start": v(-2032.77, -2078.07) * mm, "end": v(-2042.93, -2092.04) * mm});
            skLineSegment(sketch, "E1433", {"start": v(-69.1, -1384.14) * mm, "end": v(-215.4, -1482.44) * mm});
            skLineSegment(sketch, "E1434", {"start": v(-215.4, -1482.44) * mm, "end": v(-229.37, -1542.13) * mm});
            skLineSegment(sketch, "E1435", {"start": v(-229.37, -1542.13) * mm, "end": v(-357.64, -1623.41) * mm});
            skLineSegment(sketch, "E1436", {"start": v(-357.64, -1623.41) * mm, "end": v(-418.6, -1792.32) * mm});
            skLineSegment(sketch, "E1437", {"start": v(-418.6, -1792.32) * mm, "end": v(-474.48, -1811.37) * mm});
            skLineSegment(sketch, "E1438", {"start": v(2099.3, -1166.72) * mm, "end": v(2127.75, -1191.36) * mm});
            skLineSegment(sketch, "E1439", {"start": v(-991.88, -1867.5) * mm, "end": v(-883.68, -1798.16) * mm});
            skLineSegment(sketch, "E1440", {"start": v(1806.44, -2083.15) * mm, "end": v(1850.89, -2139.03) * mm});
            skLineSegment(sketch, "E1441", {"start": v(1850.89, -2139.03) * mm, "end": v(1791.2, -2205.07) * mm});
            skLineSegment(sketch, "E1442", {"start": v(1791.2, -2205.07) * mm, "end": v(1742.94, -2234.28) * mm});
            skLineSegment(sketch, "E1443", {"start": v(1742.94, -2234.28) * mm, "end": v(1695.95, -2161.9) * mm});
            skLineSegment(sketch, "E1444", {"start": v(1695.95, -2161.9) * mm, "end": v(1670.55, -2175.86) * mm});
            skLineSegment(sketch, "E1445", {"start": v(1670.55, -2175.86) * mm, "end": v(1657.85, -2156.81) * mm});
            skLineSegment(sketch, "E1446", {"start": v(1657.85, -2156.81) * mm, "end": v(1681.98, -2141.57) * mm});
            skLineSegment(sketch, "E1447", {"start": v(1681.98, -2141.57) * mm, "end": v(1673.09, -2126.33) * mm});
            skLineSegment(sketch, "E1448", {"start": v(1673.09, -2126.33) * mm, "end": v(1647.69, -2142.84) * mm});
            skLineSegment(sketch, "E1449", {"start": v(1647.69, -2142.84) * mm, "end": v(1634.99, -2119.98) * mm});
            skLineSegment(sketch, "E1450", {"start": v(1634.99, -2119.98) * mm, "end": v(1659.12, -2106.01) * mm});
            skLineSegment(sketch, "E1451", {"start": v(2658.6, -1763.11) * mm, "end": v(2413.75, -1548.23) * mm});
            skLineSegment(sketch, "E1452", {"start": v(823.46, -629) * mm, "end": v(805.68, -642.97) * mm});
            skLineSegment(sketch, "E1453", {"start": v(805.68, -642.97) * mm, "end": v(804.4, -687.42) * mm});
            skLineSegment(sketch, "E1454", {"start": v(804.4, -687.42) * mm, "end": v(775.2, -717.9) * mm});
            skLineSegment(sketch, "E1455", {"start": v(775.2, -717.9) * mm, "end": v(810.76, -757.27) * mm});
            skLineSegment(sketch, "E1456", {"start": v(810.76, -757.27) * mm, "end": v(812.03, -801.72) * mm});
            skLineSegment(sketch, "E1457", {"start": v(812.03, -801.72) * mm, "end": v(601.2, -1004.92) * mm});
            skLineSegment(sketch, "E1458", {"start": v(601.2, -1004.92) * mm, "end": v(549.14, -1007.46) * mm});
            skLineSegment(sketch, "E1459", {"start": v(549.14, -1007.46) * mm, "end": v(451.35, -1103.98) * mm});
            skLineSegment(sketch, "E1460", {"start": v(451.35, -1103.98) * mm, "end": v(424.68, -1102.71) * mm});
            skLineSegment(sketch, "E1461", {"start": v(424.68, -1102.71) * mm, "end": v(410.45, -1111.85) * mm});
            skLineSegment(sketch, "E1462", {"start": v(-1051.06, -1096.36) * mm, "end": v(-1012.96, -1159.86) * mm});
            skLineSegment(sketch, "E1463", {"start": v(2076.95, -1152.24) * mm, "end": v(2099.3, -1166.72) * mm});
            skLineSegment(sketch, "E1464", {"start": v(967.98, -2486.76) * mm, "end": v(1041.13, -2597) * mm});
            skLineSegment(sketch, "E1465", {"start": v(1482.84, -1032.6) * mm, "end": v(1509.26, -1060.04) * mm});
            skLineSegment(sketch, "E1466", {"start": v(2826.25, 1566.07) * mm, "end": v(2940.8, 1482.25) * mm});
            skLineSegment(sketch, "E1467", {"start": v(2059.17, -1172.05) * mm, "end": v(2076.95, -1152.24) * mm});
            skLineSegment(sketch, "E1468", {"start": v(2413.75, -1548.23) * mm, "end": v(2409.69, -1544.67) * mm});
            skLineSegment(sketch, "E1469", {"start": v(2409.69, -1544.67) * mm, "end": v(2073.14, -1252.57) * mm});
            skLineSegment(sketch, "E1470", {"start": v(2073.14, -1252.57) * mm, "end": v(2087.1, -1234.8) * mm});
            skLineSegment(sketch, "E1471", {"start": v(2087.1, -1234.8) * mm, "end": v(2040.12, -1192.88) * mm});
            skLineSegment(sketch, "E1472", {"start": v(2040.12, -1192.88) * mm, "end": v(2059.17, -1172.05) * mm});
            skLineSegment(sketch, "E1473", {"start": v(1454.14, 1007.27) * mm, "end": v(1586.98, 839.88) * mm});
            skLineSegment(sketch, "E1474", {"start": v(1783.58, 1291.5) * mm, "end": v(1894.57, 1139.35) * mm});
            skLineSegment(sketch, "E1475", {"start": v(602.48, -152.24) * mm, "end": v(638.54, -107.03) * mm});
            skLineSegment(sketch, "E1476", {"start": v(928.87, -2511.14) * mm, "end": v(918.7, -2520.03) * mm});
            skLineSegment(sketch, "E1477", {"start": v(918.7, -2520.03) * mm, "end": v(912.36, -2547.97) * mm});
            skLineSegment(sketch, "E1478", {"start": v(912.36, -2547.97) * mm, "end": v(958.08, -2619.1) * mm});
            skLineSegment(sketch, "E1479", {"start": v(958.08, -2619.1) * mm, "end": v(988.56, -2631.8) * mm});
            skLineSegment(sketch, "E1480", {"start": v(988.56, -2631.8) * mm, "end": v(1001.26, -2624.17) * mm});
            skLineSegment(sketch, "E1481", {"start": v(-2101.86, -2616.04) * mm, "end": v(-2130.82, -2494.88) * mm});
            skLineSegment(sketch, "E1482", {"start": v(2907.53, 1334.42) * mm, "end": v(3030.72, 1244.25) * mm});
            skLineSegment(sketch, "E1483", {"start": v(1459.47, -1008.48) * mm, "end": v(1488.94, -979.52) * mm});
            skLineSegment(sketch, "E1484", {"start": v(-700.3, -1869.03) * mm, "end": v(-634, -1827.63) * mm});
            skLineSegment(sketch, "E1485", {"start": v(2030.97, -1149.2) * mm, "end": v(2049, -1128.11) * mm});
            skLineSegment(sketch, "E1486", {"start": v(-873.26, -1389.73) * mm, "end": v(-804.68, -1341.47) * mm});
            skLineSegment(sketch, "E1487", {"start": v(-804.68, -1341.47) * mm, "end": v(-672.6, -1250.03) * mm});
            skLineSegment(sketch, "E1488", {"start": v(-672.6, -1250.03) * mm, "end": v(-568.46, -1177.64) * mm});
            skLineSegment(sketch, "E1489", {"start": v(-568.46, -1177.64) * mm, "end": v(-557.03, -1168.75) * mm});
            skLineSegment(sketch, "E1490", {"start": v(1494.02, -1846.93) * mm, "end": v(1514.34, -1872.33) * mm});
            skLineSegment(sketch, "E1491", {"start": v(504.69, -249.27) * mm, "end": v(352.29, -113.38) * mm});
            skLineSegment(sketch, "E1492", {"start": v(352.29, -113.38) * mm, "end": v(287.52, -49.88) * mm});
            skLineSegment(sketch, "E1493", {"start": v(296.4, -1510.38) * mm, "end": v(271, -1471.01) * mm});
            skLineSegment(sketch, "E1494", {"start": v(-1117.61, -1222.6) * mm, "end": v(-1157.74, -1161.13) * mm});
            skLineSegment(sketch, "E1495", {"start": v(-1157.74, -1161.13) * mm, "end": v(-1051.06, -1096.36) * mm});
            skLineSegment(sketch, "E1496", {"start": v(2030.97, -1149.2) * mm, "end": v(2059.17, -1172.05) * mm});
            skLineSegment(sketch, "E1497", {"start": v(-2443.24, -673.7) * mm, "end": v(-2321.06, -616.3) * mm});
            skLineSegment(sketch, "E1498", {"start": v(-1012.96, -1159.86) * mm, "end": v(-873.26, -1389.73) * mm});
            skLineSegment(sketch, "E1499", {"start": v(528.56, -1800.96) * mm, "end": v(495.8, -1752.95) * mm});
            skLineSegment(sketch, "E1500", {"start": v(495.8, -1752.95) * mm, "end": v(455.16, -1780.9) * mm});
            skLineSegment(sketch, "E1501", {"start": v(455.16, -1780.9) * mm, "end": v(443.73, -1816.45) * mm});
            skLineSegment(sketch, "E1502", {"start": v(443.73, -1816.45) * mm, "end": v(452.62, -1827.88) * mm});
            skLineSegment(sketch, "E1503", {"start": v(452.62, -1827.88) * mm, "end": v(478.02, -1834.23) * mm});
            skLineSegment(sketch, "E1504", {"start": v(478.02, -1834.23) * mm, "end": v(489.45, -1825.34) * mm});
            skLineSegment(sketch, "E1505", {"start": v(2885.94, 1772.57) * mm, "end": v(2910.32, 1758.1) * mm});
            skLineSegment(sketch, "E1506", {"start": v(1735.32, 975.52) * mm, "end": v(1894.57, 1139.35) * mm});
            skLineSegment(sketch, "E1507", {"start": v(2081.26, -1189.83) * mm, "end": v(2099.3, -1166.72) * mm});
            skLineSegment(sketch, "E1508", {"start": v(-1485.4, -1410.05) * mm, "end": v(-1475.24, -1420.21) * mm});
            skLineSegment(sketch, "E1509", {"start": v(2059.17, -1172.05) * mm, "end": v(2081.26, -1189.83) * mm});
            skLineSegment(sketch, "E1510", {"start": v(2146.54, -1169.77) * mm, "end": v(2115.55, -1146.14) * mm});
            skLineSegment(sketch, "E1511", {"start": v(-767.85, -1738.98) * mm, "end": v(-762.01, -1761.59) * mm});
            skLineSegment(sketch, "E1512", {"start": v(1082.54, 856.9) * mm, "end": v(1166.36, 764.19) * mm});
            skLineSegment(sketch, "E1513", {"start": v(-1094.24, -1076.04) * mm, "end": v(-938.03, -978.25) * mm});
            skLineSegment(sketch, "E1514", {"start": v(515.86, 184.56) * mm, "end": v(667.25, 341.28) * mm});
            skLineSegment(sketch, "E1515", {"start": v(791.2, -596.74) * mm, "end": v(872.99, -510.9) * mm});
            skLineSegment(sketch, "E1516", {"start": v(872.99, -510.9) * mm, "end": v(876.8, -508.35) * mm});
            skLineSegment(sketch, "E1517", {"start": v(876.8, -508.35) * mm, "end": v(879.34, -504.54) * mm});
            skLineSegment(sketch, "E1518", {"start": v(879.34, -504.54) * mm, "end": v(883.15, -502) * mm});
            skLineSegment(sketch, "E1519", {"start": v(883.15, -502) * mm, "end": v(886.96, -500.73) * mm});
            skLineSegment(sketch, "E1520", {"start": v(886.96, -500.73) * mm, "end": v(890.77, -498.2) * mm});
            skLineSegment(sketch, "E1521", {"start": v(890.77, -498.2) * mm, "end": v(893.3, -495.65) * mm});
            skLineSegment(sketch, "E1522", {"start": v(893.3, -495.65) * mm, "end": v(897.12, -494.38) * mm});
            skLineSegment(sketch, "E1523", {"start": v(897.12, -494.38) * mm, "end": v(900.93, -491.84) * mm});
            skLineSegment(sketch, "E1524", {"start": v(900.93, -491.84) * mm, "end": v(904.74, -490.57) * mm});
            skLineSegment(sketch, "E1525", {"start": v(904.74, -490.57) * mm, "end": v(908.55, -488.03) * mm});
            skLineSegment(sketch, "E1526", {"start": v(908.55, -488.03) * mm, "end": v(916.17, -485.5) * mm});
            skLineSegment(sketch, "E1527", {"start": v(916.17, -485.5) * mm, "end": v(919.98, -485.5) * mm});
            skLineSegment(sketch, "E1528", {"start": v(919.98, -485.5) * mm, "end": v(923.79, -484.22) * mm});
            skLineSegment(sketch, "E1529", {"start": v(923.79, -484.22) * mm, "end": v(928.87, -482.95) * mm});
            skLineSegment(sketch, "E1530", {"start": v(928.87, -482.95) * mm, "end": v(932.68, -482.95) * mm});
            skLineSegment(sketch, "E1531", {"start": v(932.68, -482.95) * mm, "end": v(936.49, -481.68) * mm});
            skLineSegment(sketch, "E1532", {"start": v(936.49, -481.68) * mm, "end": v(945.38, -481.68) * mm});
            skLineSegment(sketch, "E1533", {"start": v(945.38, -481.68) * mm, "end": v(951.73, -482.95) * mm});
            skLineSegment(sketch, "E1534", {"start": v(951.73, -482.95) * mm, "end": v(955.54, -482.95) * mm});
            skLineSegment(sketch, "E1535", {"start": v(955.54, -482.95) * mm, "end": v(959.35, -484.22) * mm});
            skLineSegment(sketch, "E1536", {"start": v(959.35, -484.22) * mm, "end": v(965.7, -485.5) * mm});
            skLineSegment(sketch, "E1537", {"start": v(965.7, -485.5) * mm, "end": v(970.78, -486.76) * mm});
            skLineSegment(sketch, "E1538", {"start": v(970.78, -486.76) * mm, "end": v(974.59, -488.03) * mm});
            skLineSegment(sketch, "E1539", {"start": v(974.59, -488.03) * mm, "end": v(977.13, -489.3) * mm});
            skLineSegment(sketch, "E1540", {"start": v(977.13, -489.3) * mm, "end": v(984.75, -491.84) * mm});
            skLineSegment(sketch, "E1541", {"start": v(984.75, -491.84) * mm, "end": v(1003.8, -499.46) * mm});
            skLineSegment(sketch, "E1542", {"start": v(1003.8, -499.46) * mm, "end": v(1008.88, -503.27) * mm});
            skLineSegment(sketch, "E1543", {"start": v(1008.88, -503.27) * mm, "end": v(1013.96, -505.81) * mm});
            skLineSegment(sketch, "E1544", {"start": v(1013.96, -505.81) * mm, "end": v(1019.04, -509.62) * mm});
            skLineSegment(sketch, "E1545", {"start": v(1019.04, -509.62) * mm, "end": v(1022.85, -512.16) * mm});
            skLineSegment(sketch, "E1546", {"start": v(1022.85, -512.16) * mm, "end": v(1026.66, -515.97) * mm});
            skLineSegment(sketch, "E1547", {"start": v(1026.66, -515.97) * mm, "end": v(1031.74, -518.51) * mm});
            skLineSegment(sketch, "E1548", {"start": v(1031.74, -518.51) * mm, "end": v(1053.83, -540.6) * mm});
            skLineSegment(sketch, "E1549", {"start": v(1732.78, -867.76) * mm, "end": v(1630.92, -759.81) * mm});
            skLineSegment(sketch, "E1550", {"start": v(-1606.05, -1835.5) * mm, "end": v(-1630.18, -1782.16) * mm});
            skLineSegment(sketch, "E1551", {"start": v(-2099.58, -2625.44) * mm, "end": v(-2101.86, -2616.04) * mm});
            skLineSegment(sketch, "E1552", {"start": v(-2260.1, -1542.13) * mm, "end": v(-2311.67, -1427.07) * mm});
            skLineSegment(sketch, "E1553", {"start": v(146.55, -152.75) * mm, "end": v(177.03, -118.46) * mm});
            skLineSegment(sketch, "E1554", {"start": v(177.03, -118.46) * mm, "end": v(203.7, -145.13) * mm});
            skLineSegment(sketch, "E1555", {"start": v(203.7, -145.13) * mm, "end": v(287.52, -49.88) * mm});
            skLineSegment(sketch, "E1556", {"start": v(301.74, -1450.94) * mm, "end": v(348.48, -1420.21) * mm});
            skLineSegment(sketch, "E1557", {"start": v(348.48, -1420.21) * mm, "end": v(375.15, -1458.31) * mm});
            skLineSegment(sketch, "E1558", {"start": v(375.15, -1458.31) * mm, "end": v(331.46, -1487.27) * mm});
            skLineSegment(sketch, "E1559", {"start": v(-2149.61, -2631.8) * mm, "end": v(-2099.58, -2625.44) * mm});
            skLineSegment(sketch, "E1560", {"start": v(-2260.1, -1542.13) * mm, "end": v(-2244.86, -1542.13) * mm});
            skLineSegment(sketch, "E1561", {"start": v(-2244.86, -1542.13) * mm, "end": v(-2239.78, -1543.4) * mm});
            skLineSegment(sketch, "E1562", {"start": v(-2239.78, -1543.4) * mm, "end": v(-2233.43, -1545.94) * mm});
            skLineSegment(sketch, "E1563", {"start": v(-2233.43, -1545.94) * mm, "end": v(-2228.35, -1548.48) * mm});
            skLineSegment(sketch, "E1564", {"start": v(-2228.35, -1548.48) * mm, "end": v(-2219.46, -1553.56) * mm});
            skLineSegment(sketch, "E1565", {"start": v(-2219.46, -1553.56) * mm, "end": v(-2215.65, -1557.37) * mm});
            skLineSegment(sketch, "E1566", {"start": v(-2215.65, -1557.37) * mm, "end": v(-2213.11, -1561.18) * mm});
            skLineSegment(sketch, "E1567", {"start": v(-2213.11, -1561.18) * mm, "end": v(-2211.84, -1565) * mm});
            skLineSegment(sketch, "E1568", {"start": v(-2211.84, -1565) * mm, "end": v(-2210.57, -1570.07) * mm});
            skLineSegment(sketch, "E1569", {"start": v(-2210.57, -1570.07) * mm, "end": v(-2025.15, -1971.4) * mm});
            skLineSegment(sketch, "E1570", {"start": v(-2025.15, -1971.4) * mm, "end": v(-2016.26, -2004.41) * mm});
            skLineSegment(sketch, "E1571", {"start": v(-2016.26, -2004.41) * mm, "end": v(-2015, -2012.03) * mm});
            skLineSegment(sketch, "E1572", {"start": v(-2015, -2012.03) * mm, "end": v(-2015, -2032.35) * mm});
            skLineSegment(sketch, "E1573", {"start": v(-2015, -2032.35) * mm, "end": v(-2018.8, -2046.32) * mm});
            skLineSegment(sketch, "E1574", {"start": v(-2018.8, -2046.32) * mm, "end": v(-2026.42, -2065.37) * mm});
            skLineSegment(sketch, "E1575", {"start": v(-2026.42, -2065.37) * mm, "end": v(-2032.77, -2078.07) * mm});
            skLineSegment(sketch, "E1576", {"start": v(1577.84, -1971.4) * mm, "end": v(1593.08, -1999.33) * mm});
            skLineSegment(sketch, "E1577", {"start": v(528.56, -1800.96) * mm, "end": v(573.27, -1773.27) * mm});
            skLineSegment(sketch, "E1578", {"start": v(573.27, -1773.27) * mm, "end": v(597.4, -1813.91) * mm});
            skLineSegment(sketch, "E1579", {"start": v(597.4, -1813.91) * mm, "end": v(554.98, -1840.07) * mm});
            skLineSegment(sketch, "E1580", {"start": v(2885.94, 1772.57) * mm, "end": v(2897.37, 1785.27) * mm});
            skLineSegment(sketch, "E1581", {"start": v(2897.37, 1785.27) * mm, "end": v(2918.96, 1770.03) * mm});
            skLineSegment(sketch, "E1582", {"start": v(2918.96, 1770.03) * mm, "end": v(2910.32, 1758.1) * mm});
            skLineSegment(sketch, "E1583", {"start": v(2907.53, 1334.42) * mm, "end": v(2925.3, 1348.39) * mm});
            skLineSegment(sketch, "E1584", {"start": v(2925.3, 1348.39) * mm, "end": v(3035.8, 1268.38) * mm});
            skLineSegment(sketch, "E1585", {"start": v(3035.8, 1268.38) * mm, "end": v(3030.72, 1244.25) * mm});
            skLineSegment(sketch, "E1586", {"start": v(1322.57, 594) * mm, "end": v(1417.82, 685.45) * mm});
            skLineSegment(sketch, "E1587", {"start": v(1417.82, 685.45) * mm, "end": v(1454.9, 719.49) * mm});
            skLineSegment(sketch, "E1588", {"start": v(2833.87, -1911.7) * mm, "end": v(2929.12, -1793.6) * mm});
            skLineSegment(sketch, "E1589", {"start": v(1514.34, -1872.33) * mm, "end": v(1488.94, -1888.84) * mm});
            skLineSegment(sketch, "E1590", {"start": v(1488.94, -1888.84) * mm, "end": v(1471.16, -1860.9) * mm});
            skLineSegment(sketch, "E1591", {"start": v(1471.16, -1860.9) * mm, "end": v(1494.02, -1846.93) * mm});
            skLineSegment(sketch, "E1592", {"start": v(-1239.02, -1290.67) * mm, "end": v(-1136.15, -1232.25) * mm});
            skLineSegment(sketch, "E1593", {"start": v(-1136.15, -1232.25) * mm, "end": v(-1117.61, -1222.6) * mm});
            skLineSegment(sketch, "E1594", {"start": v(1706.87, 1486.06) * mm, "end": v(1731.5, 1447.45) * mm});
            skLineSegment(sketch, "E1595", {"start": v(1731.5, 1447.45) * mm, "end": v(1881.37, 1541.43) * mm});
            skLineSegment(sketch, "E1596", {"start": v(-64.27, -1284.57) * mm, "end": v(-36.33, -1330.04) * mm});
            skLineSegment(sketch, "E1597", {"start": v(-36.33, -1330.04) * mm, "end": v(337.05, -1092.55) * mm});
            skLineSegment(sketch, "E1598", {"start": v(337.05, -1092.55) * mm, "end": v(307.84, -1049.37) * mm});
            skLineSegment(sketch, "E1599", {"start": v(2910.32, 1758.1) * mm, "end": v(2813.8, 1624.49) * mm});
            skLineSegment(sketch, "E1600", {"start": v(1983.47, 1123.1) * mm, "end": v(2037.58, 1170.59) * mm});
            skLineSegment(sketch, "E1601", {"start": v(2037.58, 1170.59) * mm, "end": v(2266.68, 1356) * mm});
            skLineSegment(sketch, "E1602", {"start": v(2266.68, 1356) * mm, "end": v(2431.28, 1489.36) * mm});
            skLineSegment(sketch, "E1603", {"start": v(2431.28, 1489.36) * mm, "end": v(2443.98, 1502.06) * mm});
            skLineSegment(sketch, "E1604", {"start": v(2443.98, 1502.06) * mm, "end": v(2452.87, 1509.68) * mm});
            skLineSegment(sketch, "E1605", {"start": v(2452.87, 1509.68) * mm, "end": v(2459.22, 1519.84) * mm});
            skLineSegment(sketch, "E1606", {"start": v(265.42, -2033.62) * mm, "end": v(408.17, -1944.72) * mm});
            skLineSegment(sketch, "E1607", {"start": v(408.17, -1944.72) * mm, "end": v(415.79, -1942.18) * mm});
            skLineSegment(sketch, "E1608", {"start": v(415.79, -1942.18) * mm, "end": v(420.87, -1940.91) * mm});
            skLineSegment(sketch, "E1609", {"start": v(420.87, -1940.91) * mm, "end": v(423.4, -1939.64) * mm});
            skLineSegment(sketch, "E1610", {"start": v(423.4, -1939.64) * mm, "end": v(428.49, -1939.64) * mm});
            skLineSegment(sketch, "E1611", {"start": v(428.49, -1939.64) * mm, "end": v(431.03, -1938.37) * mm});
            skLineSegment(sketch, "E1612", {"start": v(431.03, -1938.37) * mm, "end": v(436.1, -1939.64) * mm});
            skLineSegment(sketch, "E1613", {"start": v(436.1, -1939.64) * mm, "end": v(441.19, -1942.18) * mm});
            skLineSegment(sketch, "E1614", {"start": v(441.19, -1942.18) * mm, "end": v(447.54, -1948.53) * mm});
            skLineSegment(sketch, "E1615", {"start": v(447.54, -1948.53) * mm, "end": v(448.8, -1951.07) * mm});
            skLineSegment(sketch, "E1616", {"start": v(448.8, -1951.07) * mm, "end": v(450.08, -1956.15) * mm});
            skLineSegment(sketch, "E1617", {"start": v(1760.72, 2233.58) * mm, "end": v(1892.8, 2016.4) * mm});
            skLineSegment(sketch, "E1618", {"start": v(-576.08, -1847.44) * mm, "end": v(-557.03, -1916.78) * mm});
            skLineSegment(sketch, "E1619", {"start": v(-1239.02, -1290.67) * mm, "end": v(-1081.54, -1530.2) * mm});
            skLineSegment(sketch, "E1620", {"start": v(1171.44, -2614.01) * mm, "end": v(1096.5, -2499.71) * mm});
            skLineSegment(sketch, "E1621", {"start": v(1096.5, -2499.71) * mm, "end": v(1115.56, -2488.28) * mm});
            skLineSegment(sketch, "E1622", {"start": v(1115.56, -2488.28) * mm, "end": v(1187.95, -2601.31) * mm});
            skLineSegment(sketch, "E1623", {"start": v(1187.95, -2601.31) * mm, "end": v(1171.44, -2614.01) * mm});
            skLineSegment(sketch, "E1624", {"start": v(-84.6, -1298.3) * mm, "end": v(-68.85, -1287.62) * mm});
            skLineSegment(sketch, "E1625", {"start": v(-68.85, -1287.62) * mm, "end": v(-64.27, -1284.57) * mm});
            skLineSegment(sketch, "E1626", {"start": v(1165.09, 442.88) * mm, "end": v(1166.36, 444.15) * mm});
            skLineSegment(sketch, "E1627", {"start": v(2718.8, 795.94) * mm, "end": v(2676.64, 845.98) * mm});
            skLineSegment(sketch, "E1628", {"start": v(2676.64, 845.98) * mm, "end": v(2672.58, 850.55) * mm});
            skLineSegment(sketch, "E1629", {"start": v(2672.58, 850.55) * mm, "end": v(2657.34, 865.79) * mm});
            skLineSegment(sketch, "E1630", {"start": v(2657.34, 865.79) * mm, "end": v(2650.99, 873.4) * mm});
            skLineSegment(sketch, "E1631", {"start": v(2650.99, 873.4) * mm, "end": v(2635.75, 888.65) * mm});
            skLineSegment(sketch, "E1632", {"start": v(2635.75, 888.65) * mm, "end": v(2628.13, 895) * mm});
            skLineSegment(sketch, "E1633", {"start": v(2628.13, 895) * mm, "end": v(2619.24, 900.08) * mm});
            skLineSegment(sketch, "E1634", {"start": v(2619.24, 900.08) * mm, "end": v(2601.46, 912.78) * mm});
            skLineSegment(sketch, "E1635", {"start": v(2601.46, 912.78) * mm, "end": v(2593.84, 919.13) * mm});
            skLineSegment(sketch, "E1636", {"start": v(2593.84, 919.13) * mm, "end": v(2584.95, 924.2) * mm});
            skLineSegment(sketch, "E1637", {"start": v(2584.95, 924.2) * mm, "end": v(2577.33, 929.29) * mm});
            skLineSegment(sketch, "E1638", {"start": v(2577.33, 929.29) * mm, "end": v(2568.44, 934.37) * mm});
            skLineSegment(sketch, "E1639", {"start": v(2568.44, 934.37) * mm, "end": v(2558.28, 939.45) * mm});
            skLineSegment(sketch, "E1640", {"start": v(2558.28, 939.45) * mm, "end": v(2548.12, 943.26) * mm});
            skLineSegment(sketch, "E1641", {"start": v(2548.12, 943.26) * mm, "end": v(2540.5, 947.07) * mm});
            skLineSegment(sketch, "E1642", {"start": v(2540.5, 947.07) * mm, "end": v(2530.34, 949.6) * mm});
            skLineSegment(sketch, "E1643", {"start": v(2530.34, 949.6) * mm, "end": v(2510.02, 957.23) * mm});
            skLineSegment(sketch, "E1644", {"start": v(2510.02, 957.23) * mm, "end": v(2499.86, 959.77) * mm});
            skLineSegment(sketch, "E1645", {"start": v(2499.86, 959.77) * mm, "end": v(2490.97, 962.3) * mm});
            skLineSegment(sketch, "E1646", {"start": v(2490.97, 962.3) * mm, "end": v(2470.65, 967.39) * mm});
            skLineSegment(sketch, "E1647", {"start": v(2470.65, 967.39) * mm, "end": v(2468.1, 968.66) * mm});
            skLineSegment(sketch, "E1648", {"start": v(2468.1, 968.66) * mm, "end": v(2456.68, 969.93) * mm});
            skLineSegment(sketch, "E1649", {"start": v(2456.68, 969.93) * mm, "end": v(2445.25, 972.47) * mm});
            skLineSegment(sketch, "E1650", {"start": v(2445.25, 972.47) * mm, "end": v(2435.09, 973.74) * mm});
            skLineSegment(sketch, "E1651", {"start": v(2435.09, 973.74) * mm, "end": v(2423.66, 975) * mm});
            skLineSegment(sketch, "E1652", {"start": v(2423.66, 975) * mm, "end": v(2410.96, 976.28) * mm});
            skLineSegment(sketch, "E1653", {"start": v(2410.96, 976.28) * mm, "end": v(2365.24, 976.28) * mm});
            skLineSegment(sketch, "E1654", {"start": v(2365.24, 976.28) * mm, "end": v(2342.38, 973.74) * mm});
            skLineSegment(sketch, "E1655", {"start": v(2342.38, 973.74) * mm, "end": v(2332.22, 972.47) * mm});
            skLineSegment(sketch, "E1656", {"start": v(2332.22, 972.47) * mm, "end": v(2297.93, 964.85) * mm});
            skLineSegment(sketch, "E1657", {"start": v(2297.93, 964.85) * mm, "end": v(2287.77, 962.3) * mm});
            skLineSegment(sketch, "E1658", {"start": v(2287.77, 962.3) * mm, "end": v(2277.6, 958.5) * mm});
            skLineSegment(sketch, "E1659", {"start": v(2277.6, 958.5) * mm, "end": v(2267.45, 955.96) * mm});
            skLineSegment(sketch, "E1660", {"start": v(2267.45, 955.96) * mm, "end": v(2257.29, 952.15) * mm});
            skLineSegment(sketch, "E1661", {"start": v(2257.29, 952.15) * mm, "end": v(2245.86, 948.34) * mm});
            skLineSegment(sketch, "E1662", {"start": v(2245.86, 948.34) * mm, "end": v(2235.7, 944.53) * mm});
            skLineSegment(sketch, "E1663", {"start": v(2235.7, 944.53) * mm, "end": v(2226.8, 939.45) * mm});
            skLineSegment(sketch, "E1664", {"start": v(2226.8, 939.45) * mm, "end": v(2216.65, 934.37) * mm});
            skLineSegment(sketch, "E1665", {"start": v(2216.65, 934.37) * mm, "end": v(2207.76, 929.29) * mm});
            skLineSegment(sketch, "E1666", {"start": v(2207.76, 929.29) * mm, "end": v(2202.68, 926.75) * mm});
            skLineSegment(sketch, "E1667", {"start": v(2202.68, 926.75) * mm, "end": v(2182.36, 914.05) * mm});
            skLineSegment(sketch, "E1668", {"start": v(2182.36, 914.05) * mm, "end": v(2174.74, 907.7) * mm});
            skLineSegment(sketch, "E1669", {"start": v(2174.74, 907.7) * mm, "end": v(2164.58, 901.35) * mm});
            skLineSegment(sketch, "E1670", {"start": v(2164.58, 901.35) * mm, "end": v(2155.69, 896.27) * mm});
            skLineSegment(sketch, "E1671", {"start": v(2611.62, -1540.86) * mm, "end": v(2793.23, -1688.18) * mm});
            skLineSegment(sketch, "E1672", {"start": v(396.74, -1665.32) * mm, "end": v(371.34, -1625.95) * mm});
            skLineSegment(sketch, "E1673", {"start": v(269.74, -1952.34) * mm, "end": v(284.98, -1953.61) * mm});
            skLineSegment(sketch, "E1674", {"start": v(284.98, -1953.61) * mm, "end": v(387.85, -1887.57) * mm});
            skLineSegment(sketch, "E1675", {"start": v(387.85, -1887.57) * mm, "end": v(394.2, -1867.25) * mm});
            skLineSegment(sketch, "E1676", {"start": v(1488.94, -979.52) * mm, "end": v(1402.58, -890.62) * mm});
            skLineSegment(sketch, "E1677", {"start": v(1402.58, -890.62) * mm, "end": v(1349.24, -942.7) * mm});
            skLineSegment(sketch, "E1678", {"start": v(1349.24, -942.7) * mm, "end": v(1290.82, -881.73) * mm});
            skLineSegment(sketch, "E1679", {"start": v(1700.52, 943.51) * mm, "end": v(1735.32, 975.52) * mm});
            skLineSegment(sketch, "E1680", {"start": v(1706.87, 1486.06) * mm, "end": v(1669.28, 1462.69) * mm});
            skLineSegment(sketch, "E1681", {"start": v(1669.28, 1462.69) * mm, "end": v(1699.5, 1416.72) * mm});
            skLineSegment(sketch, "E1682", {"start": v(1098.28, 375.06) * mm, "end": v(1165.09, 442.88) * mm});
            skLineSegment(sketch, "E1683", {"start": v(-1950.22, -1732.63) * mm, "end": v(-1876.56, -1890.11) * mm});
            skLineSegment(sketch, "E1684", {"start": v(-1876.56, -1890.11) * mm, "end": v(-1630.18, -1782.16) * mm});
            skLineSegment(sketch, "E1685", {"start": v(429.76, -1643.48) * mm, "end": v(396.74, -1665.32) * mm});
            skLineSegment(sketch, "E1686", {"start": v(1068.57, -2451.45) * mm, "end": v(987.29, -2327) * mm});
            skLineSegment(sketch, "E1687", {"start": v(987.29, -2327) * mm, "end": v(1006.34, -2314.3) * mm});
            skLineSegment(sketch, "E1688", {"start": v(1006.34, -2314.3) * mm, "end": v(1086.35, -2440.02) * mm});
            skLineSegment(sketch, "E1689", {"start": v(1086.35, -2440.02) * mm, "end": v(1068.57, -2451.45) * mm});
            skLineSegment(sketch, "E1690", {"start": v(-723.4, -1977.23) * mm, "end": v(-771.66, -2008.22) * mm});
            skLineSegment(sketch, "E1691", {"start": v(-771.66, -2008.22) * mm, "end": v(-888.5, -1830.42) * mm});
            skLineSegment(sketch, "E1692", {"start": v(-888.5, -1830.42) * mm, "end": v(-883.68, -1798.16) * mm});
            skLineSegment(sketch, "E1693", {"start": v(1990.59, 2165) * mm, "end": v(2008.37, 2107.85) * mm});
            skLineSegment(sketch, "E1694", {"start": v(1815.33, 2046.89) * mm, "end": v(1836.92, 2063.4) * mm});
            skLineSegment(sketch, "E1695", {"start": v(1836.92, 2063.4) * mm, "end": v(1742.94, 2220.88) * mm});
            skLineSegment(sketch, "E1696", {"start": v(1742.94, 2220.88) * mm, "end": v(1760.72, 2233.58) * mm});
            skLineSegment(sketch, "E1697", {"start": v(-1100.6, 2473.6) * mm, "end": v(-996.45, 2308.5) * mm});
            skLineSegment(sketch, "E1698", {"start": v(-996.45, 2308.5) * mm, "end": v(-1070.11, 2260.25) * mm});
            skLineSegment(sketch, "E1699", {"start": v(-1070.11, 2260.25) * mm, "end": v(-1080.27, 2270.4) * mm});
            skLineSegment(sketch, "E1700", {"start": v(-1080.27, 2270.4) * mm, "end": v(-1129.8, 2237.39) * mm});
            skLineSegment(sketch, "E1701", {"start": v(-1129.8, 2237.39) * mm, "end": v(-1235.72, 2391.82) * mm});
            skLineSegment(sketch, "E1702", {"start": v(2415.02, 2491.64) * mm, "end": v(2416.04, 2484.02) * mm});
            skLineSegment(sketch, "E1703", {"start": v(2416.04, 2484.02) * mm, "end": v(2417.56, 2472.09) * mm});
            skLineSegment(sketch, "E1704", {"start": v(2417.56, 2472.09) * mm, "end": v(2419.08, 2460.4) * mm});
            skLineSegment(sketch, "E1705", {"start": v(2419.08, 2460.4) * mm, "end": v(2420.6, 2448.72) * mm});
            skLineSegment(sketch, "E1706", {"start": v(2420.6, 2448.72) * mm, "end": v(2422.13, 2436.78) * mm});
            skLineSegment(sketch, "E1707", {"start": v(2422.13, 2436.78) * mm, "end": v(2427.72, 2398.43) * mm});
            skLineSegment(sketch, "E1708", {"start": v(2427.72, 2398.43) * mm, "end": v(2434.07, 2364.39) * mm});
            skLineSegment(sketch, "E1709", {"start": v(2434.07, 2364.39) * mm, "end": v(2441.94, 2330.86) * mm});
            skLineSegment(sketch, "E1710", {"start": v(2441.94, 2330.86) * mm, "end": v(2451.09, 2297.33) * mm});
            skLineSegment(sketch, "E1711", {"start": v(2451.09, 2297.33) * mm, "end": v(2461.5, 2264.31) * mm});
            skLineSegment(sketch, "E1712", {"start": v(2461.5, 2264.31) * mm, "end": v(2558.28, 1928.78) * mm});
            skLineSegment(sketch, "E1713", {"start": v(2558.28, 1928.78) * mm, "end": v(2671.05, 1587.15) * mm});
            skLineSegment(sketch, "E1714", {"start": v(-1714, 2217.07) * mm, "end": v(-1444.76, 2398.68) * mm});
            skLineSegment(sketch, "E1715", {"start": v(-1444.76, 2398.68) * mm, "end": v(-1429.52, 2396.14) * mm});
            skLineSegment(sketch, "E1716", {"start": v(-1429.52, 2396.14) * mm, "end": v(-1420.63, 2383.44) * mm});
            skLineSegment(sketch, "E1717", {"start": v(-1420.63, 2383.44) * mm, "end": v(-1377.96, 2410.87) * mm});
            skLineSegment(sketch, "E1718", {"start": v(-1377.96, 2410.87) * mm, "end": v(-1363.48, 2420.27) * mm});
            skLineSegment(sketch, "E1719", {"start": v(-1363.48, 2420.27) * mm, "end": v(-1339.1, 2414.94) * mm});
            skLineSegment(sketch, "E1720", {"start": v(-1854.97, 2432.97) * mm, "end": v(-1896.88, 2493.93) * mm});
            skLineSegment(sketch, "E1721", {"start": v(-1339.1, 2414.94) * mm, "end": v(-1316.5, 2409.86) * mm});
            skLineSegment(sketch, "E1722", {"start": v(-1896.88, 2493.93) * mm, "end": v(-1757.18, 2591.72) * mm});
            skLineSegment(sketch, "E1723", {"start": v(-1757.18, 2591.72) * mm, "end": v(-1795.28, 2660.3) * mm});
            skLineSegment(sketch, "E1724", {"start": v(-1795.28, 2660.3) * mm, "end": v(-1848.62, 2623.47) * mm});
            skLineSegment(sketch, "E1725", {"start": v(-1848.62, 2623.47) * mm, "end": v(-1866.4, 2562.5) * mm});
            skLineSegment(sketch, "E1726", {"start": v(-1866.4, 2562.5) * mm, "end": v(-1918.47, 2528.22) * mm});
            skLineSegment(sketch, "E1727", {"start": v(-1235.72, 2391.82) * mm, "end": v(-1199.9, 2575.2) * mm});
            skLineSegment(sketch, "E1728", {"start": v(-1377.96, 2410.87) * mm, "end": v(-1383.8, 2424.08) * mm});
            skLineSegment(sketch, "E1729", {"start": v(-1383.8, 2424.08) * mm, "end": v(-1352.05, 2576.48) * mm});
            skLineSegment(sketch, "E1730", {"start": v(-1352.05, 2576.48) * mm, "end": v(-1349.51, 2581.56) * mm});
            skLineSegment(sketch, "E1731", {"start": v(-1349.51, 2581.56) * mm, "end": v(-1348.24, 2586.64) * mm});
            skLineSegment(sketch, "E1732", {"start": v(-1348.24, 2586.64) * mm, "end": v(-1345.7, 2591.72) * mm});
            skLineSegment(sketch, "E1733", {"start": v(-1345.7, 2591.72) * mm, "end": v(-1343.16, 2595.53) * mm});
            skLineSegment(sketch, "E1734", {"start": v(-1343.16, 2595.53) * mm, "end": v(-1340.62, 2601.88) * mm});
            skLineSegment(sketch, "E1735", {"start": v(-1340.62, 2601.88) * mm, "end": v(-1338.08, 2605.69) * mm});
            skLineSegment(sketch, "E1736", {"start": v(-1338.08, 2605.69) * mm, "end": v(-1335.54, 2612.04) * mm});
            skLineSegment(sketch, "E1737", {"start": v(-1335.54, 2612.04) * mm, "end": v(-1333, 2615.85) * mm});
            skLineSegment(sketch, "E1738", {"start": v(-1333, 2615.85) * mm, "end": v(-1329.2, 2619.66) * mm});
            skLineSegment(sketch, "E1739", {"start": v(-1329.2, 2619.66) * mm, "end": v(-1326.65, 2623.47) * mm});
            skLineSegment(sketch, "E1740", {"start": v(-1326.65, 2623.47) * mm, "end": v(-1322.84, 2627.28) * mm});
            skLineSegment(sketch, "E1741", {"start": v(-1322.84, 2627.28) * mm, "end": v(-1319.03, 2632.36) * mm});
            skLineSegment(sketch, "E1742", {"start": v(-1319.03, 2632.36) * mm, "end": v(-1315.22, 2636.17) * mm});
            skLineSegment(sketch, "E1743", {"start": v(-1315.22, 2636.17) * mm, "end": v(-1312.68, 2639.98) * mm});
            skLineSegment(sketch, "E1744", {"start": v(-1312.68, 2639.98) * mm, "end": v(-1307.6, 2643.79) * mm});
            skLineSegment(sketch, "E1745", {"start": v(-1307.6, 2643.79) * mm, "end": v(-1303.8, 2646.33) * mm});
            skLineSegment(sketch, "E1746", {"start": v(-1303.8, 2646.33) * mm, "end": v(-1296.17, 2653.95) * mm});
            skLineSegment(sketch, "E1747", {"start": v(-1296.17, 2653.95) * mm, "end": v(-1291.1, 2656.49) * mm});
            skLineSegment(sketch, "E1748", {"start": v(-1291.1, 2656.49) * mm, "end": v(-1287.28, 2660.3) * mm});
            skLineSegment(sketch, "E1749", {"start": v(-1287.28, 2660.3) * mm, "end": v(-1282.2, 2662.84) * mm});
            skLineSegment(sketch, "E1750", {"start": v(-1282.2, 2662.84) * mm, "end": v(-1277.12, 2664.1) * mm});
            skLineSegment(sketch, "E1751", {"start": v(-1277.12, 2664.1) * mm, "end": v(-1272.04, 2667.92) * mm});
            skLineSegment(sketch, "E1752", {"start": v(-1272.04, 2667.92) * mm, "end": v(-1261.88, 2673) * mm});
            skLineSegment(sketch, "E1753", {"start": v(-1261.88, 2673) * mm, "end": v(-1256.8, 2674.27) * mm});
            skLineSegment(sketch, "E1754", {"start": v(-1256.8, 2674.27) * mm, "end": v(-1251.72, 2676.8) * mm});
            skLineSegment(sketch, "E1755", {"start": v(-1251.72, 2676.8) * mm, "end": v(-1246.64, 2676.8) * mm});
            skLineSegment(sketch, "E1756", {"start": v(-1246.64, 2676.8) * mm, "end": v(-1242.83, 2678.08) * mm});
            skLineSegment(sketch, "E1757", {"start": v(-1242.83, 2678.08) * mm, "end": v(-1237.75, 2680.62) * mm});
            skLineSegment(sketch, "E1758", {"start": v(-1237.75, 2680.62) * mm, "end": v(-1231.4, 2680.62) * mm});
            skLineSegment(sketch, "E1759", {"start": v(-1231.4, 2680.62) * mm, "end": v(-1226.32, 2683.16) * mm});
            skLineSegment(sketch, "E1760", {"start": v(-1226.32, 2683.16) * mm, "end": v(-1178.83, 2683.16) * mm});
            skLineSegment(sketch, "E1761", {"start": v(-1984.51, 2355.5) * mm, "end": v(-1994.67, 2351.69) * mm});
            skLineSegment(sketch, "E1762", {"start": v(-1994.67, 2351.69) * mm, "end": v(-1999.75, 2349.15) * mm});
            skLineSegment(sketch, "E1763", {"start": v(-1999.75, 2349.15) * mm, "end": v(-2004.83, 2347.88) * mm});
            skLineSegment(sketch, "E1764", {"start": v(-2004.83, 2347.88) * mm, "end": v(-2015, 2342.8) * mm});
            skLineSegment(sketch, "E1765", {"start": v(-2015, 2342.8) * mm, "end": v(-2020.07, 2342.8) * mm});
            skLineSegment(sketch, "E1766", {"start": v(-2020.07, 2342.8) * mm, "end": v(-2026.42, 2341.53) * mm});
            skLineSegment(sketch, "E1767", {"start": v(-2026.42, 2341.53) * mm, "end": v(-2031.5, 2341.53) * mm});
            skLineSegment(sketch, "E1768", {"start": v(-2031.5, 2341.53) * mm, "end": v(-2037.85, 2338.99) * mm});
            skLineSegment(sketch, "E1769", {"start": v(-2037.85, 2338.99) * mm, "end": v(-2065.8, 2338.99) * mm});
            skLineSegment(sketch, "E1770", {"start": v(-2065.8, 2338.99) * mm, "end": v(-2070.87, 2341.53) * mm});
            skLineSegment(sketch, "E1771", {"start": v(-2070.87, 2341.53) * mm, "end": v(-2077.22, 2341.53) * mm});
            skLineSegment(sketch, "E1772", {"start": v(-2077.22, 2341.53) * mm, "end": v(-2082.3, 2342.8) * mm});
            skLineSegment(sketch, "E1773", {"start": v(-2082.3, 2342.8) * mm, "end": v(-2087.38, 2342.8) * mm});
            skLineSegment(sketch, "E1774", {"start": v(-2087.38, 2342.8) * mm, "end": v(-2093.73, 2345.34) * mm});
            skLineSegment(sketch, "E1775", {"start": v(-2093.73, 2345.34) * mm, "end": v(-2098.81, 2347.88) * mm});
            skLineSegment(sketch, "E1776", {"start": v(-2098.81, 2347.88) * mm, "end": v(-2103.9, 2349.15) * mm});
            skLineSegment(sketch, "E1777", {"start": v(-2103.9, 2349.15) * mm, "end": v(-2108.97, 2351.69) * mm});
            skLineSegment(sketch, "E1778", {"start": v(-2108.97, 2351.69) * mm, "end": v(-2114.05, 2352.96) * mm});
            skLineSegment(sketch, "E1779", {"start": v(-2114.05, 2352.96) * mm, "end": v(-2119.13, 2352.96) * mm});
            skLineSegment(sketch, "E1780", {"start": v(1892.8, 2016.4) * mm, "end": v(1843.27, 1999.9) * mm});
            skLineSegment(sketch, "E1781", {"start": v(1843.27, 1999.9) * mm, "end": v(1815.33, 2046.89) * mm});
            skLineSegment(sketch, "E1782", {"start": v(-1187.2, 2639.98) * mm, "end": v(-1178.83, 2683.16) * mm});
            skLineSegment(sketch, "E1783", {"start": v(-1918.47, 2528.22) * mm, "end": v(-1896.88, 2493.93) * mm});
            skLineSegment(sketch, "E1784", {"start": v(-1199.9, 2575.2) * mm, "end": v(-1191.02, 2619.66) * mm});
            skLineSegment(sketch, "E1785", {"start": v(-696.73, -1959.96) * mm, "end": v(-662.44, -1934.81) * mm});
            skLineSegment(sketch, "E1786", {"start": v(-711.97, -1848.2) * mm, "end": v(-648.47, -1807.56) * mm});
            skLineSegment(sketch, "E1787", {"start": v(-1781.57, -2286.1) * mm, "end": v(-1783.85, -2291.68) * mm});
            skLineSegment(sketch, "E1788", {"start": v(-1783.85, -2291.68) * mm, "end": v(-1785.89, -2297.27) * mm});
            skLineSegment(sketch, "E1789", {"start": v(-1785.89, -2297.27) * mm, "end": v(-1787.92, -2302.86) * mm});
            skLineSegment(sketch, "E1790", {"start": v(-1787.92, -2302.86) * mm, "end": v(-1789.44, -2308.7) * mm});
            skLineSegment(sketch, "E1791", {"start": v(-1789.44, -2308.7) * mm, "end": v(-1790.97, -2314.3) * mm});
            skLineSegment(sketch, "E1792", {"start": v(-1790.97, -2314.3) * mm, "end": v(-1791.98, -2320.13) * mm});
            skLineSegment(sketch, "E1793", {"start": v(-1791.98, -2320.13) * mm, "end": v(-1793, -2326.23) * mm});
            skLineSegment(sketch, "E1794", {"start": v(-1793, -2326.23) * mm, "end": v(-1793.76, -2332.07) * mm});
            skLineSegment(sketch, "E1795", {"start": v(-1793.76, -2332.07) * mm, "end": v(-1794.27, -2337.91) * mm});
            skLineSegment(sketch, "E1796", {"start": v(-1794.27, -2337.91) * mm, "end": v(-1794.27, -2344) * mm});
            skLineSegment(sketch, "E1797", {"start": v(-1794.27, -2344) * mm, "end": v(-1794.27, -2350.1) * mm});
            skLineSegment(sketch, "E1798", {"start": v(-1794.27, -2350.1) * mm, "end": v(-1794.01, -2355.95) * mm});
            skLineSegment(sketch, "E1799", {"start": v(-1794.01, -2355.95) * mm, "end": v(-1793.5, -2361.79) * mm});
            skLineSegment(sketch, "E1800", {"start": v(-1793.5, -2361.79) * mm, "end": v(-1792.74, -2367.88) * mm});
            skLineSegment(sketch, "E1801", {"start": v(-1792.74, -2367.88) * mm, "end": v(-1791.73, -2373.73) * mm});
            skLineSegment(sketch, "E1802", {"start": v(-1791.73, -2373.73) * mm, "end": v(-1773.7, -2450.18) * mm});
            skLineSegment(sketch, "E1803", {"start": v(-242.07, -491.84) * mm, "end": v(-106.18, -702.66) * mm});
            skLineSegment(sketch, "E1804", {"start": v(-106.18, -702.66) * mm, "end": v(-93.48, -720.44) * mm});
            skLineSegment(sketch, "E1805", {"start": v(-93.48, -720.44) * mm, "end": v(-75.7, -736.95) * mm});
            skLineSegment(sketch, "E1806", {"start": v(-75.7, -736.95) * mm, "end": v(-68.08, -740.76) * mm});
            skLineSegment(sketch, "E1807", {"start": v(-68.08, -740.76) * mm, "end": v(-57.92, -744.57) * mm});
            skLineSegment(sketch, "E1808", {"start": v(-57.92, -744.57) * mm, "end": v(-47.76, -745.84) * mm});
            skLineSegment(sketch, "E1809", {"start": v(-47.76, -745.84) * mm, "end": v(-26.17, -745.84) * mm});
            skLineSegment(sketch, "E1810", {"start": v(-26.17, -745.84) * mm, "end": v(-18.55, -744.57) * mm});
            skLineSegment(sketch, "E1811", {"start": v(-18.55, -744.57) * mm, "end": v(-5.85, -742.03) * mm});
            skLineSegment(sketch, "E1812", {"start": v(-5.85, -742.03) * mm, "end": v(10.66, -734.41) * mm});
            skLineSegment(sketch, "E1813", {"start": v(10.66, -734.41) * mm, "end": v(27.17, -725.52) * mm});
            skLineSegment(sketch, "E1814", {"start": v(27.17, -725.52) * mm, "end": v(42.4, -715.36) * mm});
            skLineSegment(sketch, "E1815", {"start": v(42.4, -715.36) * mm, "end": v(76.7, -689.96) * mm});
            skLineSegment(sketch, "E1816", {"start": v(76.7, -689.96) * mm, "end": v(109.72, -659.48) * mm});
            skLineSegment(sketch, "E1817", {"start": v(109.72, -659.48) * mm, "end": v(504.69, -249.27) * mm});
            skLineSegment(sketch, "E1818", {"start": v(831.84, -2268.82) * mm, "end": v(791.7, -2295.24) * mm});
            skLineSegment(sketch, "E1819", {"start": v(-69.1, -1384.14) * mm, "end": v(-37.6, -1435.45) * mm});
            skLineSegment(sketch, "E1820", {"start": v(-37.6, -1435.45) * mm, "end": v(-45.22, -1441.8) * mm});
            skLineSegment(sketch, "E1821", {"start": v(-45.22, -1441.8) * mm, "end": v(-22.36, -1476.1) * mm});
            skLineSegment(sketch, "E1822", {"start": v(-22.36, -1476.1) * mm, "end": v(221.48, -1319.12) * mm});
            skLineSegment(sketch, "E1823", {"start": v(221.48, -1319.12) * mm, "end": v(407.4, -1199.23) * mm});
            skLineSegment(sketch, "E1824", {"start": v(407.4, -1199.23) * mm, "end": v(462.78, -1163.67) * mm});
            skLineSegment(sketch, "E1825", {"start": v(462.78, -1163.67) * mm, "end": v(441.19, -1130.65) * mm});
            skLineSegment(sketch, "E1826", {"start": v(441.19, -1130.65) * mm, "end": v(428.49, -1139.54) * mm});
            skLineSegment(sketch, "E1827", {"start": v(428.49, -1139.54) * mm, "end": v(410.45, -1111.85) * mm});
            skLineSegment(sketch, "E1828", {"start": v(1428.23, 985.42) * mm, "end": v(1454.14, 1007.27) * mm});
            skLineSegment(sketch, "E1829", {"start": v(1001.26, -2624.17) * mm, "end": v(1041.13, -2597) * mm});
            skLineSegment(sketch, "E1830", {"start": v(-708.16, -937.61) * mm, "end": v(-731.02, -895.7) * mm});
            skLineSegment(sketch, "E1831", {"start": v(1906.77, -1389.73) * mm, "end": v(1892.8, -1402.43) * mm});
            skLineSegment(sketch, "E1832", {"start": v(1892.8, -1402.43) * mm, "end": v(1699.76, -1210.66) * mm});
            skLineSegment(sketch, "E1833", {"start": v(1699.76, -1210.66) * mm, "end": v(1709.92, -1196.7) * mm});
            skLineSegment(sketch, "E1834", {"start": v(-2161.55, -2500.73) * mm, "end": v(-2130.82, -2494.88) * mm});
            skLineSegment(sketch, "E1835", {"start": v(-2321.06, -616.3) * mm, "end": v(-2263.91, -736.95) * mm});
            skLineSegment(sketch, "E1836", {"start": v(-2263.91, -736.95) * mm, "end": v(-2326.14, -956.66) * mm});
            skLineSegment(sketch, "E1837", {"start": v(-2326.14, -956.66) * mm, "end": v(-1978.16, -1712.31) * mm});
            skLineSegment(sketch, "E1838", {"start": v(-1978.16, -1712.31) * mm, "end": v(-1962.92, -1705.96) * mm});
            skLineSegment(sketch, "E1839", {"start": v(-1962.92, -1705.96) * mm, "end": v(-1950.22, -1732.63) * mm});
            skLineSegment(sketch, "E1840", {"start": v(1558.79, 814.23) * mm, "end": v(1586.98, 839.88) * mm});
            skLineSegment(sketch, "E1841", {"start": v(944.87, -2443.07) * mm, "end": v(913.37, -2395.82) * mm});
            skLineSegment(sketch, "E1842", {"start": v(-496.07, -1817.72) * mm, "end": v(-469.4, -1887.57) * mm});
            skLineSegment(sketch, "E1843", {"start": v(-762.01, -1761.59) * mm, "end": v(-696.73, -1959.96) * mm});
            skLineSegment(sketch, "E1844", {"start": v(1659.12, -2106.01) * mm, "end": v(1669.28, -2116.17) * mm});
            skLineSegment(sketch, "E1845", {"start": v(1669.28, -2116.17) * mm, "end": v(1773.16, -2046.57) * mm});
            skLineSegment(sketch, "E1846", {"start": v(695.44, -173.58) * mm, "end": v(895.85, 29.37) * mm});
            skLineSegment(sketch, "E1847", {"start": v(2884.41, 1038.5) * mm, "end": v(2858, 1074.07) * mm});
            skLineSegment(sketch, "E1848", {"start": v(2858, 1074.07) * mm, "end": v(2828.79, 1128.68) * mm});
            skLineSegment(sketch, "E1849", {"start": v(2828.79, 1128.68) * mm, "end": v(2784.34, 1244.25) * mm});
            skLineSegment(sketch, "E1850", {"start": v(2784.34, 1244.25) * mm, "end": v(2712.45, 1462.18) * mm});
            skLineSegment(sketch, "E1851", {"start": v(2712.45, 1462.18) * mm, "end": v(2671.05, 1587.15) * mm});
            skLineSegment(sketch, "E1852", {"start": v(2826.25, 1566.07) * mm, "end": v(2795.77, 1518.57) * mm});
            skLineSegment(sketch, "E1853", {"start": v(2795.77, 1518.57) * mm, "end": v(2909.56, 1433.48) * mm});
            skLineSegment(sketch, "E1854", {"start": v(2477, -1467.2) * mm, "end": v(2219.19, -1241.14) * mm});
            skLineSegment(sketch, "E1855", {"start": v(2219.19, -1241.14) * mm, "end": v(2230.62, -1228.19) * mm});
            skLineSegment(sketch, "E1856", {"start": v(361.18, -2457.8) * mm, "end": v(-27.44, -1872.33) * mm});
            skLineSegment(sketch, "E1857", {"start": v(-27.44, -1872.33) * mm, "end": v(-87.13, -1907.9) * mm});
            skLineSegment(sketch, "E1858", {"start": v(-87.13, -1907.9) * mm, "end": v(-330.97, -1830.42) * mm});
            skLineSegment(sketch, "E1859", {"start": v(-330.97, -1830.42) * mm, "end": v(-331.74, -1834.48) * mm});
            skLineSegment(sketch, "E1860", {"start": v(331.46, -1487.27) * mm, "end": v(405.37, -1603.1) * mm});
            skLineSegment(sketch, "E1861", {"start": v(1541.77, -1029.81) * mm, "end": v(1509.26, -1060.04) * mm});
            skLineSegment(sketch, "E1862", {"start": v(805.68, -2227.42) * mm, "end": v(846.32, -2201.26) * mm});
            skLineSegment(sketch, "E1863", {"start": v(846.32, -2201.26) * mm, "end": v(872.99, -2241.9) * mm});
            skLineSegment(sketch, "E1864", {"start": v(872.99, -2241.9) * mm, "end": v(831.84, -2268.82) * mm});
            skLineSegment(sketch, "E1865", {"start": v(574.54, -1958.7) * mm, "end": v(615.68, -1934.05) * mm});
            skLineSegment(sketch, "E1866", {"start": v(-1333, -1685.39) * mm, "end": v(-1298.71, -1665.32) * mm});
            skLineSegment(sketch, "E1867", {"start": v(-1298.71, -1665.32) * mm, "end": v(-1268.23, -1646.27) * mm});
            skLineSegment(sketch, "E1868", {"start": v(-1268.23, -1646.27) * mm, "end": v(-1192.03, -1599.28) * mm});
            skLineSegment(sketch, "E1869", {"start": v(-1192.03, -1599.28) * mm, "end": v(-1081.54, -1530.2) * mm});
            skLineSegment(sketch, "E1870", {"start": v(396.74, -1665.32) * mm, "end": v(381.5, -1676.75) * mm});
            skLineSegment(sketch, "E1871", {"start": v(381.5, -1676.75) * mm, "end": v(372.6, -1702.15) * mm});
            skLineSegment(sketch, "E1872", {"start": v(372.6, -1702.15) * mm, "end": v(382.77, -1716.12) * mm});
            skLineSegment(sketch, "E1873", {"start": v(382.77, -1716.12) * mm, "end": v(418.33, -1726.28) * mm});
            skLineSegment(sketch, "E1874", {"start": v(418.33, -1726.28) * mm, "end": v(461.5, -1695.8) * mm});
            skLineSegment(sketch, "E1875", {"start": v(461.5, -1695.8) * mm, "end": v(448.04, -1673.96) * mm});
            skLineSegment(sketch, "E1876", {"start": v(1041.13, -2597) * mm, "end": v(1081.27, -2569.56) * mm});
            skLineSegment(sketch, "E1877", {"start": v(1081.27, -2569.56) * mm, "end": v(1110.48, -2611.47) * mm});
            skLineSegment(sketch, "E1878", {"start": v(1110.48, -2611.47) * mm, "end": v(1067.3, -2640.43) * mm});
            skLineSegment(sketch, "E1879", {"start": v(-360.18, -1026.51) * mm, "end": v(-342.4, -1012.54) * mm});
            skLineSegment(sketch, "E1880", {"start": v(-342.4, -1012.54) * mm, "end": v(-336.05, -1006.2) * mm});
            skLineSegment(sketch, "E1881", {"start": v(-336.05, -1006.2) * mm, "end": v(-329.7, -998.57) * mm});
            skLineSegment(sketch, "E1882", {"start": v(-329.7, -998.57) * mm, "end": v(-323.35, -985.87) * mm});
            skLineSegment(sketch, "E1883", {"start": v(-323.35, -985.87) * mm, "end": v(-318.27, -974.44) * mm});
            skLineSegment(sketch, "E1884", {"start": v(-318.27, -974.44) * mm, "end": v(-315.73, -969.36) * mm});
            skLineSegment(sketch, "E1885", {"start": v(-315.73, -969.36) * mm, "end": v(-314.46, -961.74) * mm});
            skLineSegment(sketch, "E1886", {"start": v(-314.46, -961.74) * mm, "end": v(-313.2, -955.4) * mm});
            skLineSegment(sketch, "E1887", {"start": v(-313.2, -955.4) * mm, "end": v(-314.46, -949.04) * mm});
            skLineSegment(sketch, "E1888", {"start": v(-314.46, -949.04) * mm, "end": v(-317, -942.7) * mm});
            skLineSegment(sketch, "E1889", {"start": v(-317, -942.7) * mm, "end": v(-318.27, -940.15) * mm});
            skLineSegment(sketch, "E1890", {"start": v(-318.27, -940.15) * mm, "end": v(-465.6, -725.52) * mm});
            skLineSegment(sketch, "E1891", {"start": v(791.7, -2295.24) * mm, "end": v(763.77, -2254.6) * mm});
            skLineSegment(sketch, "E1892", {"start": v(2140.45, -1170.02) * mm, "end": v(2219.19, -1241.14) * mm});
            skLineSegment(sketch, "E1893", {"start": v(602.48, -152.24) * mm, "end": v(439.92, -11.78) * mm});
            skLineSegment(sketch, "E1894", {"start": v(439.92, -11.78) * mm, "end": v(417.06, 11.08) * mm});
            skLineSegment(sketch, "E1895", {"start": v(2235.7, -1189.07) * mm, "end": v(2727.7, -636.87) * mm});
            skLineSegment(sketch, "E1896", {"start": v(-794.52, -956.66) * mm, "end": v(-743.72, -922.37) * mm});
            skLineSegment(sketch, "E1897", {"start": v(-743.72, -922.37) * mm, "end": v(-757.7, -899.51) * mm});
            skLineSegment(sketch, "E1898", {"start": v(1006.59, 606.46) * mm, "end": v(1165.09, 442.88) * mm});
            skLineSegment(sketch, "E1899", {"start": v(1577.84, -1971.4) * mm, "end": v(1514.34, -1872.33) * mm});
            skLineSegment(sketch, "E1900", {"start": v(2739.89, -645.51) * mm, "end": v(2879.59, -744.57) * mm});
            skLineSegment(sketch, "E1901", {"start": v(1980.43, -1467.2) * mm, "end": v(2007.1, -1491.33) * mm});
            skLineSegment(sketch, "E1902", {"start": v(2007.1, -1491.33) * mm, "end": v(2028.69, -1479.9) * mm});
            skLineSegment(sketch, "E1903", {"start": v(2028.69, -1479.9) * mm, "end": v(2037.58, -1491.33) * mm});
            skLineSegment(sketch, "E1904", {"start": v(2037.58, -1491.33) * mm, "end": v(2015.99, -1506.57) * mm});
            skLineSegment(sketch, "E1905", {"start": v(2015.99, -1506.57) * mm, "end": v(2073.14, -1599.28) * mm});
            skLineSegment(sketch, "E1906", {"start": v(2073.14, -1599.28) * mm, "end": v(2097.27, -1585.31) * mm});
            skLineSegment(sketch, "E1907", {"start": v(2097.27, -1585.31) * mm, "end": v(2107.43, -1599.28) * mm});
            skLineSegment(sketch, "E1908", {"start": v(2107.43, -1599.28) * mm, "end": v(2217.92, -1609.44) * mm});
            skLineSegment(sketch, "E1909", {"start": v(-1917.2, -2186.02) * mm, "end": v(-1917.2, -2196.18) * mm});
            skLineSegment(sketch, "E1910", {"start": v(-1917.2, -2196.18) * mm, "end": v(-1917.2, -2206.34) * mm});
            skLineSegment(sketch, "E1911", {"start": v(-1917.2, -2196.18) * mm, "end": v(-1907.04, -2196.18) * mm});
            skLineSegment(sketch, "E1912", {"start": v(-1917.2, -2196.18) * mm, "end": v(-1927.36, -2196.18) * mm});
            skArc(sketch, "E1913", {"start": v(-1681.11, -2288.38) * mm, "mid": v(-1680.48, -2289.02) * mm, "end": v(-1679.84, -2288.38) * mm});
            skArc(sketch, "E1914", {"start": v(-1679.84, -2288.38) * mm, "mid": v(-1680.48, -2287.75) * mm, "end": v(-1681.11, -2288.38) * mm});
            skLineSegment(sketch, "E1915", {"start": v(-54.11, -1035.4) * mm, "end": v(-54.11, -1045.56) * mm});
            skLineSegment(sketch, "E1916", {"start": v(-54.11, -1045.56) * mm, "end": v(-54.11, -1055.72) * mm});
            skLineSegment(sketch, "E1917", {"start": v(-54.11, -1045.56) * mm, "end": v(-43.95, -1045.56) * mm});
            skLineSegment(sketch, "E1918", {"start": v(-54.11, -1045.56) * mm, "end": v(-64.27, -1045.56) * mm});
            skArc(sketch, "E1919", {"start": v(1214.62, 354.7) * mm, "mid": v(1215.89, 353.42) * mm, "end": v(1217.16, 354.7) * mm});
            skArc(sketch, "E1920", {"start": v(1217.16, 354.7) * mm, "mid": v(1215.89, 355.96) * mm, "end": v(1214.62, 354.7) * mm});
            skLineSegment(sketch, "E1921", {"start": v(1215.89, 347.07) * mm, "end": v(1215.89, 316.6) * mm});
            skArc(sketch, "E1922", {"start": v(1214.62, 309.22) * mm, "mid": v(1215.89, 307.95) * mm, "end": v(1217.16, 309.22) * mm});
            skArc(sketch, "E1923", {"start": v(1217.16, 309.22) * mm, "mid": v(1215.89, 310.5) * mm, "end": v(1214.62, 309.22) * mm});
            skArc(sketch, "E1924", {"start": v(1194.04, 331.51) * mm, "mid": v(1195.3, 332.78) * mm, "end": v(1194.04, 334.05) * mm});
            skArc(sketch, "E1925", {"start": v(1194.04, 334.05) * mm, "mid": v(1192.77, 332.78) * mm, "end": v(1194.04, 331.51) * mm});
            skLineSegment(sketch, "E1926", {"start": v(1201.97, 332.39) * mm, "end": v(1232.45, 332.39) * mm});
            skArc(sketch, "E1927", {"start": v(1240.07, 331.38) * mm, "mid": v(1241.34, 332.65) * mm, "end": v(1240.07, 333.92) * mm});
            skArc(sketch, "E1928", {"start": v(1240.07, 333.92) * mm, "mid": v(1238.8, 332.65) * mm, "end": v(1240.07, 331.38) * mm});
            skSolve(sketch);
        }
        {
            var Q0;
            Q0=makeQuery(id+"F0.imprint","IMPRINT",FACE,{"disambiguationData":[TD([[makeQuery(id+"F0.imprint","IMPRINT",EDGE,{"derivedFrom":sQuery(id+"F0.wireOp",EDGE,"E24")}),-1.0]])]});
            var Q1;
            Q1=makeQuery(id+"F0.imprint","IMPRINT",FACE,{"disambiguationData":[TD([[makeQuery(id+"F0.imprint","IMPRINT",EDGE,{"derivedFrom":sQuery(id+"F0.wireOp",EDGE,"E158")}),-1.0]])]});
            var Q2;
            Q2=makeQuery(id+"F0.imprint","IMPRINT",FACE,{"disambiguationData":[TD([[makeQuery(id+"F0.imprint","IMPRINT",EDGE,{"derivedFrom":sQuery(id+"F0.wireOp",EDGE,"E124")}),1.0]])]});
            var Q3;
            Q3=makeQuery(id+"F0.imprint","IMPRINT",FACE,{"disambiguationData":[TD([[makeQuery(id+"F0.imprint","IMPRINT",EDGE,{"derivedFrom":sQuery(id+"F0.wireOp",EDGE,"E103")}),1.0]])]});
            var Q4;
            Q4=makeQuery(id+"F0.imprint","IMPRINT",FACE,{"disambiguationData":[TD([[makeQuery(id+"F0.imprint","IMPRINT",EDGE,{"derivedFrom":sQuery(id+"F0.wireOp",EDGE,"E172")}),-1.0]])]});
            var Q5;
            Q5=makeQuery(id+"F0.imprint","IMPRINT",FACE,{"disambiguationData":[TD([[makeQuery(id+"F0.imprint","IMPRINT",EDGE,{"derivedFrom":sQuery(id+"F0.wireOp",EDGE,"E25")}),1.0]])]});
            var Q6;
            Q6=makeQuery(id+"F0.imprint","IMPRINT",FACE,{"disambiguationData":[TD([[makeQuery(id+"F0.imprint","IMPRINT",EDGE,{"derivedFrom":sQuery(id+"F0.wireOp",EDGE,"E220")}),1.0]])]});
            var Q7;
            Q7=makeQuery(id+"F0.imprint","IMPRINT",FACE,{"disambiguationData":[TD([[makeQuery(id+"F0.imprint","IMPRINT",EDGE,{"derivedFrom":sQuery(id+"F0.wireOp",EDGE,"E186")}),-1.0]])]});
            var Q8;
            Q8=makeQuery(id+"F0.imprint","IMPRINT",FACE,{"disambiguationData":[TD([[makeQuery(id+"F0.imprint","IMPRINT",EDGE,{"derivedFrom":sQuery(id+"F0.wireOp",EDGE,"E536")}),1.0]])]});
            var Q9;
            Q9=makeQuery(id+"F0.imprint","IMPRINT",FACE,{"disambiguationData":[TD([[makeQuery(id+"F0.imprint","IMPRINT",EDGE,{"derivedFrom":sQuery(id+"F0.wireOp",EDGE,"E155")}),1.0]])]});
            var Q10;
            Q10=makeQuery(id+"F0.imprint","IMPRINT",FACE,{"disambiguationData":[TD([[makeQuery(id+"F0.imprint","IMPRINT",EDGE,{"derivedFrom":sQuery(id+"F0.wireOp",EDGE,"E130")}),-1.0]])]});
            var Q11;
            Q11=makeQuery(id+"F0.imprint","IMPRINT",FACE,{"disambiguationData":[TD([[makeQuery(id+"F0.imprint","IMPRINT",EDGE,{"derivedFrom":sQuery(id+"F0.wireOp",EDGE,"E240")}),1.0]])]});
            var Q12;
            Q12=makeQuery(id+"F0.imprint","IMPRINT",FACE,{"disambiguationData":[TD([[makeQuery(id+"F0.imprint","IMPRINT",EDGE,{"derivedFrom":sQuery(id+"F0.wireOp",EDGE,"E149")}),-1.0]])]});
            var Q13;
            Q13=makeQuery(id+"F0.imprint","IMPRINT",FACE,{"disambiguationData":[TD([[makeQuery(id+"F0.imprint","IMPRINT",EDGE,{"derivedFrom":sQuery(id+"F0.wireOp",EDGE,"E149")}),1.0]])]});
            var Q14;
            Q14=makeQuery(id+"F0.imprint","IMPRINT",FACE,{"disambiguationData":[TD([[makeQuery(id+"F0.imprint","IMPRINT",EDGE,{"derivedFrom":sQuery(id+"F0.wireOp",EDGE,"E153")}),1.0]])]});
            var Q15;
            Q15=makeQuery(id+"F0.imprint","IMPRINT",FACE,{"disambiguationData":[TD([[makeQuery(id+"F0.imprint","IMPRINT",EDGE,{"derivedFrom":sQuery(id+"F0.wireOp",EDGE,"E178")}),1.0]])]});
            var Q16;
            Q16=makeQuery(id+"F0.imprint","IMPRINT",FACE,{"disambiguationData":[TD([[makeQuery(id+"F0.imprint","IMPRINT",EDGE,{"derivedFrom":sQuery(id+"F0.wireOp",EDGE,"E12")}),-1.0]])]});
            var Q17;
            Q17=makeQuery(id+"F0.imprint","IMPRINT",FACE,{"disambiguationData":[TD([[makeQuery(id+"F0.imprint","IMPRINT",EDGE,{"derivedFrom":sQuery(id+"F0.wireOp",EDGE,"E140")}),1.0]])]});
            var Q18;
            Q18=makeQuery(id+"F0.imprint","IMPRINT",FACE,{"disambiguationData":[TD([[makeQuery(id+"F0.imprint","IMPRINT",EDGE,{"derivedFrom":sQuery(id+"F0.wireOp",EDGE,"E205")}),-1.0]])]});
            extrude(context, id + "F1", {"entities" : qUnion([Q0, Q1, Q2, Q3, Q4, Q5, Q6, Q7, Q8, Q9, Q10, Q11, Q12, Q13, Q14, Q15, Q16, Q17, Q18]), "depth" : 350 * mm, "offsetDistance" : 25 * mm});
        }
    });
